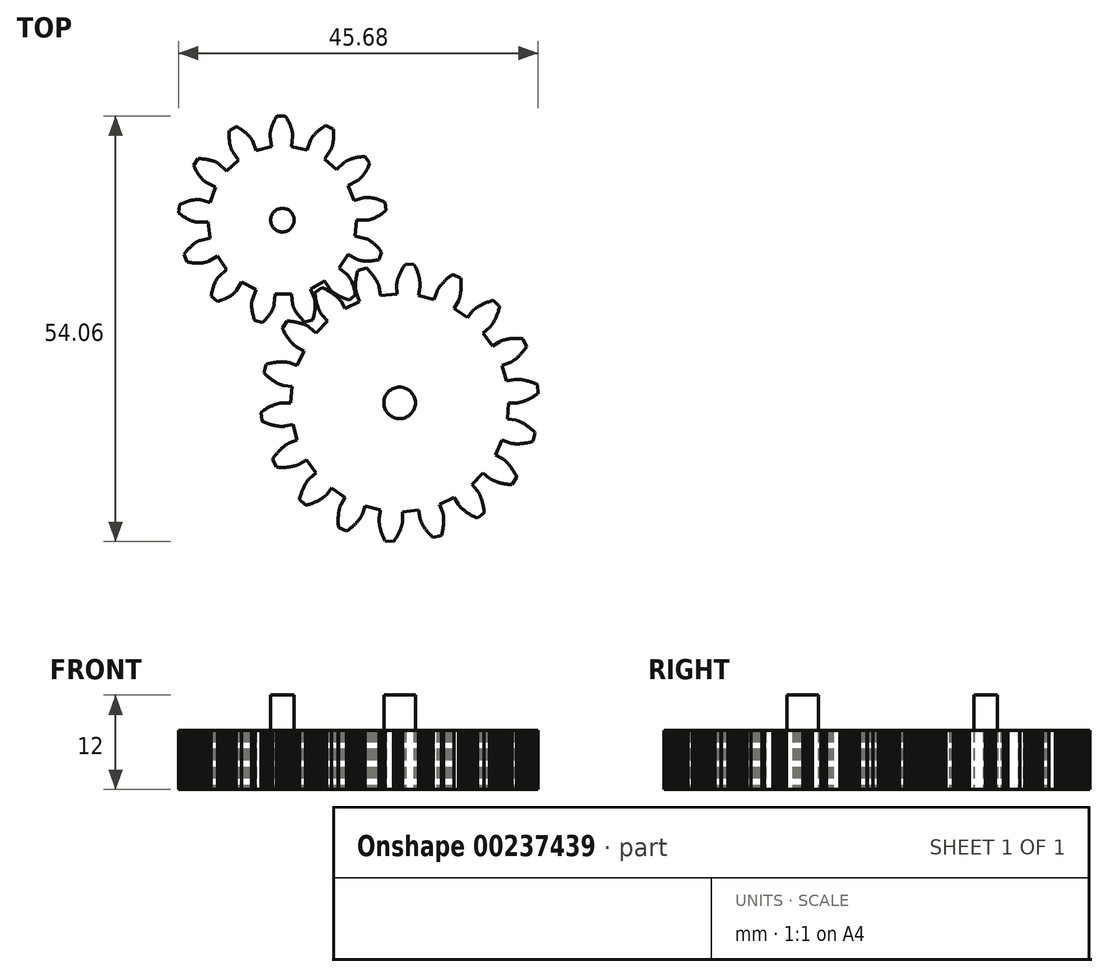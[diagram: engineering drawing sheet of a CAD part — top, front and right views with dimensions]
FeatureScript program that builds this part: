
annotation { "Feature Type Name" : "Feature", "Feature Type Description" : "" }
export const myFeature = defineFeature(function(context is Context, id is Id, definition is map)
    precondition{}
    {
        {
            var Q0;
            Q0=qCreatedBy(makeId("Top.planeOp"),FACE);
            var sketch = newSketch(context, id + "F0", { "sketchPlane" : qUnion([Q0])});
            skLineSegment(sketch, "E0", {"start": v(-0.69, 46.02) * mm, "end": v(3.77, 46.02) * mm});
            skLineSegment(sketch, "E1", {"start": v(3.77, 46.02) * mm, "end": v(3.8, 46.02) * mm});
            skLineSegment(sketch, "E2", {"start": v(3.8, 46.02) * mm, "end": v(3.86, 46.02) * mm});
            skLineSegment(sketch, "E3", {"start": v(3.86, 46.02) * mm, "end": v(3.94, 46.03) * mm});
            skLineSegment(sketch, "E4", {"start": v(3.94, 46.03) * mm, "end": v(4.05, 46.04) * mm});
            skLineSegment(sketch, "E5", {"start": v(4.05, 46.04) * mm, "end": v(4.18, 46.06) * mm});
            skLineSegment(sketch, "E6", {"start": v(4.18, 46.06) * mm, "end": v(4.34, 46.09) * mm});
            skLineSegment(sketch, "E7", {"start": v(4.34, 46.09) * mm, "end": v(4.52, 46.12) * mm});
            skLineSegment(sketch, "E8", {"start": v(4.52, 46.12) * mm, "end": v(4.72, 46.17) * mm});
            skLineSegment(sketch, "E9", {"start": v(4.72, 46.17) * mm, "end": v(4.95, 46.23) * mm});
            skLineSegment(sketch, "E10", {"start": v(4.95, 46.23) * mm, "end": v(5.2, 46.3) * mm});
            skLineSegment(sketch, "E11", {"start": v(5.2, 46.3) * mm, "end": v(5.48, 46.38) * mm});
            skLineSegment(sketch, "E12", {"start": v(5.48, 46.38) * mm, "end": v(5.78, 46.48) * mm});
            skLineSegment(sketch, "E13", {"start": v(5.78, 46.48) * mm, "end": v(6.1, 46.6) * mm});
            skLineSegment(sketch, "E14", {"start": v(6.1, 46.6) * mm, "end": v(6.44, 46.74) * mm});
            skLineSegment(sketch, "E15", {"start": v(6.44, 46.74) * mm, "end": v(6.8, 46.9) * mm});
            skLineSegment(sketch, "E16", {"start": v(6.8, 46.9) * mm, "end": v(7.18, 47.07) * mm});
            skLineSegment(sketch, "E17", {"start": v(7.18, 47.07) * mm, "end": v(7.58, 47.27) * mm});
            skLineSegment(sketch, "E18", {"start": v(7.58, 47.27) * mm, "end": v(8, 47.49) * mm});
            skLineSegment(sketch, "E19", {"start": v(8, 47.49) * mm, "end": v(8.42, 47.73) * mm});
            skLineSegment(sketch, "E20", {"start": v(8.42, 47.73) * mm, "end": v(8.87, 48) * mm});
            skLineSegment(sketch, "E21", {"start": v(8.87, 48) * mm, "end": v(9.33, 48.3) * mm});
            skLineSegment(sketch, "E22", {"start": v(9.33, 48.3) * mm, "end": v(9.8, 48.62) * mm});
            skLineSegment(sketch, "E23", {"start": v(9.8, 48.62) * mm, "end": v(10.3, 48.96) * mm});
            skLineSegment(sketch, "E24", {"start": v(10.3, 48.96) * mm, "end": v(10.8, 49.34) * mm});
            skLineSegment(sketch, "E25", {"start": v(10.8, 49.34) * mm, "end": v(11.3, 49.75) * mm});
            skLineSegment(sketch, "E26", {"start": v(11.3, 49.75) * mm, "end": v(11.76, 50.18) * mm});
            skLineSegment(sketch, "E27", {"start": v(11.76, 50.18) * mm, "end": v(11.3, 53.55) * mm});
            skLineSegment(sketch, "E28", {"start": v(11.3, 53.55) * mm, "end": v(10.75, 53.85) * mm});
            skLineSegment(sketch, "E29", {"start": v(10.75, 53.85) * mm, "end": v(10.16, 54.1) * mm});
            skLineSegment(sketch, "E30", {"start": v(10.16, 54.1) * mm, "end": v(9.58, 54.34) * mm});
            skLineSegment(sketch, "E31", {"start": v(9.58, 54.34) * mm, "end": v(9.01, 54.55) * mm});
            skLineSegment(sketch, "E32", {"start": v(9.01, 54.55) * mm, "end": v(8.47, 54.74) * mm});
            skLineSegment(sketch, "E33", {"start": v(8.47, 54.74) * mm, "end": v(7.95, 54.9) * mm});
            skLineSegment(sketch, "E34", {"start": v(7.95, 54.9) * mm, "end": v(7.45, 55.04) * mm});
            skLineSegment(sketch, "E35", {"start": v(7.45, 55.04) * mm, "end": v(6.97, 55.16) * mm});
            skLineSegment(sketch, "E36", {"start": v(6.97, 55.16) * mm, "end": v(6.5, 55.26) * mm});
            skLineSegment(sketch, "E37", {"start": v(6.5, 55.26) * mm, "end": v(6.07, 55.35) * mm});
            skLineSegment(sketch, "E38", {"start": v(6.07, 55.35) * mm, "end": v(5.66, 55.42) * mm});
            skLineSegment(sketch, "E39", {"start": v(5.66, 55.42) * mm, "end": v(5.27, 55.48) * mm});
            skLineSegment(sketch, "E40", {"start": v(5.27, 55.48) * mm, "end": v(4.9, 55.52) * mm});
            skLineSegment(sketch, "E41", {"start": v(4.9, 55.52) * mm, "end": v(4.57, 55.55) * mm});
            skLineSegment(sketch, "E42", {"start": v(4.57, 55.55) * mm, "end": v(4.25, 55.57) * mm});
            skLineSegment(sketch, "E43", {"start": v(4.25, 55.57) * mm, "end": v(3.97, 55.58) * mm});
            skLineSegment(sketch, "E44", {"start": v(3.97, 55.58) * mm, "end": v(3.7, 55.58) * mm});
            skLineSegment(sketch, "E45", {"start": v(3.7, 55.58) * mm, "end": v(3.47, 55.57) * mm});
            skLineSegment(sketch, "E46", {"start": v(3.47, 55.57) * mm, "end": v(3.25, 55.56) * mm});
            skLineSegment(sketch, "E47", {"start": v(3.25, 55.56) * mm, "end": v(3.07, 55.55) * mm});
            skLineSegment(sketch, "E48", {"start": v(3.07, 55.55) * mm, "end": v(2.91, 55.53) * mm});
            skLineSegment(sketch, "E49", {"start": v(2.91, 55.53) * mm, "end": v(2.78, 55.52) * mm});
            skLineSegment(sketch, "E50", {"start": v(2.78, 55.52) * mm, "end": v(2.67, 55.5) * mm});
            skLineSegment(sketch, "E51", {"start": v(2.67, 55.5) * mm, "end": v(2.6, 55.48) * mm});
            skLineSegment(sketch, "E52", {"start": v(2.6, 55.48) * mm, "end": v(2.54, 55.47) * mm});
            skLineSegment(sketch, "E53", {"start": v(2.54, 55.47) * mm, "end": v(2.5, 55.47) * mm});
            skLineSegment(sketch, "E54", {"start": v(2.5, 55.47) * mm, "end": v(-1.8, 54.3) * mm});
            skLineSegment(sketch, "E55", {"start": v(-1.8, 54.3) * mm, "end": v(-4.3, 60.64) * mm});
            skLineSegment(sketch, "E56", {"start": v(-4.3, 60.64) * mm, "end": v(-0.34, 62.71) * mm});
            skLineSegment(sketch, "E57", {"start": v(-0.34, 62.71) * mm, "end": v(-0.31, 62.73) * mm});
            skLineSegment(sketch, "E58", {"start": v(-0.31, 62.73) * mm, "end": v(-0.27, 62.76) * mm});
            skLineSegment(sketch, "E59", {"start": v(-0.27, 62.76) * mm, "end": v(-0.2, 62.8) * mm});
            skLineSegment(sketch, "E60", {"start": v(-0.2, 62.8) * mm, "end": v(-0.1, 62.86) * mm});
            skLineSegment(sketch, "E61", {"start": v(-0.1, 62.86) * mm, "end": v(0, 62.94) * mm});
            skLineSegment(sketch, "E62", {"start": v(0, 62.94) * mm, "end": v(0.13, 63.03) * mm});
            skLineSegment(sketch, "E63", {"start": v(0.13, 63.03) * mm, "end": v(0.27, 63.15) * mm});
            skLineSegment(sketch, "E64", {"start": v(0.27, 63.15) * mm, "end": v(0.43, 63.29) * mm});
            skLineSegment(sketch, "E65", {"start": v(0.43, 63.29) * mm, "end": v(0.6, 63.44) * mm});
            skLineSegment(sketch, "E66", {"start": v(0.6, 63.44) * mm, "end": v(0.8, 63.62) * mm});
            skLineSegment(sketch, "E67", {"start": v(0.8, 63.62) * mm, "end": v(1, 63.83) * mm});
            skLineSegment(sketch, "E68", {"start": v(1, 63.83) * mm, "end": v(1.22, 64.06) * mm});
            skLineSegment(sketch, "E69", {"start": v(1.22, 64.06) * mm, "end": v(1.45, 64.3) * mm});
            skLineSegment(sketch, "E70", {"start": v(1.45, 64.3) * mm, "end": v(1.69, 64.59) * mm});
            skLineSegment(sketch, "E71", {"start": v(1.69, 64.59) * mm, "end": v(1.93, 64.9) * mm});
            skLineSegment(sketch, "E72", {"start": v(1.93, 64.9) * mm, "end": v(2.19, 65.22) * mm});
            skLineSegment(sketch, "E73", {"start": v(2.19, 65.22) * mm, "end": v(2.45, 65.58) * mm});
            skLineSegment(sketch, "E74", {"start": v(2.45, 65.58) * mm, "end": v(2.71, 65.97) * mm});
            skLineSegment(sketch, "E75", {"start": v(2.71, 65.97) * mm, "end": v(2.98, 66.39) * mm});
            skLineSegment(sketch, "E76", {"start": v(2.98, 66.39) * mm, "end": v(3.25, 66.83) * mm});
            skLineSegment(sketch, "E77", {"start": v(3.25, 66.83) * mm, "end": v(3.53, 67.3) * mm});
            skLineSegment(sketch, "E78", {"start": v(3.53, 67.3) * mm, "end": v(3.8, 67.81) * mm});
            skLineSegment(sketch, "E79", {"start": v(3.8, 67.81) * mm, "end": v(4.07, 68.35) * mm});
            skLineSegment(sketch, "E80", {"start": v(4.07, 68.35) * mm, "end": v(4.33, 68.92) * mm});
            skLineSegment(sketch, "E81", {"start": v(4.33, 68.92) * mm, "end": v(4.6, 69.51) * mm});
            skLineSegment(sketch, "E82", {"start": v(4.6, 69.51) * mm, "end": v(4.8, 70.1) * mm});
            skLineSegment(sketch, "E83", {"start": v(4.8, 70.1) * mm, "end": v(2.83, 72.88) * mm});
            skLineSegment(sketch, "E84", {"start": v(2.83, 72.88) * mm, "end": v(2.2, 72.89) * mm});
            skLineSegment(sketch, "E85", {"start": v(2.2, 72.89) * mm, "end": v(1.55, 72.84) * mm});
            skLineSegment(sketch, "E86", {"start": v(1.55, 72.84) * mm, "end": v(0.93, 72.78) * mm});
            skLineSegment(sketch, "E87", {"start": v(0.93, 72.78) * mm, "end": v(0.34, 72.7) * mm});
            skLineSegment(sketch, "E88", {"start": v(0.34, 72.7) * mm, "end": v(-0.23, 72.61) * mm});
            skLineSegment(sketch, "E89", {"start": v(-0.23, 72.61) * mm, "end": v(-0.77, 72.51) * mm});
            skLineSegment(sketch, "E90", {"start": v(-0.77, 72.51) * mm, "end": v(-1.28, 72.4) * mm});
            skLineSegment(sketch, "E91", {"start": v(-1.28, 72.4) * mm, "end": v(-1.76, 72.29) * mm});
            skLineSegment(sketch, "E92", {"start": v(-1.76, 72.29) * mm, "end": v(-2.22, 72.17) * mm});
            skLineSegment(sketch, "E93", {"start": v(-2.22, 72.17) * mm, "end": v(-2.64, 72.04) * mm});
            skLineSegment(sketch, "E94", {"start": v(-2.64, 72.04) * mm, "end": v(-3.04, 71.91) * mm});
            skLineSegment(sketch, "E95", {"start": v(-3.04, 71.91) * mm, "end": v(-3.4, 71.78) * mm});
            skLineSegment(sketch, "E96", {"start": v(-3.4, 71.78) * mm, "end": v(-3.75, 71.65) * mm});
            skLineSegment(sketch, "E97", {"start": v(-3.75, 71.65) * mm, "end": v(-4.06, 71.52) * mm});
            skLineSegment(sketch, "E98", {"start": v(-4.06, 71.52) * mm, "end": v(-4.35, 71.39) * mm});
            skLineSegment(sketch, "E99", {"start": v(-4.35, 71.39) * mm, "end": v(-4.61, 71.26) * mm});
            skLineSegment(sketch, "E100", {"start": v(-4.61, 71.26) * mm, "end": v(-4.84, 71.14) * mm});
            skLineSegment(sketch, "E101", {"start": v(-4.84, 71.14) * mm, "end": v(-5.05, 71.03) * mm});
            skLineSegment(sketch, "E102", {"start": v(-5.05, 71.03) * mm, "end": v(-5.23, 70.92) * mm});
            skLineSegment(sketch, "E103", {"start": v(-5.23, 70.92) * mm, "end": v(-5.4, 70.82) * mm});
            skLineSegment(sketch, "E104", {"start": v(-5.4, 70.82) * mm, "end": v(-5.52, 70.73) * mm});
            skLineSegment(sketch, "E105", {"start": v(-5.52, 70.73) * mm, "end": v(-5.63, 70.66) * mm});
            skLineSegment(sketch, "E106", {"start": v(-5.63, 70.66) * mm, "end": v(-5.72, 70.6) * mm});
            skLineSegment(sketch, "E107", {"start": v(-5.72, 70.6) * mm, "end": v(-5.78, 70.54) * mm});
            skLineSegment(sketch, "E108", {"start": v(-5.78, 70.54) * mm, "end": v(-5.83, 70.5) * mm});
            skLineSegment(sketch, "E109", {"start": v(-5.83, 70.5) * mm, "end": v(-5.85, 70.49) * mm});
            skLineSegment(sketch, "E110", {"start": v(-5.85, 70.49) * mm, "end": v(-9.12, 67.45) * mm});
            skLineSegment(sketch, "E111", {"start": v(-9.12, 67.45) * mm, "end": v(-14.28, 71.9) * mm});
            skLineSegment(sketch, "E112", {"start": v(-14.28, 71.9) * mm, "end": v(-11.74, 75.58) * mm});
            skLineSegment(sketch, "E113", {"start": v(-11.74, 75.58) * mm, "end": v(-11.72, 75.6) * mm});
            skLineSegment(sketch, "E114", {"start": v(-11.72, 75.6) * mm, "end": v(-11.7, 75.65) * mm});
            skLineSegment(sketch, "E115", {"start": v(-11.7, 75.65) * mm, "end": v(-11.65, 75.72) * mm});
            skLineSegment(sketch, "E116", {"start": v(-11.65, 75.72) * mm, "end": v(-11.6, 75.82) * mm});
            skLineSegment(sketch, "E117", {"start": v(-11.6, 75.82) * mm, "end": v(-11.54, 75.94) * mm});
            skLineSegment(sketch, "E118", {"start": v(-11.54, 75.94) * mm, "end": v(-11.48, 76.08) * mm});
            skLineSegment(sketch, "E119", {"start": v(-11.48, 76.08) * mm, "end": v(-11.4, 76.25) * mm});
            skLineSegment(sketch, "E120", {"start": v(-11.4, 76.25) * mm, "end": v(-11.32, 76.45) * mm});
            skLineSegment(sketch, "E121", {"start": v(-11.32, 76.45) * mm, "end": v(-11.24, 76.67) * mm});
            skLineSegment(sketch, "E122", {"start": v(-11.24, 76.67) * mm, "end": v(-11.15, 76.92) * mm});
            skLineSegment(sketch, "E123", {"start": v(-11.15, 76.92) * mm, "end": v(-11.07, 77.2) * mm});
            skLineSegment(sketch, "E124", {"start": v(-11.07, 77.2) * mm, "end": v(-10.98, 77.5) * mm});
            skLineSegment(sketch, "E125", {"start": v(-10.98, 77.5) * mm, "end": v(-10.9, 77.83) * mm});
            skLineSegment(sketch, "E126", {"start": v(-10.9, 77.83) * mm, "end": v(-10.82, 78.18) * mm});
            skLineSegment(sketch, "E127", {"start": v(-10.82, 78.18) * mm, "end": v(-10.74, 78.57) * mm});
            skLineSegment(sketch, "E128", {"start": v(-10.74, 78.57) * mm, "end": v(-10.67, 78.98) * mm});
            skLineSegment(sketch, "E129", {"start": v(-10.67, 78.98) * mm, "end": v(-10.6, 79.42) * mm});
            skLineSegment(sketch, "E130", {"start": v(-10.6, 79.42) * mm, "end": v(-10.55, 79.89) * mm});
            skLineSegment(sketch, "E131", {"start": v(-10.55, 79.89) * mm, "end": v(-10.5, 80.38) * mm});
            skLineSegment(sketch, "E132", {"start": v(-10.5, 80.38) * mm, "end": v(-10.47, 80.9) * mm});
            skLineSegment(sketch, "E133", {"start": v(-10.47, 80.9) * mm, "end": v(-10.45, 81.45) * mm});
            skLineSegment(sketch, "E134", {"start": v(-10.45, 81.45) * mm, "end": v(-10.45, 82.02) * mm});
            skLineSegment(sketch, "E135", {"start": v(-10.45, 82.02) * mm, "end": v(-10.46, 82.62) * mm});
            skLineSegment(sketch, "E136", {"start": v(-10.46, 82.62) * mm, "end": v(-10.49, 83.24) * mm});
            skLineSegment(sketch, "E137", {"start": v(-10.49, 83.24) * mm, "end": v(-10.53, 83.9) * mm});
            skLineSegment(sketch, "E138", {"start": v(-10.53, 83.9) * mm, "end": v(-10.63, 84.51) * mm});
            skLineSegment(sketch, "E139", {"start": v(-10.63, 84.51) * mm, "end": v(-13.66, 86.06) * mm});
            skLineSegment(sketch, "E140", {"start": v(-13.66, 86.06) * mm, "end": v(-14.22, 85.77) * mm});
            skLineSegment(sketch, "E141", {"start": v(-14.22, 85.77) * mm, "end": v(-14.77, 85.43) * mm});
            skLineSegment(sketch, "E142", {"start": v(-14.77, 85.43) * mm, "end": v(-15.3, 85.08) * mm});
            skLineSegment(sketch, "E143", {"start": v(-15.3, 85.08) * mm, "end": v(-15.78, 84.74) * mm});
            skLineSegment(sketch, "E144", {"start": v(-15.78, 84.74) * mm, "end": v(-16.24, 84.4) * mm});
            skLineSegment(sketch, "E145", {"start": v(-16.24, 84.4) * mm, "end": v(-16.68, 84.06) * mm});
            skLineSegment(sketch, "E146", {"start": v(-16.68, 84.06) * mm, "end": v(-17.08, 83.73) * mm});
            skLineSegment(sketch, "E147", {"start": v(-17.08, 83.73) * mm, "end": v(-17.45, 83.4) * mm});
            skLineSegment(sketch, "E148", {"start": v(-17.45, 83.4) * mm, "end": v(-17.8, 83.08) * mm});
            skLineSegment(sketch, "E149", {"start": v(-17.8, 83.08) * mm, "end": v(-18.11, 82.77) * mm});
            skLineSegment(sketch, "E150", {"start": v(-18.11, 82.77) * mm, "end": v(-18.4, 82.47) * mm});
            skLineSegment(sketch, "E151", {"start": v(-18.4, 82.47) * mm, "end": v(-18.67, 82.18) * mm});
            skLineSegment(sketch, "E152", {"start": v(-18.67, 82.18) * mm, "end": v(-18.91, 81.9) * mm});
            skLineSegment(sketch, "E153", {"start": v(-18.91, 81.9) * mm, "end": v(-19.13, 81.65) * mm});
            skLineSegment(sketch, "E154", {"start": v(-19.13, 81.65) * mm, "end": v(-19.32, 81.4) * mm});
            skLineSegment(sketch, "E155", {"start": v(-19.32, 81.4) * mm, "end": v(-19.5, 81.17) * mm});
            skLineSegment(sketch, "E156", {"start": v(-19.5, 81.17) * mm, "end": v(-19.65, 80.95) * mm});
            skLineSegment(sketch, "E157", {"start": v(-19.65, 80.95) * mm, "end": v(-19.78, 80.75) * mm});
            skLineSegment(sketch, "E158", {"start": v(-19.78, 80.75) * mm, "end": v(-19.89, 80.57) * mm});
            skLineSegment(sketch, "E159", {"start": v(-19.89, 80.57) * mm, "end": v(-19.98, 80.41) * mm});
            skLineSegment(sketch, "E160", {"start": v(-19.98, 80.41) * mm, "end": v(-20.06, 80.27) * mm});
            skLineSegment(sketch, "E161", {"start": v(-20.06, 80.27) * mm, "end": v(-20.12, 80.16) * mm});
            skLineSegment(sketch, "E162", {"start": v(-20.12, 80.16) * mm, "end": v(-20.17, 80.06) * mm});
            skLineSegment(sketch, "E163", {"start": v(-20.17, 80.06) * mm, "end": v(-20.2, 79.99) * mm});
            skLineSegment(sketch, "E164", {"start": v(-20.2, 79.99) * mm, "end": v(-20.22, 79.93) * mm});
            skLineSegment(sketch, "E165", {"start": v(-20.22, 79.93) * mm, "end": v(-20.23, 79.9) * mm});
            skLineSegment(sketch, "E166", {"start": v(-20.23, 79.9) * mm, "end": v(-21.71, 75.7) * mm});
            skLineSegment(sketch, "E167", {"start": v(-21.71, 75.7) * mm, "end": v(-28.35, 77.25) * mm});
            skLineSegment(sketch, "E168", {"start": v(-28.35, 77.25) * mm, "end": v(-27.81, 81.68) * mm});
            skLineSegment(sketch, "E169", {"start": v(-27.81, 81.68) * mm, "end": v(-27.81, 81.7) * mm});
            skLineSegment(sketch, "E170", {"start": v(-27.81, 81.7) * mm, "end": v(-27.8, 81.76) * mm});
            skLineSegment(sketch, "E171", {"start": v(-27.8, 81.76) * mm, "end": v(-27.8, 81.84) * mm});
            skLineSegment(sketch, "E172", {"start": v(-27.8, 81.84) * mm, "end": v(-27.8, 81.95) * mm});
            skLineSegment(sketch, "E173", {"start": v(-27.8, 81.95) * mm, "end": v(-27.8, 82.08) * mm});
            skLineSegment(sketch, "E174", {"start": v(-27.8, 82.08) * mm, "end": v(-27.81, 82.24) * mm});
            skLineSegment(sketch, "E175", {"start": v(-27.81, 82.24) * mm, "end": v(-27.83, 82.43) * mm});
            skLineSegment(sketch, "E176", {"start": v(-27.83, 82.43) * mm, "end": v(-27.85, 82.64) * mm});
            skLineSegment(sketch, "E177", {"start": v(-27.85, 82.64) * mm, "end": v(-27.88, 82.87) * mm});
            skLineSegment(sketch, "E178", {"start": v(-27.88, 82.87) * mm, "end": v(-27.92, 83.13) * mm});
            skLineSegment(sketch, "E179", {"start": v(-27.92, 83.13) * mm, "end": v(-27.97, 83.42) * mm});
            skLineSegment(sketch, "E180", {"start": v(-27.97, 83.42) * mm, "end": v(-28.03, 83.72) * mm});
            skLineSegment(sketch, "E181", {"start": v(-28.03, 83.72) * mm, "end": v(-28.11, 84.06) * mm});
            skLineSegment(sketch, "E182", {"start": v(-28.11, 84.06) * mm, "end": v(-28.2, 84.41) * mm});
            skLineSegment(sketch, "E183", {"start": v(-28.2, 84.41) * mm, "end": v(-28.32, 84.79) * mm});
            skLineSegment(sketch, "E184", {"start": v(-28.32, 84.79) * mm, "end": v(-28.45, 85.18) * mm});
            skLineSegment(sketch, "E185", {"start": v(-28.45, 85.18) * mm, "end": v(-28.6, 85.6) * mm});
            skLineSegment(sketch, "E186", {"start": v(-28.6, 85.6) * mm, "end": v(-28.76, 86.04) * mm});
            skLineSegment(sketch, "E187", {"start": v(-28.76, 86.04) * mm, "end": v(-28.95, 86.5) * mm});
            skLineSegment(sketch, "E188", {"start": v(-28.95, 86.5) * mm, "end": v(-29.16, 86.98) * mm});
            skLineSegment(sketch, "E189", {"start": v(-29.16, 86.98) * mm, "end": v(-29.4, 87.47) * mm});
            skLineSegment(sketch, "E190", {"start": v(-29.4, 87.47) * mm, "end": v(-29.66, 87.98) * mm});
            skLineSegment(sketch, "E191", {"start": v(-29.66, 87.98) * mm, "end": v(-29.95, 88.5) * mm});
            skLineSegment(sketch, "E192", {"start": v(-29.95, 88.5) * mm, "end": v(-30.27, 89.05) * mm});
            skLineSegment(sketch, "E193", {"start": v(-30.27, 89.05) * mm, "end": v(-30.6, 89.6) * mm});
            skLineSegment(sketch, "E194", {"start": v(-30.6, 89.6) * mm, "end": v(-30.98, 90.1) * mm});
            skLineSegment(sketch, "E195", {"start": v(-30.98, 90.1) * mm, "end": v(-34.38, 90.06) * mm});
            skLineSegment(sketch, "E196", {"start": v(-34.38, 90.06) * mm, "end": v(-34.74, 89.55) * mm});
            skLineSegment(sketch, "E197", {"start": v(-34.74, 89.55) * mm, "end": v(-35.07, 88.99) * mm});
            skLineSegment(sketch, "E198", {"start": v(-35.07, 88.99) * mm, "end": v(-35.38, 88.44) * mm});
            skLineSegment(sketch, "E199", {"start": v(-35.38, 88.44) * mm, "end": v(-35.65, 87.9) * mm});
            skLineSegment(sketch, "E200", {"start": v(-35.65, 87.9) * mm, "end": v(-35.9, 87.4) * mm});
            skLineSegment(sketch, "E201", {"start": v(-35.9, 87.4) * mm, "end": v(-36.12, 86.9) * mm});
            skLineSegment(sketch, "E202", {"start": v(-36.12, 86.9) * mm, "end": v(-36.33, 86.4) * mm});
            skLineSegment(sketch, "E203", {"start": v(-36.33, 86.4) * mm, "end": v(-36.5, 85.95) * mm});
            skLineSegment(sketch, "E204", {"start": v(-36.5, 85.95) * mm, "end": v(-36.66, 85.5) * mm});
            skLineSegment(sketch, "E205", {"start": v(-36.66, 85.5) * mm, "end": v(-36.8, 85.08) * mm});
            skLineSegment(sketch, "E206", {"start": v(-36.8, 85.08) * mm, "end": v(-36.92, 84.68) * mm});
            skLineSegment(sketch, "E207", {"start": v(-36.92, 84.68) * mm, "end": v(-37.02, 84.3) * mm});
            skLineSegment(sketch, "E208", {"start": v(-37.02, 84.3) * mm, "end": v(-37.1, 83.95) * mm});
            skLineSegment(sketch, "E209", {"start": v(-37.1, 83.95) * mm, "end": v(-37.18, 83.61) * mm});
            skLineSegment(sketch, "E210", {"start": v(-37.18, 83.61) * mm, "end": v(-37.23, 83.3) * mm});
            skLineSegment(sketch, "E211", {"start": v(-37.23, 83.3) * mm, "end": v(-37.28, 83.02) * mm});
            skLineSegment(sketch, "E212", {"start": v(-37.28, 83.02) * mm, "end": v(-37.31, 82.76) * mm});
            skLineSegment(sketch, "E213", {"start": v(-37.31, 82.76) * mm, "end": v(-37.33, 82.52) * mm});
            skLineSegment(sketch, "E214", {"start": v(-37.33, 82.52) * mm, "end": v(-37.35, 82.31) * mm});
            skLineSegment(sketch, "E215", {"start": v(-37.35, 82.31) * mm, "end": v(-37.36, 82.13) * mm});
            skLineSegment(sketch, "E216", {"start": v(-37.36, 82.13) * mm, "end": v(-37.36, 81.97) * mm});
            skLineSegment(sketch, "E217", {"start": v(-37.36, 81.97) * mm, "end": v(-37.36, 81.83) * mm});
            skLineSegment(sketch, "E218", {"start": v(-37.36, 81.83) * mm, "end": v(-37.36, 81.73) * mm});
            skLineSegment(sketch, "E219", {"start": v(-37.36, 81.73) * mm, "end": v(-37.35, 81.65) * mm});
            skLineSegment(sketch, "E220", {"start": v(-37.35, 81.65) * mm, "end": v(-37.35, 81.59) * mm});
            skLineSegment(sketch, "E221", {"start": v(-37.35, 81.59) * mm, "end": v(-37.34, 81.56) * mm});
            skLineSegment(sketch, "E222", {"start": v(-37.34, 81.56) * mm, "end": v(-36.7, 77.15) * mm});
            skLineSegment(sketch, "E223", {"start": v(-36.7, 77.15) * mm, "end": v(-43.3, 75.43) * mm});
            skLineSegment(sketch, "E224", {"start": v(-43.3, 75.43) * mm, "end": v(-44.88, 79.6) * mm});
            skLineSegment(sketch, "E225", {"start": v(-44.88, 79.6) * mm, "end": v(-44.9, 79.63) * mm});
            skLineSegment(sketch, "E226", {"start": v(-44.9, 79.63) * mm, "end": v(-44.92, 79.68) * mm});
            skLineSegment(sketch, "E227", {"start": v(-44.92, 79.68) * mm, "end": v(-44.95, 79.76) * mm});
            skLineSegment(sketch, "E228", {"start": v(-44.95, 79.76) * mm, "end": v(-45, 79.85) * mm});
            skLineSegment(sketch, "E229", {"start": v(-45, 79.85) * mm, "end": v(-45.06, 79.97) * mm});
            skLineSegment(sketch, "E230", {"start": v(-45.06, 79.97) * mm, "end": v(-45.14, 80.1) * mm});
            skLineSegment(sketch, "E231", {"start": v(-45.14, 80.1) * mm, "end": v(-45.24, 80.26) * mm});
            skLineSegment(sketch, "E232", {"start": v(-45.24, 80.26) * mm, "end": v(-45.36, 80.44) * mm});
            skLineSegment(sketch, "E233", {"start": v(-45.36, 80.44) * mm, "end": v(-45.5, 80.63) * mm});
            skLineSegment(sketch, "E234", {"start": v(-45.5, 80.63) * mm, "end": v(-45.65, 80.85) * mm});
            skLineSegment(sketch, "E235", {"start": v(-45.65, 80.85) * mm, "end": v(-45.83, 81.07) * mm});
            skLineSegment(sketch, "E236", {"start": v(-45.83, 81.07) * mm, "end": v(-46.03, 81.32) * mm});
            skLineSegment(sketch, "E237", {"start": v(-46.03, 81.32) * mm, "end": v(-46.25, 81.57) * mm});
            skLineSegment(sketch, "E238", {"start": v(-46.25, 81.57) * mm, "end": v(-46.5, 81.84) * mm});
            skLineSegment(sketch, "E239", {"start": v(-46.5, 81.84) * mm, "end": v(-46.77, 82.13) * mm});
            skLineSegment(sketch, "E240", {"start": v(-46.77, 82.13) * mm, "end": v(-47.07, 82.42) * mm});
            skLineSegment(sketch, "E241", {"start": v(-47.07, 82.42) * mm, "end": v(-47.4, 82.72) * mm});
            skLineSegment(sketch, "E242", {"start": v(-47.4, 82.72) * mm, "end": v(-47.75, 83.03) * mm});
            skLineSegment(sketch, "E243", {"start": v(-47.75, 83.03) * mm, "end": v(-48.13, 83.35) * mm});
            skLineSegment(sketch, "E244", {"start": v(-48.13, 83.35) * mm, "end": v(-48.54, 83.67) * mm});
            skLineSegment(sketch, "E245", {"start": v(-48.54, 83.67) * mm, "end": v(-48.98, 84) * mm});
            skLineSegment(sketch, "E246", {"start": v(-48.98, 84) * mm, "end": v(-49.45, 84.33) * mm});
            skLineSegment(sketch, "E247", {"start": v(-49.45, 84.33) * mm, "end": v(-49.95, 84.66) * mm});
            skLineSegment(sketch, "E248", {"start": v(-49.95, 84.66) * mm, "end": v(-50.48, 85) * mm});
            skLineSegment(sketch, "E249", {"start": v(-50.48, 85) * mm, "end": v(-51.04, 85.32) * mm});
            skLineSegment(sketch, "E250", {"start": v(-51.04, 85.32) * mm, "end": v(-51.6, 85.6) * mm});
            skLineSegment(sketch, "E251", {"start": v(-51.6, 85.6) * mm, "end": v(-54.6, 83.98) * mm});
            skLineSegment(sketch, "E252", {"start": v(-54.6, 83.98) * mm, "end": v(-54.68, 83.35) * mm});
            skLineSegment(sketch, "E253", {"start": v(-54.68, 83.35) * mm, "end": v(-54.7, 82.7) * mm});
            skLineSegment(sketch, "E254", {"start": v(-54.7, 82.7) * mm, "end": v(-54.72, 82.08) * mm});
            skLineSegment(sketch, "E255", {"start": v(-54.72, 82.08) * mm, "end": v(-54.71, 81.48) * mm});
            skLineSegment(sketch, "E256", {"start": v(-54.71, 81.48) * mm, "end": v(-54.7, 80.9) * mm});
            skLineSegment(sketch, "E257", {"start": v(-54.7, 80.9) * mm, "end": v(-54.66, 80.36) * mm});
            skLineSegment(sketch, "E258", {"start": v(-54.66, 80.36) * mm, "end": v(-54.62, 79.84) * mm});
            skLineSegment(sketch, "E259", {"start": v(-54.62, 79.84) * mm, "end": v(-54.56, 79.35) * mm});
            skLineSegment(sketch, "E260", {"start": v(-54.56, 79.35) * mm, "end": v(-54.5, 78.88) * mm});
            skLineSegment(sketch, "E261", {"start": v(-54.5, 78.88) * mm, "end": v(-54.42, 78.44) * mm});
            skLineSegment(sketch, "E262", {"start": v(-54.42, 78.44) * mm, "end": v(-54.34, 78.03) * mm});
            skLineSegment(sketch, "E263", {"start": v(-54.34, 78.03) * mm, "end": v(-54.25, 77.65) * mm});
            skLineSegment(sketch, "E264", {"start": v(-54.25, 77.65) * mm, "end": v(-54.16, 77.3) * mm});
            skLineSegment(sketch, "E265", {"start": v(-54.16, 77.3) * mm, "end": v(-54.07, 76.97) * mm});
            skLineSegment(sketch, "E266", {"start": v(-54.07, 76.97) * mm, "end": v(-53.98, 76.67) * mm});
            skLineSegment(sketch, "E267", {"start": v(-53.98, 76.67) * mm, "end": v(-53.88, 76.4) * mm});
            skLineSegment(sketch, "E268", {"start": v(-53.88, 76.4) * mm, "end": v(-53.8, 76.15) * mm});
            skLineSegment(sketch, "E269", {"start": v(-53.8, 76.15) * mm, "end": v(-53.7, 75.93) * mm});
            skLineSegment(sketch, "E270", {"start": v(-53.7, 75.93) * mm, "end": v(-53.62, 75.74) * mm});
            skLineSegment(sketch, "E271", {"start": v(-53.62, 75.74) * mm, "end": v(-53.54, 75.57) * mm});
            skLineSegment(sketch, "E272", {"start": v(-53.54, 75.57) * mm, "end": v(-53.47, 75.43) * mm});
            skLineSegment(sketch, "E273", {"start": v(-53.47, 75.43) * mm, "end": v(-53.4, 75.3) * mm});
            skLineSegment(sketch, "E274", {"start": v(-53.4, 75.3) * mm, "end": v(-53.35, 75.21) * mm});
            skLineSegment(sketch, "E275", {"start": v(-53.35, 75.21) * mm, "end": v(-53.31, 75.14) * mm});
            skLineSegment(sketch, "E276", {"start": v(-53.31, 75.14) * mm, "end": v(-53.28, 75.1) * mm});
            skLineSegment(sketch, "E277", {"start": v(-53.28, 75.1) * mm, "end": v(-53.26, 75.07) * mm});
            skLineSegment(sketch, "E278", {"start": v(-53.26, 75.07) * mm, "end": v(-50.64, 71.46) * mm});
            skLineSegment(sketch, "E279", {"start": v(-50.64, 71.46) * mm, "end": v(-55.69, 66.88) * mm});
            skLineSegment(sketch, "E280", {"start": v(-55.69, 66.88) * mm, "end": v(-59.03, 69.84) * mm});
            skLineSegment(sketch, "E281", {"start": v(-59.03, 69.84) * mm, "end": v(-59.05, 69.86) * mm});
            skLineSegment(sketch, "E282", {"start": v(-59.05, 69.86) * mm, "end": v(-59.1, 69.9) * mm});
            skLineSegment(sketch, "E283", {"start": v(-59.1, 69.9) * mm, "end": v(-59.16, 69.94) * mm});
            skLineSegment(sketch, "E284", {"start": v(-59.16, 69.94) * mm, "end": v(-59.25, 70) * mm});
            skLineSegment(sketch, "E285", {"start": v(-59.25, 70) * mm, "end": v(-59.36, 70.08) * mm});
            skLineSegment(sketch, "E286", {"start": v(-59.36, 70.08) * mm, "end": v(-59.5, 70.16) * mm});
            skLineSegment(sketch, "E287", {"start": v(-59.5, 70.16) * mm, "end": v(-59.66, 70.25) * mm});
            skLineSegment(sketch, "E288", {"start": v(-59.66, 70.25) * mm, "end": v(-59.84, 70.36) * mm});
            skLineSegment(sketch, "E289", {"start": v(-59.84, 70.36) * mm, "end": v(-60.05, 70.47) * mm});
            skLineSegment(sketch, "E290", {"start": v(-60.05, 70.47) * mm, "end": v(-60.29, 70.58) * mm});
            skLineSegment(sketch, "E291", {"start": v(-60.29, 70.58) * mm, "end": v(-60.55, 70.7) * mm});
            skLineSegment(sketch, "E292", {"start": v(-60.55, 70.7) * mm, "end": v(-60.84, 70.82) * mm});
            skLineSegment(sketch, "E293", {"start": v(-60.84, 70.82) * mm, "end": v(-61.16, 70.95) * mm});
            skLineSegment(sketch, "E294", {"start": v(-61.16, 70.95) * mm, "end": v(-61.5, 71.07) * mm});
            skLineSegment(sketch, "E295", {"start": v(-61.5, 71.07) * mm, "end": v(-61.87, 71.2) * mm});
            skLineSegment(sketch, "E296", {"start": v(-61.87, 71.2) * mm, "end": v(-62.27, 71.31) * mm});
            skLineSegment(sketch, "E297", {"start": v(-62.27, 71.31) * mm, "end": v(-62.7, 71.43) * mm});
            skLineSegment(sketch, "E298", {"start": v(-62.7, 71.43) * mm, "end": v(-63.16, 71.54) * mm});
            skLineSegment(sketch, "E299", {"start": v(-63.16, 71.54) * mm, "end": v(-63.64, 71.64) * mm});
            skLineSegment(sketch, "E300", {"start": v(-63.64, 71.64) * mm, "end": v(-64.16, 71.74) * mm});
            skLineSegment(sketch, "E301", {"start": v(-64.16, 71.74) * mm, "end": v(-64.7, 71.82) * mm});
            skLineSegment(sketch, "E302", {"start": v(-64.7, 71.82) * mm, "end": v(-65.27, 71.9) * mm});
            skLineSegment(sketch, "E303", {"start": v(-65.27, 71.9) * mm, "end": v(-65.86, 71.96) * mm});
            skLineSegment(sketch, "E304", {"start": v(-65.86, 71.96) * mm, "end": v(-66.49, 72) * mm});
            skLineSegment(sketch, "E305", {"start": v(-66.49, 72) * mm, "end": v(-67.14, 72.04) * mm});
            skLineSegment(sketch, "E306", {"start": v(-67.14, 72.04) * mm, "end": v(-67.76, 72.02) * mm});
            skLineSegment(sketch, "E307", {"start": v(-67.76, 72.02) * mm, "end": v(-69.66, 69.2) * mm});
            skLineSegment(sketch, "E308", {"start": v(-69.66, 69.2) * mm, "end": v(-69.45, 68.6) * mm});
            skLineSegment(sketch, "E309", {"start": v(-69.45, 68.6) * mm, "end": v(-69.17, 68.02) * mm});
            skLineSegment(sketch, "E310", {"start": v(-69.17, 68.02) * mm, "end": v(-68.9, 67.46) * mm});
            skLineSegment(sketch, "E311", {"start": v(-68.9, 67.46) * mm, "end": v(-68.6, 66.93) * mm});
            skLineSegment(sketch, "E312", {"start": v(-68.6, 66.93) * mm, "end": v(-68.32, 66.43) * mm});
            skLineSegment(sketch, "E313", {"start": v(-68.32, 66.43) * mm, "end": v(-68.04, 65.96) * mm});
            skLineSegment(sketch, "E314", {"start": v(-68.04, 65.96) * mm, "end": v(-67.76, 65.52) * mm});
            skLineSegment(sketch, "E315", {"start": v(-67.76, 65.52) * mm, "end": v(-67.48, 65.11) * mm});
            skLineSegment(sketch, "E316", {"start": v(-67.48, 65.11) * mm, "end": v(-67.2, 64.73) * mm});
            skLineSegment(sketch, "E317", {"start": v(-67.2, 64.73) * mm, "end": v(-66.94, 64.38) * mm});
            skLineSegment(sketch, "E318", {"start": v(-66.94, 64.38) * mm, "end": v(-66.67, 64.05) * mm});
            skLineSegment(sketch, "E319", {"start": v(-66.67, 64.05) * mm, "end": v(-66.42, 63.75) * mm});
            skLineSegment(sketch, "E320", {"start": v(-66.42, 63.75) * mm, "end": v(-66.18, 63.48) * mm});
            skLineSegment(sketch, "E321", {"start": v(-66.18, 63.48) * mm, "end": v(-65.94, 63.23) * mm});
            skLineSegment(sketch, "E322", {"start": v(-65.94, 63.23) * mm, "end": v(-65.72, 63.01) * mm});
            skLineSegment(sketch, "E323", {"start": v(-65.72, 63.01) * mm, "end": v(-65.5, 62.81) * mm});
            skLineSegment(sketch, "E324", {"start": v(-65.5, 62.81) * mm, "end": v(-65.31, 62.64) * mm});
            skLineSegment(sketch, "E325", {"start": v(-65.31, 62.64) * mm, "end": v(-65.13, 62.48) * mm});
            skLineSegment(sketch, "E326", {"start": v(-65.13, 62.48) * mm, "end": v(-64.97, 62.35) * mm});
            skLineSegment(sketch, "E327", {"start": v(-64.97, 62.35) * mm, "end": v(-64.82, 62.24) * mm});
            skLineSegment(sketch, "E328", {"start": v(-64.82, 62.24) * mm, "end": v(-64.7, 62.15) * mm});
            skLineSegment(sketch, "E329", {"start": v(-64.7, 62.15) * mm, "end": v(-64.58, 62.07) * mm});
            skLineSegment(sketch, "E330", {"start": v(-64.58, 62.07) * mm, "end": v(-64.5, 62.01) * mm});
            skLineSegment(sketch, "E331", {"start": v(-64.5, 62.01) * mm, "end": v(-64.42, 61.97) * mm});
            skLineSegment(sketch, "E332", {"start": v(-64.42, 61.97) * mm, "end": v(-64.37, 61.94) * mm});
            skLineSegment(sketch, "E333", {"start": v(-64.37, 61.94) * mm, "end": v(-64.35, 61.93) * mm});
            skLineSegment(sketch, "E334", {"start": v(-64.35, 61.93) * mm, "end": v(-60.35, 59.95) * mm});
            skLineSegment(sketch, "E335", {"start": v(-60.35, 59.95) * mm, "end": v(-62.69, 53.55) * mm});
            skLineSegment(sketch, "E336", {"start": v(-62.69, 53.55) * mm, "end": v(-67.02, 54.62) * mm});
            skLineSegment(sketch, "E337", {"start": v(-67.02, 54.62) * mm, "end": v(-67.05, 54.62) * mm});
            skLineSegment(sketch, "E338", {"start": v(-67.05, 54.62) * mm, "end": v(-67.1, 54.63) * mm});
            skLineSegment(sketch, "E339", {"start": v(-67.1, 54.63) * mm, "end": v(-67.18, 54.65) * mm});
            skLineSegment(sketch, "E340", {"start": v(-67.18, 54.65) * mm, "end": v(-67.29, 54.66) * mm});
            skLineSegment(sketch, "E341", {"start": v(-67.29, 54.66) * mm, "end": v(-67.42, 54.67) * mm});
            skLineSegment(sketch, "E342", {"start": v(-67.42, 54.67) * mm, "end": v(-67.58, 54.68) * mm});
            skLineSegment(sketch, "E343", {"start": v(-67.58, 54.68) * mm, "end": v(-67.77, 54.7) * mm});
            skLineSegment(sketch, "E344", {"start": v(-67.77, 54.7) * mm, "end": v(-67.98, 54.7) * mm});
            skLineSegment(sketch, "E345", {"start": v(-67.98, 54.7) * mm, "end": v(-68.21, 54.7) * mm});
            skLineSegment(sketch, "E346", {"start": v(-68.21, 54.7) * mm, "end": v(-68.48, 54.69) * mm});
            skLineSegment(sketch, "E347", {"start": v(-68.48, 54.69) * mm, "end": v(-68.76, 54.67) * mm});
            skLineSegment(sketch, "E348", {"start": v(-68.76, 54.67) * mm, "end": v(-69.08, 54.65) * mm});
            skLineSegment(sketch, "E349", {"start": v(-69.08, 54.65) * mm, "end": v(-69.42, 54.6) * mm});
            skLineSegment(sketch, "E350", {"start": v(-69.42, 54.6) * mm, "end": v(-69.78, 54.56) * mm});
            skLineSegment(sketch, "E351", {"start": v(-69.78, 54.56) * mm, "end": v(-70.17, 54.5) * mm});
            skLineSegment(sketch, "E352", {"start": v(-70.17, 54.5) * mm, "end": v(-70.58, 54.41) * mm});
            skLineSegment(sketch, "E353", {"start": v(-70.58, 54.41) * mm, "end": v(-71.01, 54.32) * mm});
            skLineSegment(sketch, "E354", {"start": v(-71.01, 54.32) * mm, "end": v(-71.47, 54.2) * mm});
            skLineSegment(sketch, "E355", {"start": v(-71.47, 54.2) * mm, "end": v(-71.94, 54.07) * mm});
            skLineSegment(sketch, "E356", {"start": v(-71.94, 54.07) * mm, "end": v(-72.44, 53.92) * mm});
            skLineSegment(sketch, "E357", {"start": v(-72.44, 53.92) * mm, "end": v(-72.96, 53.74) * mm});
            skLineSegment(sketch, "E358", {"start": v(-72.96, 53.74) * mm, "end": v(-73.5, 53.54) * mm});
            skLineSegment(sketch, "E359", {"start": v(-73.5, 53.54) * mm, "end": v(-74.06, 53.32) * mm});
            skLineSegment(sketch, "E360", {"start": v(-74.06, 53.32) * mm, "end": v(-74.63, 53.07) * mm});
            skLineSegment(sketch, "E361", {"start": v(-74.63, 53.07) * mm, "end": v(-75.22, 52.8) * mm});
            skLineSegment(sketch, "E362", {"start": v(-75.22, 52.8) * mm, "end": v(-75.76, 52.49) * mm});
            skLineSegment(sketch, "E363", {"start": v(-75.76, 52.49) * mm, "end": v(-76.13, 49.1) * mm});
            skLineSegment(sketch, "E364", {"start": v(-76.13, 49.1) * mm, "end": v(-75.67, 48.69) * mm});
            skLineSegment(sketch, "E365", {"start": v(-75.67, 48.69) * mm, "end": v(-75.15, 48.3) * mm});
            skLineSegment(sketch, "E366", {"start": v(-75.15, 48.3) * mm, "end": v(-74.64, 47.93) * mm});
            skLineSegment(sketch, "E367", {"start": v(-74.64, 47.93) * mm, "end": v(-74.15, 47.59) * mm});
            skLineSegment(sketch, "E368", {"start": v(-74.15, 47.59) * mm, "end": v(-73.67, 47.28) * mm});
            skLineSegment(sketch, "E369", {"start": v(-73.67, 47.28) * mm, "end": v(-73.2, 47) * mm});
            skLineSegment(sketch, "E370", {"start": v(-73.2, 47) * mm, "end": v(-72.74, 46.74) * mm});
            skLineSegment(sketch, "E371", {"start": v(-72.74, 46.74) * mm, "end": v(-72.3, 46.5) * mm});
            skLineSegment(sketch, "E372", {"start": v(-72.3, 46.5) * mm, "end": v(-71.89, 46.3) * mm});
            skLineSegment(sketch, "E373", {"start": v(-71.89, 46.3) * mm, "end": v(-71.48, 46.1) * mm});
            skLineSegment(sketch, "E374", {"start": v(-71.48, 46.1) * mm, "end": v(-71.1, 45.94) * mm});
            skLineSegment(sketch, "E375", {"start": v(-71.1, 45.94) * mm, "end": v(-70.74, 45.8) * mm});
            skLineSegment(sketch, "E376", {"start": v(-70.74, 45.8) * mm, "end": v(-70.4, 45.67) * mm});
            skLineSegment(sketch, "E377", {"start": v(-70.4, 45.67) * mm, "end": v(-70.07, 45.56) * mm});
            skLineSegment(sketch, "E378", {"start": v(-70.07, 45.56) * mm, "end": v(-69.77, 45.46) * mm});
            skLineSegment(sketch, "E379", {"start": v(-69.77, 45.46) * mm, "end": v(-69.5, 45.38) * mm});
            skLineSegment(sketch, "E380", {"start": v(-69.5, 45.38) * mm, "end": v(-69.24, 45.32) * mm});
            skLineSegment(sketch, "E381", {"start": v(-69.24, 45.32) * mm, "end": v(-69, 45.27) * mm});
            skLineSegment(sketch, "E382", {"start": v(-69, 45.27) * mm, "end": v(-68.8, 45.23) * mm});
            skLineSegment(sketch, "E383", {"start": v(-68.8, 45.23) * mm, "end": v(-68.62, 45.2) * mm});
            skLineSegment(sketch, "E384", {"start": v(-68.62, 45.2) * mm, "end": v(-68.46, 45.17) * mm});
            skLineSegment(sketch, "E385", {"start": v(-68.46, 45.17) * mm, "end": v(-68.33, 45.16) * mm});
            skLineSegment(sketch, "E386", {"start": v(-68.33, 45.16) * mm, "end": v(-68.22, 45.15) * mm});
            skLineSegment(sketch, "E387", {"start": v(-68.22, 45.15) * mm, "end": v(-68.14, 45.14) * mm});
            skLineSegment(sketch, "E388", {"start": v(-68.14, 45.14) * mm, "end": v(-68.08, 45.14) * mm});
            skLineSegment(sketch, "E389", {"start": v(-68.08, 45.14) * mm, "end": v(-68.05, 45.14) * mm});
            skLineSegment(sketch, "E390", {"start": v(-68.05, 45.14) * mm, "end": v(-63.6, 45.25) * mm});
            skLineSegment(sketch, "E391", {"start": v(-63.6, 45.25) * mm, "end": v(-62.69, 38.5) * mm});
            skLineSegment(sketch, "E392", {"start": v(-62.69, 38.5) * mm, "end": v(-67.02, 37.42) * mm});
            skLineSegment(sketch, "E393", {"start": v(-67.02, 37.42) * mm, "end": v(-67.05, 37.42) * mm});
            skLineSegment(sketch, "E394", {"start": v(-67.05, 37.42) * mm, "end": v(-67.1, 37.4) * mm});
            skLineSegment(sketch, "E395", {"start": v(-67.1, 37.4) * mm, "end": v(-67.18, 37.37) * mm});
            skLineSegment(sketch, "E396", {"start": v(-67.18, 37.37) * mm, "end": v(-67.28, 37.34) * mm});
            skLineSegment(sketch, "E397", {"start": v(-67.28, 37.34) * mm, "end": v(-67.4, 37.29) * mm});
            skLineSegment(sketch, "E398", {"start": v(-67.4, 37.29) * mm, "end": v(-67.55, 37.22) * mm});
            skLineSegment(sketch, "E399", {"start": v(-67.55, 37.22) * mm, "end": v(-67.72, 37.15) * mm});
            skLineSegment(sketch, "E400", {"start": v(-67.72, 37.15) * mm, "end": v(-67.9, 37.05) * mm});
            skLineSegment(sketch, "E401", {"start": v(-67.9, 37.05) * mm, "end": v(-68.11, 36.94) * mm});
            skLineSegment(sketch, "E402", {"start": v(-68.11, 36.94) * mm, "end": v(-68.34, 36.81) * mm});
            skLineSegment(sketch, "E403", {"start": v(-68.34, 36.81) * mm, "end": v(-68.6, 36.66) * mm});
            skLineSegment(sketch, "E404", {"start": v(-68.6, 36.66) * mm, "end": v(-68.86, 36.5) * mm});
            skLineSegment(sketch, "E405", {"start": v(-68.86, 36.5) * mm, "end": v(-69.14, 36.3) * mm});
            skLineSegment(sketch, "E406", {"start": v(-69.14, 36.3) * mm, "end": v(-69.44, 36.09) * mm});
            skLineSegment(sketch, "E407", {"start": v(-69.44, 36.09) * mm, "end": v(-69.75, 35.85) * mm});
            skLineSegment(sketch, "E408", {"start": v(-69.75, 35.85) * mm, "end": v(-70.08, 35.6) * mm});
            skLineSegment(sketch, "E409", {"start": v(-70.08, 35.6) * mm, "end": v(-70.41, 35.3) * mm});
            skLineSegment(sketch, "E410", {"start": v(-70.41, 35.3) * mm, "end": v(-70.76, 35) * mm});
            skLineSegment(sketch, "E411", {"start": v(-70.76, 35) * mm, "end": v(-71.13, 34.65) * mm});
            skLineSegment(sketch, "E412", {"start": v(-71.13, 34.65) * mm, "end": v(-71.5, 34.28) * mm});
            skLineSegment(sketch, "E413", {"start": v(-71.5, 34.28) * mm, "end": v(-71.87, 33.89) * mm});
            skLineSegment(sketch, "E414", {"start": v(-71.87, 33.89) * mm, "end": v(-72.26, 33.46) * mm});
            skLineSegment(sketch, "E415", {"start": v(-72.26, 33.46) * mm, "end": v(-72.65, 33) * mm});
            skLineSegment(sketch, "E416", {"start": v(-72.65, 33) * mm, "end": v(-73.04, 32.52) * mm});
            skLineSegment(sketch, "E417", {"start": v(-73.04, 32.52) * mm, "end": v(-73.44, 32) * mm});
            skLineSegment(sketch, "E418", {"start": v(-73.44, 32) * mm, "end": v(-73.77, 31.48) * mm});
            skLineSegment(sketch, "E419", {"start": v(-73.77, 31.48) * mm, "end": v(-72.53, 28.3) * mm});
            skLineSegment(sketch, "E420", {"start": v(-72.53, 28.3) * mm, "end": v(-71.92, 28.15) * mm});
            skLineSegment(sketch, "E421", {"start": v(-71.92, 28.15) * mm, "end": v(-71.28, 28.04) * mm});
            skLineSegment(sketch, "E422", {"start": v(-71.28, 28.04) * mm, "end": v(-70.66, 27.96) * mm});
            skLineSegment(sketch, "E423", {"start": v(-70.66, 27.96) * mm, "end": v(-70.07, 27.89) * mm});
            skLineSegment(sketch, "E424", {"start": v(-70.07, 27.89) * mm, "end": v(-69.5, 27.84) * mm});
            skLineSegment(sketch, "E425", {"start": v(-69.5, 27.84) * mm, "end": v(-68.95, 27.8) * mm});
            skLineSegment(sketch, "E426", {"start": v(-68.95, 27.8) * mm, "end": v(-68.43, 27.79) * mm});
            skLineSegment(sketch, "E427", {"start": v(-68.43, 27.79) * mm, "end": v(-67.93, 27.79) * mm});
            skLineSegment(sketch, "E428", {"start": v(-67.93, 27.79) * mm, "end": v(-67.46, 27.8) * mm});
            skLineSegment(sketch, "E429", {"start": v(-67.46, 27.8) * mm, "end": v(-67.02, 27.82) * mm});
            skLineSegment(sketch, "E430", {"start": v(-67.02, 27.82) * mm, "end": v(-66.6, 27.85) * mm});
            skLineSegment(sketch, "E431", {"start": v(-66.6, 27.85) * mm, "end": v(-66.2, 27.89) * mm});
            skLineSegment(sketch, "E432", {"start": v(-66.2, 27.89) * mm, "end": v(-65.85, 27.93) * mm});
            skLineSegment(sketch, "E433", {"start": v(-65.85, 27.93) * mm, "end": v(-65.5, 27.99) * mm});
            skLineSegment(sketch, "E434", {"start": v(-65.5, 27.99) * mm, "end": v(-65.2, 28.04) * mm});
            skLineSegment(sketch, "E435", {"start": v(-65.2, 28.04) * mm, "end": v(-64.92, 28.1) * mm});
            skLineSegment(sketch, "E436", {"start": v(-64.92, 28.1) * mm, "end": v(-64.66, 28.16) * mm});
            skLineSegment(sketch, "E437", {"start": v(-64.66, 28.16) * mm, "end": v(-64.43, 28.22) * mm});
            skLineSegment(sketch, "E438", {"start": v(-64.43, 28.22) * mm, "end": v(-64.23, 28.28) * mm});
            skLineSegment(sketch, "E439", {"start": v(-64.23, 28.28) * mm, "end": v(-64.06, 28.34) * mm});
            skLineSegment(sketch, "E440", {"start": v(-64.06, 28.34) * mm, "end": v(-63.9, 28.4) * mm});
            skLineSegment(sketch, "E441", {"start": v(-63.9, 28.4) * mm, "end": v(-63.78, 28.44) * mm});
            skLineSegment(sketch, "E442", {"start": v(-63.78, 28.44) * mm, "end": v(-63.68, 28.48) * mm});
            skLineSegment(sketch, "E443", {"start": v(-63.68, 28.48) * mm, "end": v(-63.6, 28.52) * mm});
            skLineSegment(sketch, "E444", {"start": v(-63.6, 28.52) * mm, "end": v(-63.56, 28.54) * mm});
            skLineSegment(sketch, "E445", {"start": v(-63.56, 28.54) * mm, "end": v(-63.53, 28.56) * mm});
            skLineSegment(sketch, "E446", {"start": v(-63.53, 28.56) * mm, "end": v(-59.63, 30.73) * mm});
            skLineSegment(sketch, "E447", {"start": v(-59.63, 30.73) * mm, "end": v(-55.69, 25.16) * mm});
            skLineSegment(sketch, "E448", {"start": v(-55.69, 25.16) * mm, "end": v(-59.03, 22.2) * mm});
            skLineSegment(sketch, "E449", {"start": v(-59.03, 22.2) * mm, "end": v(-59.05, 22.18) * mm});
            skLineSegment(sketch, "E450", {"start": v(-59.05, 22.18) * mm, "end": v(-59.1, 22.14) * mm});
            skLineSegment(sketch, "E451", {"start": v(-59.1, 22.14) * mm, "end": v(-59.15, 22.08) * mm});
            skLineSegment(sketch, "E452", {"start": v(-59.15, 22.08) * mm, "end": v(-59.22, 22) * mm});
            skLineSegment(sketch, "E453", {"start": v(-59.22, 22) * mm, "end": v(-59.3, 21.9) * mm});
            skLineSegment(sketch, "E454", {"start": v(-59.3, 21.9) * mm, "end": v(-59.4, 21.78) * mm});
            skLineSegment(sketch, "E455", {"start": v(-59.4, 21.78) * mm, "end": v(-59.52, 21.63) * mm});
            skLineSegment(sketch, "E456", {"start": v(-59.52, 21.63) * mm, "end": v(-59.64, 21.46) * mm});
            skLineSegment(sketch, "E457", {"start": v(-59.64, 21.46) * mm, "end": v(-59.78, 21.26) * mm});
            skLineSegment(sketch, "E458", {"start": v(-59.78, 21.26) * mm, "end": v(-59.92, 21.04) * mm});
            skLineSegment(sketch, "E459", {"start": v(-59.92, 21.04) * mm, "end": v(-60.07, 20.8) * mm});
            skLineSegment(sketch, "E460", {"start": v(-60.07, 20.8) * mm, "end": v(-60.22, 20.52) * mm});
            skLineSegment(sketch, "E461", {"start": v(-60.22, 20.52) * mm, "end": v(-60.39, 20.22) * mm});
            skLineSegment(sketch, "E462", {"start": v(-60.39, 20.22) * mm, "end": v(-60.55, 19.9) * mm});
            skLineSegment(sketch, "E463", {"start": v(-60.55, 19.9) * mm, "end": v(-60.72, 19.54) * mm});
            skLineSegment(sketch, "E464", {"start": v(-60.72, 19.54) * mm, "end": v(-60.88, 19.16) * mm});
            skLineSegment(sketch, "E465", {"start": v(-60.88, 19.16) * mm, "end": v(-61.05, 18.75) * mm});
            skLineSegment(sketch, "E466", {"start": v(-61.05, 18.75) * mm, "end": v(-61.22, 18.3) * mm});
            skLineSegment(sketch, "E467", {"start": v(-61.22, 18.3) * mm, "end": v(-61.38, 17.84) * mm});
            skLineSegment(sketch, "E468", {"start": v(-61.38, 17.84) * mm, "end": v(-61.53, 17.34) * mm});
            skLineSegment(sketch, "E469", {"start": v(-61.53, 17.34) * mm, "end": v(-61.68, 16.81) * mm});
            skLineSegment(sketch, "E470", {"start": v(-61.68, 16.81) * mm, "end": v(-61.83, 16.26) * mm});
            skLineSegment(sketch, "E471", {"start": v(-61.83, 16.26) * mm, "end": v(-61.96, 15.67) * mm});
            skLineSegment(sketch, "E472", {"start": v(-61.96, 15.67) * mm, "end": v(-62.08, 15.06) * mm});
            skLineSegment(sketch, "E473", {"start": v(-62.08, 15.06) * mm, "end": v(-62.2, 14.42) * mm});
            skLineSegment(sketch, "E474", {"start": v(-62.2, 14.42) * mm, "end": v(-62.25, 13.8) * mm});
            skLineSegment(sketch, "E475", {"start": v(-62.25, 13.8) * mm, "end": v(-59.67, 11.57) * mm});
            skLineSegment(sketch, "E476", {"start": v(-59.67, 11.57) * mm, "end": v(-59.06, 11.71) * mm});
            skLineSegment(sketch, "E477", {"start": v(-59.06, 11.71) * mm, "end": v(-58.44, 11.92) * mm});
            skLineSegment(sketch, "E478", {"start": v(-58.44, 11.92) * mm, "end": v(-57.85, 12.13) * mm});
            skLineSegment(sketch, "E479", {"start": v(-57.85, 12.13) * mm, "end": v(-57.3, 12.34) * mm});
            skLineSegment(sketch, "E480", {"start": v(-57.3, 12.34) * mm, "end": v(-56.77, 12.56) * mm});
            skLineSegment(sketch, "E481", {"start": v(-56.77, 12.56) * mm, "end": v(-56.27, 12.79) * mm});
            skLineSegment(sketch, "E482", {"start": v(-56.27, 12.79) * mm, "end": v(-55.8, 13.02) * mm});
            skLineSegment(sketch, "E483", {"start": v(-55.8, 13.02) * mm, "end": v(-55.36, 13.24) * mm});
            skLineSegment(sketch, "E484", {"start": v(-55.36, 13.24) * mm, "end": v(-54.95, 13.47) * mm});
            skLineSegment(sketch, "E485", {"start": v(-54.95, 13.47) * mm, "end": v(-54.56, 13.7) * mm});
            skLineSegment(sketch, "E486", {"start": v(-54.56, 13.7) * mm, "end": v(-54.2, 13.92) * mm});
            skLineSegment(sketch, "E487", {"start": v(-54.2, 13.92) * mm, "end": v(-53.88, 14.13) * mm});
            skLineSegment(sketch, "E488", {"start": v(-53.88, 14.13) * mm, "end": v(-53.58, 14.34) * mm});
            skLineSegment(sketch, "E489", {"start": v(-53.58, 14.34) * mm, "end": v(-53.3, 14.55) * mm});
            skLineSegment(sketch, "E490", {"start": v(-53.3, 14.55) * mm, "end": v(-53.06, 14.74) * mm});
            skLineSegment(sketch, "E491", {"start": v(-53.06, 14.74) * mm, "end": v(-52.84, 14.92) * mm});
            skLineSegment(sketch, "E492", {"start": v(-52.84, 14.92) * mm, "end": v(-52.64, 15.1) * mm});
            skLineSegment(sketch, "E493", {"start": v(-52.64, 15.1) * mm, "end": v(-52.46, 15.26) * mm});
            skLineSegment(sketch, "E494", {"start": v(-52.46, 15.26) * mm, "end": v(-52.31, 15.4) * mm});
            skLineSegment(sketch, "E495", {"start": v(-52.31, 15.4) * mm, "end": v(-52.18, 15.54) * mm});
            skLineSegment(sketch, "E496", {"start": v(-52.18, 15.54) * mm, "end": v(-52.08, 15.65) * mm});
            skLineSegment(sketch, "E497", {"start": v(-52.08, 15.65) * mm, "end": v(-51.99, 15.75) * mm});
            skLineSegment(sketch, "E498", {"start": v(-51.99, 15.75) * mm, "end": v(-51.92, 15.84) * mm});
            skLineSegment(sketch, "E499", {"start": v(-51.92, 15.84) * mm, "end": v(-51.87, 15.9) * mm});
            skLineSegment(sketch, "E500", {"start": v(-51.87, 15.9) * mm, "end": v(-51.84, 15.95) * mm});
            skLineSegment(sketch, "E501", {"start": v(-51.84, 15.95) * mm, "end": v(-51.82, 15.97) * mm});
            skLineSegment(sketch, "E502", {"start": v(-51.82, 15.97) * mm, "end": v(-49.37, 19.7) * mm});
            skLineSegment(sketch, "E503", {"start": v(-49.37, 19.7) * mm, "end": v(-43.3, 16.6) * mm});
            skLineSegment(sketch, "E504", {"start": v(-43.3, 16.6) * mm, "end": v(-44.88, 12.44) * mm});
            skLineSegment(sketch, "E505", {"start": v(-44.88, 12.44) * mm, "end": v(-44.9, 12.4) * mm});
            skLineSegment(sketch, "E506", {"start": v(-44.9, 12.4) * mm, "end": v(-44.9, 12.35) * mm});
            skLineSegment(sketch, "E507", {"start": v(-44.9, 12.35) * mm, "end": v(-44.93, 12.28) * mm});
            skLineSegment(sketch, "E508", {"start": v(-44.93, 12.28) * mm, "end": v(-44.96, 12.17) * mm});
            skLineSegment(sketch, "E509", {"start": v(-44.96, 12.17) * mm, "end": v(-44.99, 12.04) * mm});
            skLineSegment(sketch, "E510", {"start": v(-44.99, 12.04) * mm, "end": v(-45.02, 11.89) * mm});
            skLineSegment(sketch, "E511", {"start": v(-45.02, 11.89) * mm, "end": v(-45.05, 11.7) * mm});
            skLineSegment(sketch, "E512", {"start": v(-45.05, 11.7) * mm, "end": v(-45.08, 11.5) * mm});
            skLineSegment(sketch, "E513", {"start": v(-45.08, 11.5) * mm, "end": v(-45.1, 11.26) * mm});
            skLineSegment(sketch, "E514", {"start": v(-45.1, 11.26) * mm, "end": v(-45.13, 11) * mm});
            skLineSegment(sketch, "E515", {"start": v(-45.13, 11) * mm, "end": v(-45.15, 10.7) * mm});
            skLineSegment(sketch, "E516", {"start": v(-45.15, 10.7) * mm, "end": v(-45.16, 10.4) * mm});
            skLineSegment(sketch, "E517", {"start": v(-45.16, 10.4) * mm, "end": v(-45.16, 10.05) * mm});
            skLineSegment(sketch, "E518", {"start": v(-45.16, 10.05) * mm, "end": v(-45.16, 9.69) * mm});
            skLineSegment(sketch, "E519", {"start": v(-45.16, 9.69) * mm, "end": v(-45.14, 9.3) * mm});
            skLineSegment(sketch, "E520", {"start": v(-45.14, 9.3) * mm, "end": v(-45.1, 8.88) * mm});
            skLineSegment(sketch, "E521", {"start": v(-45.1, 8.88) * mm, "end": v(-45.07, 8.44) * mm});
            skLineSegment(sketch, "E522", {"start": v(-45.07, 8.44) * mm, "end": v(-45, 7.97) * mm});
            skLineSegment(sketch, "E523", {"start": v(-45, 7.97) * mm, "end": v(-44.93, 7.48) * mm});
            skLineSegment(sketch, "E524", {"start": v(-44.93, 7.48) * mm, "end": v(-44.84, 6.97) * mm});
            skLineSegment(sketch, "E525", {"start": v(-44.84, 6.97) * mm, "end": v(-44.73, 6.43) * mm});
            skLineSegment(sketch, "E526", {"start": v(-44.73, 6.43) * mm, "end": v(-44.6, 5.87) * mm});
            skLineSegment(sketch, "E527", {"start": v(-44.6, 5.87) * mm, "end": v(-44.44, 5.3) * mm});
            skLineSegment(sketch, "E528", {"start": v(-44.44, 5.3) * mm, "end": v(-44.26, 4.7) * mm});
            skLineSegment(sketch, "E529", {"start": v(-44.26, 4.7) * mm, "end": v(-44.06, 4.07) * mm});
            skLineSegment(sketch, "E530", {"start": v(-44.06, 4.07) * mm, "end": v(-43.82, 3.5) * mm});
            skLineSegment(sketch, "E531", {"start": v(-43.82, 3.5) * mm, "end": v(-40.5, 2.72) * mm});
            skLineSegment(sketch, "E532", {"start": v(-40.5, 2.72) * mm, "end": v(-40.04, 3.13) * mm});
            skLineSegment(sketch, "E533", {"start": v(-40.04, 3.13) * mm, "end": v(-39.58, 3.6) * mm});
            skLineSegment(sketch, "E534", {"start": v(-39.58, 3.6) * mm, "end": v(-39.16, 4.06) * mm});
            skLineSegment(sketch, "E535", {"start": v(-39.16, 4.06) * mm, "end": v(-38.76, 4.51) * mm});
            skLineSegment(sketch, "E536", {"start": v(-38.76, 4.51) * mm, "end": v(-38.4, 4.95) * mm});
            skLineSegment(sketch, "E537", {"start": v(-38.4, 4.95) * mm, "end": v(-38.06, 5.38) * mm});
            skLineSegment(sketch, "E538", {"start": v(-38.06, 5.38) * mm, "end": v(-37.75, 5.8) * mm});
            skLineSegment(sketch, "E539", {"start": v(-37.75, 5.8) * mm, "end": v(-37.47, 6.21) * mm});
            skLineSegment(sketch, "E540", {"start": v(-37.47, 6.21) * mm, "end": v(-37.2, 6.6) * mm});
            skLineSegment(sketch, "E541", {"start": v(-37.2, 6.6) * mm, "end": v(-36.97, 6.98) * mm});
            skLineSegment(sketch, "E542", {"start": v(-36.97, 6.98) * mm, "end": v(-36.76, 7.34) * mm});
            skLineSegment(sketch, "E543", {"start": v(-36.76, 7.34) * mm, "end": v(-36.57, 7.68) * mm});
            skLineSegment(sketch, "E544", {"start": v(-36.57, 7.68) * mm, "end": v(-36.4, 8) * mm});
            skLineSegment(sketch, "E545", {"start": v(-36.4, 8) * mm, "end": v(-36.26, 8.32) * mm});
            skLineSegment(sketch, "E546", {"start": v(-36.26, 8.32) * mm, "end": v(-36.13, 8.6) * mm});
            skLineSegment(sketch, "E547", {"start": v(-36.13, 8.6) * mm, "end": v(-36.01, 8.87) * mm});
            skLineSegment(sketch, "E548", {"start": v(-36.01, 8.87) * mm, "end": v(-35.92, 9.11) * mm});
            skLineSegment(sketch, "E549", {"start": v(-35.92, 9.11) * mm, "end": v(-35.84, 9.34) * mm});
            skLineSegment(sketch, "E550", {"start": v(-35.84, 9.34) * mm, "end": v(-35.78, 9.54) * mm});
            skLineSegment(sketch, "E551", {"start": v(-35.78, 9.54) * mm, "end": v(-35.72, 9.72) * mm});
            skLineSegment(sketch, "E552", {"start": v(-35.72, 9.72) * mm, "end": v(-35.68, 9.87) * mm});
            skLineSegment(sketch, "E553", {"start": v(-35.68, 9.87) * mm, "end": v(-35.65, 10) * mm});
            skLineSegment(sketch, "E554", {"start": v(-35.65, 10) * mm, "end": v(-35.63, 10.1) * mm});
            skLineSegment(sketch, "E555", {"start": v(-35.63, 10.1) * mm, "end": v(-35.61, 10.18) * mm});
            skLineSegment(sketch, "E556", {"start": v(-35.61, 10.18) * mm, "end": v(-35.6, 10.24) * mm});
            skLineSegment(sketch, "E557", {"start": v(-35.6, 10.24) * mm, "end": v(-35.6, 10.27) * mm});
            skLineSegment(sketch, "E558", {"start": v(-35.6, 10.27) * mm, "end": v(-35.17, 14.71) * mm});
            skLineSegment(sketch, "E559", {"start": v(-35.17, 14.71) * mm, "end": v(-28.35, 14.8) * mm});
            skLineSegment(sketch, "E560", {"start": v(-28.35, 14.8) * mm, "end": v(-27.81, 10.36) * mm});
            skLineSegment(sketch, "E561", {"start": v(-27.81, 10.36) * mm, "end": v(-27.81, 10.33) * mm});
            skLineSegment(sketch, "E562", {"start": v(-27.81, 10.33) * mm, "end": v(-27.8, 10.28) * mm});
            skLineSegment(sketch, "E563", {"start": v(-27.8, 10.28) * mm, "end": v(-27.78, 10.2) * mm});
            skLineSegment(sketch, "E564", {"start": v(-27.78, 10.2) * mm, "end": v(-27.76, 10.1) * mm});
            skLineSegment(sketch, "E565", {"start": v(-27.76, 10.1) * mm, "end": v(-27.72, 9.97) * mm});
            skLineSegment(sketch, "E566", {"start": v(-27.72, 9.97) * mm, "end": v(-27.68, 9.81) * mm});
            skLineSegment(sketch, "E567", {"start": v(-27.68, 9.81) * mm, "end": v(-27.62, 9.64) * mm});
            skLineSegment(sketch, "E568", {"start": v(-27.62, 9.64) * mm, "end": v(-27.55, 9.44) * mm});
            skLineSegment(sketch, "E569", {"start": v(-27.55, 9.44) * mm, "end": v(-27.47, 9.22) * mm});
            skLineSegment(sketch, "E570", {"start": v(-27.47, 9.22) * mm, "end": v(-27.37, 8.97) * mm});
            skLineSegment(sketch, "E571", {"start": v(-27.37, 8.97) * mm, "end": v(-27.25, 8.71) * mm});
            skLineSegment(sketch, "E572", {"start": v(-27.25, 8.71) * mm, "end": v(-27.11, 8.43) * mm});
            skLineSegment(sketch, "E573", {"start": v(-27.11, 8.43) * mm, "end": v(-26.96, 8.12) * mm});
            skLineSegment(sketch, "E574", {"start": v(-26.96, 8.12) * mm, "end": v(-26.78, 7.8) * mm});
            skLineSegment(sketch, "E575", {"start": v(-26.78, 7.8) * mm, "end": v(-26.58, 7.46) * mm});
            skLineSegment(sketch, "E576", {"start": v(-26.58, 7.46) * mm, "end": v(-26.36, 7.1) * mm});
            skLineSegment(sketch, "E577", {"start": v(-26.36, 7.1) * mm, "end": v(-26.12, 6.74) * mm});
            skLineSegment(sketch, "E578", {"start": v(-26.12, 6.74) * mm, "end": v(-25.85, 6.35) * mm});
            skLineSegment(sketch, "E579", {"start": v(-25.85, 6.35) * mm, "end": v(-25.56, 5.95) * mm});
            skLineSegment(sketch, "E580", {"start": v(-25.56, 5.95) * mm, "end": v(-25.24, 5.54) * mm});
            skLineSegment(sketch, "E581", {"start": v(-25.24, 5.54) * mm, "end": v(-24.89, 5.12) * mm});
            skLineSegment(sketch, "E582", {"start": v(-24.89, 5.12) * mm, "end": v(-24.51, 4.69) * mm});
            skLineSegment(sketch, "E583", {"start": v(-24.51, 4.69) * mm, "end": v(-24.1, 4.24) * mm});
            skLineSegment(sketch, "E584", {"start": v(-24.1, 4.24) * mm, "end": v(-23.67, 3.8) * mm});
            skLineSegment(sketch, "E585", {"start": v(-23.67, 3.8) * mm, "end": v(-23.2, 3.34) * mm});
            skLineSegment(sketch, "E586", {"start": v(-23.2, 3.34) * mm, "end": v(-22.72, 2.94) * mm});
            skLineSegment(sketch, "E587", {"start": v(-22.72, 2.94) * mm, "end": v(-19.43, 3.8) * mm});
            skLineSegment(sketch, "E588", {"start": v(-19.43, 3.8) * mm, "end": v(-19.2, 4.38) * mm});
            skLineSegment(sketch, "E589", {"start": v(-19.2, 4.38) * mm, "end": v(-19.02, 5) * mm});
            skLineSegment(sketch, "E590", {"start": v(-19.02, 5) * mm, "end": v(-18.86, 5.6) * mm});
            skLineSegment(sketch, "E591", {"start": v(-18.86, 5.6) * mm, "end": v(-18.72, 6.2) * mm});
            skLineSegment(sketch, "E592", {"start": v(-18.72, 6.2) * mm, "end": v(-18.6, 6.75) * mm});
            skLineSegment(sketch, "E593", {"start": v(-18.6, 6.75) * mm, "end": v(-18.5, 7.29) * mm});
            skLineSegment(sketch, "E594", {"start": v(-18.5, 7.29) * mm, "end": v(-18.42, 7.8) * mm});
            skLineSegment(sketch, "E595", {"start": v(-18.42, 7.8) * mm, "end": v(-18.36, 8.3) * mm});
            skLineSegment(sketch, "E596", {"start": v(-18.36, 8.3) * mm, "end": v(-18.3, 8.76) * mm});
            skLineSegment(sketch, "E597", {"start": v(-18.3, 8.76) * mm, "end": v(-18.28, 9.2) * mm});
            skLineSegment(sketch, "E598", {"start": v(-18.28, 9.2) * mm, "end": v(-18.26, 9.63) * mm});
            skLineSegment(sketch, "E599", {"start": v(-18.26, 9.63) * mm, "end": v(-18.25, 10.02) * mm});
            skLineSegment(sketch, "E600", {"start": v(-18.25, 10.02) * mm, "end": v(-18.25, 10.38) * mm});
            skLineSegment(sketch, "E601", {"start": v(-18.25, 10.38) * mm, "end": v(-18.26, 10.72) * mm});
            skLineSegment(sketch, "E602", {"start": v(-18.26, 10.72) * mm, "end": v(-18.28, 11.04) * mm});
            skLineSegment(sketch, "E603", {"start": v(-18.28, 11.04) * mm, "end": v(-18.3, 11.33) * mm});
            skLineSegment(sketch, "E604", {"start": v(-18.3, 11.33) * mm, "end": v(-18.34, 11.59) * mm});
            skLineSegment(sketch, "E605", {"start": v(-18.34, 11.59) * mm, "end": v(-18.37, 11.82) * mm});
            skLineSegment(sketch, "E606", {"start": v(-18.37, 11.82) * mm, "end": v(-18.4, 12.03) * mm});
            skLineSegment(sketch, "E607", {"start": v(-18.4, 12.03) * mm, "end": v(-18.44, 12.21) * mm});
            skLineSegment(sketch, "E608", {"start": v(-18.44, 12.21) * mm, "end": v(-18.48, 12.37) * mm});
            skLineSegment(sketch, "E609", {"start": v(-18.48, 12.37) * mm, "end": v(-18.5, 12.5) * mm});
            skLineSegment(sketch, "E610", {"start": v(-18.5, 12.5) * mm, "end": v(-18.54, 12.6) * mm});
            skLineSegment(sketch, "E611", {"start": v(-18.54, 12.6) * mm, "end": v(-18.56, 12.68) * mm});
            skLineSegment(sketch, "E612", {"start": v(-18.56, 12.68) * mm, "end": v(-18.58, 12.73) * mm});
            skLineSegment(sketch, "E613", {"start": v(-18.58, 12.73) * mm, "end": v(-18.6, 12.76) * mm});
            skLineSegment(sketch, "E614", {"start": v(-18.6, 12.76) * mm, "end": v(-20.27, 16.9) * mm});
            skLineSegment(sketch, "E615", {"start": v(-20.27, 16.9) * mm, "end": v(-14.28, 20.13) * mm});
            skLineSegment(sketch, "E616", {"start": v(-14.28, 20.13) * mm, "end": v(-11.74, 16.46) * mm});
            skLineSegment(sketch, "E617", {"start": v(-11.74, 16.46) * mm, "end": v(-11.72, 16.44) * mm});
            skLineSegment(sketch, "E618", {"start": v(-11.72, 16.44) * mm, "end": v(-11.69, 16.4) * mm});
            skLineSegment(sketch, "E619", {"start": v(-11.69, 16.4) * mm, "end": v(-11.64, 16.33) * mm});
            skLineSegment(sketch, "E620", {"start": v(-11.64, 16.33) * mm, "end": v(-11.57, 16.25) * mm});
            skLineSegment(sketch, "E621", {"start": v(-11.57, 16.25) * mm, "end": v(-11.48, 16.15) * mm});
            skLineSegment(sketch, "E622", {"start": v(-11.48, 16.15) * mm, "end": v(-11.36, 16.04) * mm});
            skLineSegment(sketch, "E623", {"start": v(-11.36, 16.04) * mm, "end": v(-11.23, 15.9) * mm});
            skLineSegment(sketch, "E624", {"start": v(-11.23, 15.9) * mm, "end": v(-11.08, 15.76) * mm});
            skLineSegment(sketch, "E625", {"start": v(-11.08, 15.76) * mm, "end": v(-10.9, 15.6) * mm});
            skLineSegment(sketch, "E626", {"start": v(-10.9, 15.6) * mm, "end": v(-10.7, 15.44) * mm});
            skLineSegment(sketch, "E627", {"start": v(-10.7, 15.44) * mm, "end": v(-10.47, 15.26) * mm});
            skLineSegment(sketch, "E628", {"start": v(-10.47, 15.26) * mm, "end": v(-10.22, 15.07) * mm});
            skLineSegment(sketch, "E629", {"start": v(-10.22, 15.07) * mm, "end": v(-9.94, 14.88) * mm});
            skLineSegment(sketch, "E630", {"start": v(-9.94, 14.88) * mm, "end": v(-9.64, 14.67) * mm});
            skLineSegment(sketch, "E631", {"start": v(-9.64, 14.67) * mm, "end": v(-9.3, 14.47) * mm});
            skLineSegment(sketch, "E632", {"start": v(-9.3, 14.47) * mm, "end": v(-8.94, 14.25) * mm});
            skLineSegment(sketch, "E633", {"start": v(-8.94, 14.25) * mm, "end": v(-8.55, 14.04) * mm});
            skLineSegment(sketch, "E634", {"start": v(-8.55, 14.04) * mm, "end": v(-8.14, 13.82) * mm});
            skLineSegment(sketch, "E635", {"start": v(-8.14, 13.82) * mm, "end": v(-7.7, 13.6) * mm});
            skLineSegment(sketch, "E636", {"start": v(-7.7, 13.6) * mm, "end": v(-7.22, 13.39) * mm});
            skLineSegment(sketch, "E637", {"start": v(-7.22, 13.39) * mm, "end": v(-6.71, 13.18) * mm});
            skLineSegment(sketch, "E638", {"start": v(-6.71, 13.18) * mm, "end": v(-6.18, 12.97) * mm});
            skLineSegment(sketch, "E639", {"start": v(-6.18, 12.97) * mm, "end": v(-5.61, 12.77) * mm});
            skLineSegment(sketch, "E640", {"start": v(-5.61, 12.77) * mm, "end": v(-5.02, 12.57) * mm});
            skLineSegment(sketch, "E641", {"start": v(-5.02, 12.57) * mm, "end": v(-4.4, 12.38) * mm});
            skLineSegment(sketch, "E642", {"start": v(-4.4, 12.38) * mm, "end": v(-3.78, 12.25) * mm});
            skLineSegment(sketch, "E643", {"start": v(-3.78, 12.25) * mm, "end": v(-1.26, 14.54) * mm});
            skLineSegment(sketch, "E644", {"start": v(-1.26, 14.54) * mm, "end": v(-1.33, 15.16) * mm});
            skLineSegment(sketch, "E645", {"start": v(-1.33, 15.16) * mm, "end": v(-1.46, 15.8) * mm});
            skLineSegment(sketch, "E646", {"start": v(-1.46, 15.8) * mm, "end": v(-1.6, 16.41) * mm});
            skLineSegment(sketch, "E647", {"start": v(-1.6, 16.41) * mm, "end": v(-1.74, 17) * mm});
            skLineSegment(sketch, "E648", {"start": v(-1.74, 17) * mm, "end": v(-1.9, 17.54) * mm});
            skLineSegment(sketch, "E649", {"start": v(-1.9, 17.54) * mm, "end": v(-2.06, 18.07) * mm});
            skLineSegment(sketch, "E650", {"start": v(-2.06, 18.07) * mm, "end": v(-2.23, 18.56) * mm});
            skLineSegment(sketch, "E651", {"start": v(-2.23, 18.56) * mm, "end": v(-2.4, 19.03) * mm});
            skLineSegment(sketch, "E652", {"start": v(-2.4, 19.03) * mm, "end": v(-2.58, 19.46) * mm});
            skLineSegment(sketch, "E653", {"start": v(-2.58, 19.46) * mm, "end": v(-2.76, 19.87) * mm});
            skLineSegment(sketch, "E654", {"start": v(-2.76, 19.87) * mm, "end": v(-2.93, 20.25) * mm});
            skLineSegment(sketch, "E655", {"start": v(-2.93, 20.25) * mm, "end": v(-3.1, 20.6) * mm});
            skLineSegment(sketch, "E656", {"start": v(-3.1, 20.6) * mm, "end": v(-3.28, 20.92) * mm});
            skLineSegment(sketch, "E657", {"start": v(-3.28, 20.92) * mm, "end": v(-3.45, 21.22) * mm});
            skLineSegment(sketch, "E658", {"start": v(-3.45, 21.22) * mm, "end": v(-3.61, 21.49) * mm});
            skLineSegment(sketch, "E659", {"start": v(-3.61, 21.49) * mm, "end": v(-3.77, 21.73) * mm});
            skLineSegment(sketch, "E660", {"start": v(-3.77, 21.73) * mm, "end": v(-3.92, 21.95) * mm});
            skLineSegment(sketch, "E661", {"start": v(-3.92, 21.95) * mm, "end": v(-4.05, 22.14) * mm});
            skLineSegment(sketch, "E662", {"start": v(-4.05, 22.14) * mm, "end": v(-4.18, 22.3) * mm});
            skLineSegment(sketch, "E663", {"start": v(-4.18, 22.3) * mm, "end": v(-4.3, 22.45) * mm});
            skLineSegment(sketch, "E664", {"start": v(-4.3, 22.45) * mm, "end": v(-4.4, 22.57) * mm});
            skLineSegment(sketch, "E665", {"start": v(-4.4, 22.57) * mm, "end": v(-4.5, 22.67) * mm});
            skLineSegment(sketch, "E666", {"start": v(-4.5, 22.67) * mm, "end": v(-4.56, 22.75) * mm});
            skLineSegment(sketch, "E667", {"start": v(-4.56, 22.75) * mm, "end": v(-4.62, 22.8) * mm});
            skLineSegment(sketch, "E668", {"start": v(-4.62, 22.8) * mm, "end": v(-4.66, 22.85) * mm});
            skLineSegment(sketch, "E669", {"start": v(-4.66, 22.85) * mm, "end": v(-4.68, 22.87) * mm});
            skLineSegment(sketch, "E670", {"start": v(-4.68, 22.87) * mm, "end": v(-8.1, 25.74) * mm});
            skLineSegment(sketch, "E671", {"start": v(-8.1, 25.74) * mm, "end": v(-4.3, 31.4) * mm});
            skLineSegment(sketch, "E672", {"start": v(-4.3, 31.4) * mm, "end": v(-0.34, 29.33) * mm});
            skLineSegment(sketch, "E673", {"start": v(-0.34, 29.33) * mm, "end": v(-0.31, 29.32) * mm});
            skLineSegment(sketch, "E674", {"start": v(-0.31, 29.32) * mm, "end": v(-0.26, 29.3) * mm});
            skLineSegment(sketch, "E675", {"start": v(-0.26, 29.3) * mm, "end": v(-0.19, 29.26) * mm});
            skLineSegment(sketch, "E676", {"start": v(-0.19, 29.26) * mm, "end": v(-0.09, 29.22) * mm});
            skLineSegment(sketch, "E677", {"start": v(-0.09, 29.22) * mm, "end": v(0.04, 29.18) * mm});
            skLineSegment(sketch, "E678", {"start": v(0.04, 29.18) * mm, "end": v(0.19, 29.13) * mm});
            skLineSegment(sketch, "E679", {"start": v(0.19, 29.13) * mm, "end": v(0.37, 29.07) * mm});
            skLineSegment(sketch, "E680", {"start": v(0.37, 29.07) * mm, "end": v(0.57, 29.02) * mm});
            skLineSegment(sketch, "E681", {"start": v(0.57, 29.02) * mm, "end": v(0.8, 28.96) * mm});
            skLineSegment(sketch, "E682", {"start": v(0.8, 28.96) * mm, "end": v(1.06, 28.9) * mm});
            skLineSegment(sketch, "E683", {"start": v(1.06, 28.9) * mm, "end": v(1.34, 28.86) * mm});
            skLineSegment(sketch, "E684", {"start": v(1.34, 28.86) * mm, "end": v(1.65, 28.8) * mm});
            skLineSegment(sketch, "E685", {"start": v(1.65, 28.8) * mm, "end": v(1.99, 28.76) * mm});
            skLineSegment(sketch, "E686", {"start": v(1.99, 28.76) * mm, "end": v(2.35, 28.72) * mm});
            skLineSegment(sketch, "E687", {"start": v(2.35, 28.72) * mm, "end": v(2.75, 28.7) * mm});
            skLineSegment(sketch, "E688", {"start": v(2.75, 28.7) * mm, "end": v(3.16, 28.67) * mm});
            skLineSegment(sketch, "E689", {"start": v(3.16, 28.67) * mm, "end": v(3.6, 28.66) * mm});
            skLineSegment(sketch, "E690", {"start": v(3.6, 28.66) * mm, "end": v(4.08, 28.67) * mm});
            skLineSegment(sketch, "E691", {"start": v(4.08, 28.67) * mm, "end": v(4.57, 28.68) * mm});
            skLineSegment(sketch, "E692", {"start": v(4.57, 28.68) * mm, "end": v(5.1, 28.71) * mm});
            skLineSegment(sketch, "E693", {"start": v(5.1, 28.71) * mm, "end": v(5.64, 28.76) * mm});
            skLineSegment(sketch, "E694", {"start": v(5.64, 28.76) * mm, "end": v(6.2, 28.82) * mm});
            skLineSegment(sketch, "E695", {"start": v(6.2, 28.82) * mm, "end": v(6.8, 28.9) * mm});
            skLineSegment(sketch, "E696", {"start": v(6.8, 28.9) * mm, "end": v(7.42, 29) * mm});
            skLineSegment(sketch, "E697", {"start": v(7.42, 29) * mm, "end": v(8.06, 29.13) * mm});
            skLineSegment(sketch, "E698", {"start": v(8.06, 29.13) * mm, "end": v(8.66, 29.3) * mm});
            skLineSegment(sketch, "E699", {"start": v(8.66, 29.3) * mm, "end": v(9.83, 32.5) * mm});
            skLineSegment(sketch, "E700", {"start": v(9.83, 32.5) * mm, "end": v(9.48, 33.02) * mm});
            skLineSegment(sketch, "E701", {"start": v(9.48, 33.02) * mm, "end": v(9.07, 33.52) * mm});
            skLineSegment(sketch, "E702", {"start": v(9.07, 33.52) * mm, "end": v(8.66, 34) * mm});
            skLineSegment(sketch, "E703", {"start": v(8.66, 34) * mm, "end": v(8.26, 34.45) * mm});
            skLineSegment(sketch, "E704", {"start": v(8.26, 34.45) * mm, "end": v(7.87, 34.86) * mm});
            skLineSegment(sketch, "E705", {"start": v(7.87, 34.86) * mm, "end": v(7.48, 35.25) * mm});
            skLineSegment(sketch, "E706", {"start": v(7.48, 35.25) * mm, "end": v(7.1, 35.6) * mm});
            skLineSegment(sketch, "E707", {"start": v(7.1, 35.6) * mm, "end": v(6.73, 35.94) * mm});
            skLineSegment(sketch, "E708", {"start": v(6.73, 35.94) * mm, "end": v(6.38, 36.24) * mm});
            skLineSegment(sketch, "E709", {"start": v(6.38, 36.24) * mm, "end": v(6.03, 36.52) * mm});
            skLineSegment(sketch, "E710", {"start": v(6.03, 36.52) * mm, "end": v(5.7, 36.78) * mm});
            skLineSegment(sketch, "E711", {"start": v(5.7, 36.78) * mm, "end": v(5.38, 37) * mm});
            skLineSegment(sketch, "E712", {"start": v(5.38, 37) * mm, "end": v(5.08, 37.21) * mm});
            skLineSegment(sketch, "E713", {"start": v(5.08, 37.21) * mm, "end": v(4.79, 37.4) * mm});
            skLineSegment(sketch, "E714", {"start": v(4.79, 37.4) * mm, "end": v(4.52, 37.56) * mm});
            skLineSegment(sketch, "E715", {"start": v(4.52, 37.56) * mm, "end": v(4.27, 37.7) * mm});
            skLineSegment(sketch, "E716", {"start": v(4.27, 37.7) * mm, "end": v(4.04, 37.82) * mm});
            skLineSegment(sketch, "E717", {"start": v(4.04, 37.82) * mm, "end": v(3.83, 37.93) * mm});
            skLineSegment(sketch, "E718", {"start": v(3.83, 37.93) * mm, "end": v(3.63, 38.02) * mm});
            skLineSegment(sketch, "E719", {"start": v(3.63, 38.02) * mm, "end": v(3.46, 38.1) * mm});
            skLineSegment(sketch, "E720", {"start": v(3.46, 38.1) * mm, "end": v(3.32, 38.15) * mm});
            skLineSegment(sketch, "E721", {"start": v(3.32, 38.15) * mm, "end": v(3.2, 38.2) * mm});
            skLineSegment(sketch, "E722", {"start": v(3.2, 38.2) * mm, "end": v(3.1, 38.23) * mm});
            skLineSegment(sketch, "E723", {"start": v(3.1, 38.23) * mm, "end": v(3.01, 38.26) * mm});
            skLineSegment(sketch, "E724", {"start": v(3.01, 38.26) * mm, "end": v(2.96, 38.27) * mm});
            skLineSegment(sketch, "E725", {"start": v(2.96, 38.27) * mm, "end": v(2.93, 38.28) * mm});
            skLineSegment(sketch, "E726", {"start": v(2.93, 38.28) * mm, "end": v(-1.43, 39.24) * mm});
            skLineSegment(sketch, "E727", {"start": v(-1.43, 39.24) * mm, "end": v(-0.69, 46.02) * mm});
            skLineSegment(sketch, "E728", {"start": v(-28.62, 46.02) * mm, "end": v(-35.67, 46.02) * mm});
            skLineSegment(sketch, "E729", {"start": v(-32.14, 42.5) * mm, "end": v(-32.14, 49.55) * mm});
            skLineSegment(sketch, "E730", {"start": v(63.64, -31.36) * mm, "end": v(67.21, -31.36) * mm});
            skLineSegment(sketch, "E731", {"start": v(67.21, -31.36) * mm, "end": v(67.24, -31.36) * mm});
            skLineSegment(sketch, "E732", {"start": v(67.24, -31.36) * mm, "end": v(67.29, -31.36) * mm});
            skLineSegment(sketch, "E733", {"start": v(67.29, -31.36) * mm, "end": v(67.35, -31.36) * mm});
            skLineSegment(sketch, "E734", {"start": v(67.35, -31.36) * mm, "end": v(67.43, -31.35) * mm});
            skLineSegment(sketch, "E735", {"start": v(67.43, -31.35) * mm, "end": v(67.53, -31.34) * mm});
            skLineSegment(sketch, "E736", {"start": v(67.53, -31.34) * mm, "end": v(67.65, -31.32) * mm});
            skLineSegment(sketch, "E737", {"start": v(67.65, -31.32) * mm, "end": v(67.79, -31.3) * mm});
            skLineSegment(sketch, "E738", {"start": v(67.79, -31.3) * mm, "end": v(67.94, -31.28) * mm});
            skLineSegment(sketch, "E739", {"start": v(67.94, -31.28) * mm, "end": v(68.11, -31.25) * mm});
            skLineSegment(sketch, "E740", {"start": v(68.11, -31.25) * mm, "end": v(68.3, -31.2) * mm});
            skLineSegment(sketch, "E741", {"start": v(68.3, -31.2) * mm, "end": v(68.51, -31.16) * mm});
            skLineSegment(sketch, "E742", {"start": v(68.51, -31.16) * mm, "end": v(68.74, -31.1) * mm});
            skLineSegment(sketch, "E743", {"start": v(68.74, -31.1) * mm, "end": v(68.98, -31.04) * mm});
            skLineSegment(sketch, "E744", {"start": v(68.98, -31.04) * mm, "end": v(69.24, -30.97) * mm});
            skLineSegment(sketch, "E745", {"start": v(69.24, -30.97) * mm, "end": v(69.51, -30.88) * mm});
            skLineSegment(sketch, "E746", {"start": v(69.51, -30.88) * mm, "end": v(69.8, -30.79) * mm});
            skLineSegment(sketch, "E747", {"start": v(69.8, -30.79) * mm, "end": v(70.11, -30.68) * mm});
            skLineSegment(sketch, "E748", {"start": v(70.11, -30.68) * mm, "end": v(70.44, -30.56) * mm});
            skLineSegment(sketch, "E749", {"start": v(70.44, -30.56) * mm, "end": v(70.77, -30.42) * mm});
            skLineSegment(sketch, "E750", {"start": v(70.77, -30.42) * mm, "end": v(71.13, -30.28) * mm});
            skLineSegment(sketch, "E751", {"start": v(71.13, -30.28) * mm, "end": v(71.5, -30.12) * mm});
            skLineSegment(sketch, "E752", {"start": v(71.5, -30.12) * mm, "end": v(71.87, -29.94) * mm});
            skLineSegment(sketch, "E753", {"start": v(71.87, -29.94) * mm, "end": v(72.26, -29.75) * mm});
            skLineSegment(sketch, "E754", {"start": v(72.26, -29.75) * mm, "end": v(72.67, -29.54) * mm});
            skLineSegment(sketch, "E755", {"start": v(72.67, -29.54) * mm, "end": v(73.09, -29.32) * mm});
            skLineSegment(sketch, "E756", {"start": v(73.09, -29.32) * mm, "end": v(73.52, -29.07) * mm});
            skLineSegment(sketch, "E757", {"start": v(73.52, -29.07) * mm, "end": v(73.96, -28.81) * mm});
            skLineSegment(sketch, "E758", {"start": v(73.96, -28.81) * mm, "end": v(74.41, -28.54) * mm});
            skLineSegment(sketch, "E759", {"start": v(74.41, -28.54) * mm, "end": v(74.88, -28.24) * mm});
            skLineSegment(sketch, "E760", {"start": v(74.88, -28.24) * mm, "end": v(75.35, -27.92) * mm});
            skLineSegment(sketch, "E761", {"start": v(75.35, -27.92) * mm, "end": v(75.83, -27.59) * mm});
            skLineSegment(sketch, "E762", {"start": v(75.83, -27.59) * mm, "end": v(76.13, -27.24) * mm});
            skLineSegment(sketch, "E763", {"start": v(76.13, -27.24) * mm, "end": v(75.78, -23.71) * mm});
            skLineSegment(sketch, "E764", {"start": v(75.78, -23.71) * mm, "end": v(75.41, -23.44) * mm});
            skLineSegment(sketch, "E765", {"start": v(75.41, -23.44) * mm, "end": v(74.87, -23.2) * mm});
            skLineSegment(sketch, "E766", {"start": v(74.87, -23.2) * mm, "end": v(74.35, -23) * mm});
            skLineSegment(sketch, "E767", {"start": v(74.35, -23) * mm, "end": v(73.84, -22.8) * mm});
            skLineSegment(sketch, "E768", {"start": v(73.84, -22.8) * mm, "end": v(73.34, -22.6) * mm});
            skLineSegment(sketch, "E769", {"start": v(73.34, -22.6) * mm, "end": v(72.85, -22.44) * mm});
            skLineSegment(sketch, "E770", {"start": v(72.85, -22.44) * mm, "end": v(72.38, -22.3) * mm});
            skLineSegment(sketch, "E771", {"start": v(72.38, -22.3) * mm, "end": v(71.93, -22.15) * mm});
            skLineSegment(sketch, "E772", {"start": v(71.93, -22.15) * mm, "end": v(71.49, -22.03) * mm});
            skLineSegment(sketch, "E773", {"start": v(71.49, -22.03) * mm, "end": v(71.06, -21.92) * mm});
            skLineSegment(sketch, "E774", {"start": v(71.06, -21.92) * mm, "end": v(70.66, -21.83) * mm});
            skLineSegment(sketch, "E775", {"start": v(70.66, -21.83) * mm, "end": v(70.27, -21.74) * mm});
            skLineSegment(sketch, "E776", {"start": v(70.27, -21.74) * mm, "end": v(69.9, -21.67) * mm});
            skLineSegment(sketch, "E777", {"start": v(69.9, -21.67) * mm, "end": v(69.53, -21.6) * mm});
            skLineSegment(sketch, "E778", {"start": v(69.53, -21.6) * mm, "end": v(69.2, -21.55) * mm});
            skLineSegment(sketch, "E779", {"start": v(69.2, -21.55) * mm, "end": v(68.87, -21.5) * mm});
            skLineSegment(sketch, "E780", {"start": v(68.87, -21.5) * mm, "end": v(68.57, -21.47) * mm});
            skLineSegment(sketch, "E781", {"start": v(68.57, -21.47) * mm, "end": v(68.28, -21.44) * mm});
            skLineSegment(sketch, "E782", {"start": v(68.28, -21.44) * mm, "end": v(68.01, -21.42) * mm});
            skLineSegment(sketch, "E783", {"start": v(68.01, -21.42) * mm, "end": v(67.76, -21.4) * mm});
            skLineSegment(sketch, "E784", {"start": v(67.76, -21.4) * mm, "end": v(67.53, -21.4) * mm});
            skLineSegment(sketch, "E785", {"start": v(67.53, -21.4) * mm, "end": v(67.32, -21.4) * mm});
            skLineSegment(sketch, "E786", {"start": v(67.32, -21.4) * mm, "end": v(67.12, -21.4) * mm});
            skLineSegment(sketch, "E787", {"start": v(67.12, -21.4) * mm, "end": v(66.95, -21.4) * mm});
            skLineSegment(sketch, "E788", {"start": v(66.95, -21.4) * mm, "end": v(66.8, -21.4) * mm});
            skLineSegment(sketch, "E789", {"start": v(66.8, -21.4) * mm, "end": v(66.65, -21.4) * mm});
            skLineSegment(sketch, "E790", {"start": v(66.65, -21.4) * mm, "end": v(66.53, -21.42) * mm});
            skLineSegment(sketch, "E791", {"start": v(66.53, -21.42) * mm, "end": v(66.43, -21.43) * mm});
            skLineSegment(sketch, "E792", {"start": v(66.43, -21.43) * mm, "end": v(66.35, -21.44) * mm});
            skLineSegment(sketch, "E793", {"start": v(66.35, -21.44) * mm, "end": v(66.29, -21.44) * mm});
            skLineSegment(sketch, "E794", {"start": v(66.29, -21.44) * mm, "end": v(66.24, -21.45) * mm});
            skLineSegment(sketch, "E795", {"start": v(66.24, -21.45) * mm, "end": v(66.22, -21.46) * mm});
            skLineSegment(sketch, "E796", {"start": v(66.22, -21.46) * mm, "end": v(62.71, -22.17) * mm});
            skLineSegment(sketch, "E797", {"start": v(62.71, -22.17) * mm, "end": v(60.85, -15.58) * mm});
            skLineSegment(sketch, "E798", {"start": v(60.85, -15.58) * mm, "end": v(64.22, -14.35) * mm});
            skLineSegment(sketch, "E799", {"start": v(64.22, -14.35) * mm, "end": v(64.24, -14.34) * mm});
            skLineSegment(sketch, "E800", {"start": v(64.24, -14.34) * mm, "end": v(64.28, -14.33) * mm});
            skLineSegment(sketch, "E801", {"start": v(64.28, -14.33) * mm, "end": v(64.34, -14.3) * mm});
            skLineSegment(sketch, "E802", {"start": v(64.34, -14.3) * mm, "end": v(64.41, -14.27) * mm});
            skLineSegment(sketch, "E803", {"start": v(64.41, -14.27) * mm, "end": v(64.5, -14.22) * mm});
            skLineSegment(sketch, "E804", {"start": v(64.5, -14.22) * mm, "end": v(64.61, -14.17) * mm});
            skLineSegment(sketch, "E805", {"start": v(64.61, -14.17) * mm, "end": v(64.73, -14.1) * mm});
            skLineSegment(sketch, "E806", {"start": v(64.73, -14.1) * mm, "end": v(64.87, -14.02) * mm});
            skLineSegment(sketch, "E807", {"start": v(64.87, -14.02) * mm, "end": v(65.02, -13.94) * mm});
            skLineSegment(sketch, "E808", {"start": v(65.02, -13.94) * mm, "end": v(65.19, -13.83) * mm});
            skLineSegment(sketch, "E809", {"start": v(65.19, -13.83) * mm, "end": v(65.37, -13.72) * mm});
            skLineSegment(sketch, "E810", {"start": v(65.37, -13.72) * mm, "end": v(65.56, -13.59) * mm});
            skLineSegment(sketch, "E811", {"start": v(65.56, -13.59) * mm, "end": v(65.76, -13.45) * mm});
            skLineSegment(sketch, "E812", {"start": v(65.76, -13.45) * mm, "end": v(65.98, -13.29) * mm});
            skLineSegment(sketch, "E813", {"start": v(65.98, -13.29) * mm, "end": v(66.21, -13.11) * mm});
            skLineSegment(sketch, "E814", {"start": v(66.21, -13.11) * mm, "end": v(66.45, -12.92) * mm});
            skLineSegment(sketch, "E815", {"start": v(66.45, -12.92) * mm, "end": v(66.7, -12.72) * mm});
            skLineSegment(sketch, "E816", {"start": v(66.7, -12.72) * mm, "end": v(66.97, -12.5) * mm});
            skLineSegment(sketch, "E817", {"start": v(66.97, -12.5) * mm, "end": v(67.24, -12.25) * mm});
            skLineSegment(sketch, "E818", {"start": v(67.24, -12.25) * mm, "end": v(67.52, -12) * mm});
            skLineSegment(sketch, "E819", {"start": v(67.52, -12) * mm, "end": v(67.8, -11.72) * mm});
            skLineSegment(sketch, "E820", {"start": v(67.8, -11.72) * mm, "end": v(68.1, -11.42) * mm});
            skLineSegment(sketch, "E821", {"start": v(68.1, -11.42) * mm, "end": v(68.4, -11.1) * mm});
            skLineSegment(sketch, "E822", {"start": v(68.4, -11.1) * mm, "end": v(68.72, -10.77) * mm});
            skLineSegment(sketch, "E823", {"start": v(68.72, -10.77) * mm, "end": v(69.04, -10.42) * mm});
            skLineSegment(sketch, "E824", {"start": v(69.04, -10.42) * mm, "end": v(69.36, -10.05) * mm});
            skLineSegment(sketch, "E825", {"start": v(69.36, -10.05) * mm, "end": v(69.68, -9.65) * mm});
            skLineSegment(sketch, "E826", {"start": v(69.68, -9.65) * mm, "end": v(70.01, -9.23) * mm});
            skLineSegment(sketch, "E827", {"start": v(70.01, -9.23) * mm, "end": v(70.35, -8.8) * mm});
            skLineSegment(sketch, "E828", {"start": v(70.35, -8.8) * mm, "end": v(70.68, -8.34) * mm});
            skLineSegment(sketch, "E829", {"start": v(70.68, -8.34) * mm, "end": v(71.02, -7.86) * mm});
            skLineSegment(sketch, "E830", {"start": v(71.02, -7.86) * mm, "end": v(71.19, -7.43) * mm});
            skLineSegment(sketch, "E831", {"start": v(71.19, -7.43) * mm, "end": v(69.65, -4.24) * mm});
            skLineSegment(sketch, "E832", {"start": v(69.65, -4.24) * mm, "end": v(69.2, -4.1) * mm});
            skLineSegment(sketch, "E833", {"start": v(69.2, -4.1) * mm, "end": v(68.62, -4.07) * mm});
            skLineSegment(sketch, "E834", {"start": v(68.62, -4.07) * mm, "end": v(68.06, -4.05) * mm});
            skLineSegment(sketch, "E835", {"start": v(68.06, -4.05) * mm, "end": v(67.5, -4.03) * mm});
            skLineSegment(sketch, "E836", {"start": v(67.5, -4.03) * mm, "end": v(66.97, -4.03) * mm});
            skLineSegment(sketch, "E837", {"start": v(66.97, -4.03) * mm, "end": v(66.46, -4.04) * mm});
            skLineSegment(sketch, "E838", {"start": v(66.46, -4.04) * mm, "end": v(65.97, -4.06) * mm});
            skLineSegment(sketch, "E839", {"start": v(65.97, -4.06) * mm, "end": v(65.5, -4.09) * mm});
            skLineSegment(sketch, "E840", {"start": v(65.5, -4.09) * mm, "end": v(65.04, -4.12) * mm});
            skLineSegment(sketch, "E841", {"start": v(65.04, -4.12) * mm, "end": v(64.6, -4.17) * mm});
            skLineSegment(sketch, "E842", {"start": v(64.6, -4.17) * mm, "end": v(64.19, -4.21) * mm});
            skLineSegment(sketch, "E843", {"start": v(64.19, -4.21) * mm, "end": v(63.8, -4.27) * mm});
            skLineSegment(sketch, "E844", {"start": v(63.8, -4.27) * mm, "end": v(63.41, -4.33) * mm});
            skLineSegment(sketch, "E845", {"start": v(63.41, -4.33) * mm, "end": v(63.06, -4.39) * mm});
            skLineSegment(sketch, "E846", {"start": v(63.06, -4.39) * mm, "end": v(62.72, -4.45) * mm});
            skLineSegment(sketch, "E847", {"start": v(62.72, -4.45) * mm, "end": v(62.4, -4.52) * mm});
            skLineSegment(sketch, "E848", {"start": v(62.4, -4.52) * mm, "end": v(62.1, -4.6) * mm});
            skLineSegment(sketch, "E849", {"start": v(62.1, -4.6) * mm, "end": v(61.82, -4.66) * mm});
            skLineSegment(sketch, "E850", {"start": v(61.82, -4.66) * mm, "end": v(61.56, -4.74) * mm});
            skLineSegment(sketch, "E851", {"start": v(61.56, -4.74) * mm, "end": v(61.32, -4.8) * mm});
            skLineSegment(sketch, "E852", {"start": v(61.32, -4.8) * mm, "end": v(61.1, -4.88) * mm});
            skLineSegment(sketch, "E853", {"start": v(61.1, -4.88) * mm, "end": v(60.9, -4.95) * mm});
            skLineSegment(sketch, "E854", {"start": v(60.9, -4.95) * mm, "end": v(60.72, -5.01) * mm});
            skLineSegment(sketch, "E855", {"start": v(60.72, -5.01) * mm, "end": v(60.55, -5.08) * mm});
            skLineSegment(sketch, "E856", {"start": v(60.55, -5.08) * mm, "end": v(60.4, -5.14) * mm});
            skLineSegment(sketch, "E857", {"start": v(60.4, -5.14) * mm, "end": v(60.28, -5.2) * mm});
            skLineSegment(sketch, "E858", {"start": v(60.28, -5.2) * mm, "end": v(60.17, -5.24) * mm});
            skLineSegment(sketch, "E859", {"start": v(60.17, -5.24) * mm, "end": v(60.08, -5.28) * mm});
            skLineSegment(sketch, "E860", {"start": v(60.08, -5.28) * mm, "end": v(60, -5.32) * mm});
            skLineSegment(sketch, "E861", {"start": v(60, -5.32) * mm, "end": v(59.95, -5.35) * mm});
            skLineSegment(sketch, "E862", {"start": v(59.95, -5.35) * mm, "end": v(59.91, -5.37) * mm});
            skLineSegment(sketch, "E863", {"start": v(59.91, -5.37) * mm, "end": v(59.89, -5.38) * mm});
            skLineSegment(sketch, "E864", {"start": v(59.89, -5.38) * mm, "end": v(56.84, -7.25) * mm});
            skLineSegment(sketch, "E865", {"start": v(56.84, -7.25) * mm, "end": v(52.84, -1.7) * mm});
            skLineSegment(sketch, "E866", {"start": v(52.84, -1.7) * mm, "end": v(55.58, 0.6) * mm});
            skLineSegment(sketch, "E867", {"start": v(55.58, 0.6) * mm, "end": v(55.6, 0.62) * mm});
            skLineSegment(sketch, "E868", {"start": v(55.6, 0.62) * mm, "end": v(55.63, 0.65) * mm});
            skLineSegment(sketch, "E869", {"start": v(55.63, 0.65) * mm, "end": v(55.68, 0.7) * mm});
            skLineSegment(sketch, "E870", {"start": v(55.68, 0.7) * mm, "end": v(55.74, 0.75) * mm});
            skLineSegment(sketch, "E871", {"start": v(55.74, 0.75) * mm, "end": v(55.8, 0.83) * mm});
            skLineSegment(sketch, "E872", {"start": v(55.8, 0.83) * mm, "end": v(55.89, 0.91) * mm});
            skLineSegment(sketch, "E873", {"start": v(55.89, 0.91) * mm, "end": v(55.98, 1.02) * mm});
            skLineSegment(sketch, "E874", {"start": v(55.98, 1.02) * mm, "end": v(56.08, 1.14) * mm});
            skLineSegment(sketch, "E875", {"start": v(56.08, 1.14) * mm, "end": v(56.2, 1.27) * mm});
            skLineSegment(sketch, "E876", {"start": v(56.2, 1.27) * mm, "end": v(56.31, 1.43) * mm});
            skLineSegment(sketch, "E877", {"start": v(56.31, 1.43) * mm, "end": v(56.44, 1.6) * mm});
            skLineSegment(sketch, "E878", {"start": v(56.44, 1.6) * mm, "end": v(56.58, 1.78) * mm});
            skLineSegment(sketch, "E879", {"start": v(56.58, 1.78) * mm, "end": v(56.73, 1.99) * mm});
            skLineSegment(sketch, "E880", {"start": v(56.73, 1.99) * mm, "end": v(56.88, 2.21) * mm});
            skLineSegment(sketch, "E881", {"start": v(56.88, 2.21) * mm, "end": v(57.03, 2.45) * mm});
            skLineSegment(sketch, "E882", {"start": v(57.03, 2.45) * mm, "end": v(57.2, 2.71) * mm});
            skLineSegment(sketch, "E883", {"start": v(57.2, 2.71) * mm, "end": v(57.36, 3) * mm});
            skLineSegment(sketch, "E884", {"start": v(57.36, 3) * mm, "end": v(57.53, 3.3) * mm});
            skLineSegment(sketch, "E885", {"start": v(57.53, 3.3) * mm, "end": v(57.7, 3.61) * mm});
            skLineSegment(sketch, "E886", {"start": v(57.7, 3.61) * mm, "end": v(57.88, 3.95) * mm});
            skLineSegment(sketch, "E887", {"start": v(57.88, 3.95) * mm, "end": v(58.05, 4.3) * mm});
            skLineSegment(sketch, "E888", {"start": v(58.05, 4.3) * mm, "end": v(58.23, 4.69) * mm});
            skLineSegment(sketch, "E889", {"start": v(58.23, 4.69) * mm, "end": v(58.4, 5.09) * mm});
            skLineSegment(sketch, "E890", {"start": v(58.4, 5.09) * mm, "end": v(58.59, 5.5) * mm});
            skLineSegment(sketch, "E891", {"start": v(58.59, 5.5) * mm, "end": v(58.76, 5.95) * mm});
            skLineSegment(sketch, "E892", {"start": v(58.76, 5.95) * mm, "end": v(58.94, 6.41) * mm});
            skLineSegment(sketch, "E893", {"start": v(58.94, 6.41) * mm, "end": v(59.1, 6.9) * mm});
            skLineSegment(sketch, "E894", {"start": v(59.1, 6.9) * mm, "end": v(59.28, 7.4) * mm});
            skLineSegment(sketch, "E895", {"start": v(59.28, 7.4) * mm, "end": v(59.44, 7.92) * mm});
            skLineSegment(sketch, "E896", {"start": v(59.44, 7.92) * mm, "end": v(59.6, 8.47) * mm});
            skLineSegment(sketch, "E897", {"start": v(59.6, 8.47) * mm, "end": v(59.75, 9.04) * mm});
            skLineSegment(sketch, "E898", {"start": v(59.75, 9.04) * mm, "end": v(59.76, 9.5) * mm});
            skLineSegment(sketch, "E899", {"start": v(59.76, 9.5) * mm, "end": v(57.22, 11.97) * mm});
            skLineSegment(sketch, "E900", {"start": v(57.22, 11.97) * mm, "end": v(56.77, 11.94) * mm});
            skLineSegment(sketch, "E901", {"start": v(56.77, 11.94) * mm, "end": v(56.2, 11.78) * mm});
            skLineSegment(sketch, "E902", {"start": v(56.2, 11.78) * mm, "end": v(55.66, 11.6) * mm});
            skLineSegment(sketch, "E903", {"start": v(55.66, 11.6) * mm, "end": v(55.14, 11.43) * mm});
            skLineSegment(sketch, "E904", {"start": v(55.14, 11.43) * mm, "end": v(54.64, 11.25) * mm});
            skLineSegment(sketch, "E905", {"start": v(54.64, 11.25) * mm, "end": v(54.16, 11.06) * mm});
            skLineSegment(sketch, "E906", {"start": v(54.16, 11.06) * mm, "end": v(53.7, 10.88) * mm});
            skLineSegment(sketch, "E907", {"start": v(53.7, 10.88) * mm, "end": v(53.27, 10.69) * mm});
            skLineSegment(sketch, "E908", {"start": v(53.27, 10.69) * mm, "end": v(52.86, 10.5) * mm});
            skLineSegment(sketch, "E909", {"start": v(52.86, 10.5) * mm, "end": v(52.46, 10.31) * mm});
            skLineSegment(sketch, "E910", {"start": v(52.46, 10.31) * mm, "end": v(52.09, 10.12) * mm});
            skLineSegment(sketch, "E911", {"start": v(52.09, 10.12) * mm, "end": v(51.73, 9.94) * mm});
            skLineSegment(sketch, "E912", {"start": v(51.73, 9.94) * mm, "end": v(51.4, 9.75) * mm});
            skLineSegment(sketch, "E913", {"start": v(51.4, 9.75) * mm, "end": v(51.08, 9.57) * mm});
            skLineSegment(sketch, "E914", {"start": v(51.08, 9.57) * mm, "end": v(50.79, 9.4) * mm});
            skLineSegment(sketch, "E915", {"start": v(50.79, 9.4) * mm, "end": v(50.51, 9.22) * mm});
            skLineSegment(sketch, "E916", {"start": v(50.51, 9.22) * mm, "end": v(50.26, 9.05) * mm});
            skLineSegment(sketch, "E917", {"start": v(50.26, 9.05) * mm, "end": v(50.02, 8.9) * mm});
            skLineSegment(sketch, "E918", {"start": v(50.02, 8.9) * mm, "end": v(49.8, 8.74) * mm});
            skLineSegment(sketch, "E919", {"start": v(49.8, 8.74) * mm, "end": v(49.6, 8.59) * mm});
            skLineSegment(sketch, "E920", {"start": v(49.6, 8.59) * mm, "end": v(49.41, 8.44) * mm});
            skLineSegment(sketch, "E921", {"start": v(49.41, 8.44) * mm, "end": v(49.25, 8.31) * mm});
            skLineSegment(sketch, "E922", {"start": v(49.25, 8.31) * mm, "end": v(49.1, 8.19) * mm});
            skLineSegment(sketch, "E923", {"start": v(49.1, 8.19) * mm, "end": v(48.97, 8.07) * mm});
            skLineSegment(sketch, "E924", {"start": v(48.97, 8.07) * mm, "end": v(48.85, 7.96) * mm});
            skLineSegment(sketch, "E925", {"start": v(48.85, 7.96) * mm, "end": v(48.75, 7.87) * mm});
            skLineSegment(sketch, "E926", {"start": v(48.75, 7.87) * mm, "end": v(48.66, 7.79) * mm});
            skLineSegment(sketch, "E927", {"start": v(48.66, 7.79) * mm, "end": v(48.6, 7.71) * mm});
            skLineSegment(sketch, "E928", {"start": v(48.6, 7.71) * mm, "end": v(48.54, 7.65) * mm});
            skLineSegment(sketch, "E929", {"start": v(48.54, 7.65) * mm, "end": v(48.5, 7.6) * mm});
            skLineSegment(sketch, "E930", {"start": v(48.5, 7.6) * mm, "end": v(48.46, 7.57) * mm});
            skLineSegment(sketch, "E931", {"start": v(48.46, 7.57) * mm, "end": v(48.45, 7.55) * mm});
            skLineSegment(sketch, "E932", {"start": v(48.45, 7.55) * mm, "end": v(46.22, 4.75) * mm});
            skLineSegment(sketch, "E933", {"start": v(46.22, 4.75) * mm, "end": v(40.56, 8.6) * mm});
            skLineSegment(sketch, "E934", {"start": v(40.56, 8.6) * mm, "end": v(42.35, 11.7) * mm});
            skLineSegment(sketch, "E935", {"start": v(42.35, 11.7) * mm, "end": v(42.36, 11.73) * mm});
            skLineSegment(sketch, "E936", {"start": v(42.36, 11.73) * mm, "end": v(42.38, 11.77) * mm});
            skLineSegment(sketch, "E937", {"start": v(42.38, 11.77) * mm, "end": v(42.4, 11.83) * mm});
            skLineSegment(sketch, "E938", {"start": v(42.4, 11.83) * mm, "end": v(42.44, 11.9) * mm});
            skLineSegment(sketch, "E939", {"start": v(42.44, 11.9) * mm, "end": v(42.49, 12) * mm});
            skLineSegment(sketch, "E940", {"start": v(42.49, 12) * mm, "end": v(42.53, 12.1) * mm});
            skLineSegment(sketch, "E941", {"start": v(42.53, 12.1) * mm, "end": v(42.58, 12.23) * mm});
            skLineSegment(sketch, "E942", {"start": v(42.58, 12.23) * mm, "end": v(42.64, 12.38) * mm});
            skLineSegment(sketch, "E943", {"start": v(42.64, 12.38) * mm, "end": v(42.7, 12.55) * mm});
            skLineSegment(sketch, "E944", {"start": v(42.7, 12.55) * mm, "end": v(42.76, 12.73) * mm});
            skLineSegment(sketch, "E945", {"start": v(42.76, 12.73) * mm, "end": v(42.82, 12.93) * mm});
            skLineSegment(sketch, "E946", {"start": v(42.82, 12.93) * mm, "end": v(42.89, 13.16) * mm});
            skLineSegment(sketch, "E947", {"start": v(42.89, 13.16) * mm, "end": v(42.95, 13.4) * mm});
            skLineSegment(sketch, "E948", {"start": v(42.95, 13.4) * mm, "end": v(43.02, 13.66) * mm});
            skLineSegment(sketch, "E949", {"start": v(43.02, 13.66) * mm, "end": v(43.08, 13.94) * mm});
            skLineSegment(sketch, "E950", {"start": v(43.08, 13.94) * mm, "end": v(43.14, 14.24) * mm});
            skLineSegment(sketch, "E951", {"start": v(43.14, 14.24) * mm, "end": v(43.2, 14.56) * mm});
            skLineSegment(sketch, "E952", {"start": v(43.2, 14.56) * mm, "end": v(43.26, 14.9) * mm});
            skLineSegment(sketch, "E953", {"start": v(43.26, 14.9) * mm, "end": v(43.31, 15.26) * mm});
            skLineSegment(sketch, "E954", {"start": v(43.31, 15.26) * mm, "end": v(43.36, 15.64) * mm});
            skLineSegment(sketch, "E955", {"start": v(43.36, 15.64) * mm, "end": v(43.4, 16.03) * mm});
            skLineSegment(sketch, "E956", {"start": v(43.4, 16.03) * mm, "end": v(43.44, 16.45) * mm});
            skLineSegment(sketch, "E957", {"start": v(43.44, 16.45) * mm, "end": v(43.47, 16.89) * mm});
            skLineSegment(sketch, "E958", {"start": v(43.47, 16.89) * mm, "end": v(43.5, 17.34) * mm});
            skLineSegment(sketch, "E959", {"start": v(43.5, 17.34) * mm, "end": v(43.51, 17.82) * mm});
            skLineSegment(sketch, "E960", {"start": v(43.51, 17.82) * mm, "end": v(43.52, 18.31) * mm});
            skLineSegment(sketch, "E961", {"start": v(43.52, 18.31) * mm, "end": v(43.51, 18.82) * mm});
            skLineSegment(sketch, "E962", {"start": v(43.51, 18.82) * mm, "end": v(43.5, 19.36) * mm});
            skLineSegment(sketch, "E963", {"start": v(43.5, 19.36) * mm, "end": v(43.47, 19.9) * mm});
            skLineSegment(sketch, "E964", {"start": v(43.47, 19.9) * mm, "end": v(43.44, 20.47) * mm});
            skLineSegment(sketch, "E965", {"start": v(43.44, 20.47) * mm, "end": v(43.39, 21.06) * mm});
            skLineSegment(sketch, "E966", {"start": v(43.39, 21.06) * mm, "end": v(43.24, 21.5) * mm});
            skLineSegment(sketch, "E967", {"start": v(43.24, 21.5) * mm, "end": v(40, 22.95) * mm});
            skLineSegment(sketch, "E968", {"start": v(40, 22.95) * mm, "end": v(39.59, 22.77) * mm});
            skLineSegment(sketch, "E969", {"start": v(39.59, 22.77) * mm, "end": v(39.11, 22.42) * mm});
            skLineSegment(sketch, "E970", {"start": v(39.11, 22.42) * mm, "end": v(38.66, 22.07) * mm});
            skLineSegment(sketch, "E971", {"start": v(38.66, 22.07) * mm, "end": v(38.24, 21.73) * mm});
            skLineSegment(sketch, "E972", {"start": v(38.24, 21.73) * mm, "end": v(37.83, 21.39) * mm});
            skLineSegment(sketch, "E973", {"start": v(37.83, 21.39) * mm, "end": v(37.44, 21.05) * mm});
            skLineSegment(sketch, "E974", {"start": v(37.44, 21.05) * mm, "end": v(37.08, 20.72) * mm});
            skLineSegment(sketch, "E975", {"start": v(37.08, 20.72) * mm, "end": v(36.73, 20.4) * mm});
            skLineSegment(sketch, "E976", {"start": v(36.73, 20.4) * mm, "end": v(36.4, 20.07) * mm});
            skLineSegment(sketch, "E977", {"start": v(36.4, 20.07) * mm, "end": v(36.1, 19.76) * mm});
            skLineSegment(sketch, "E978", {"start": v(36.1, 19.76) * mm, "end": v(35.8, 19.46) * mm});
            skLineSegment(sketch, "E979", {"start": v(35.8, 19.46) * mm, "end": v(35.54, 19.16) * mm});
            skLineSegment(sketch, "E980", {"start": v(35.54, 19.16) * mm, "end": v(35.29, 18.87) * mm});
            skLineSegment(sketch, "E981", {"start": v(35.29, 18.87) * mm, "end": v(35.06, 18.6) * mm});
            skLineSegment(sketch, "E982", {"start": v(35.06, 18.6) * mm, "end": v(34.84, 18.33) * mm});
            skLineSegment(sketch, "E983", {"start": v(34.84, 18.33) * mm, "end": v(34.64, 18.07) * mm});
            skLineSegment(sketch, "E984", {"start": v(34.64, 18.07) * mm, "end": v(34.46, 17.83) * mm});
            skLineSegment(sketch, "E985", {"start": v(34.46, 17.83) * mm, "end": v(34.29, 17.6) * mm});
            skLineSegment(sketch, "E986", {"start": v(34.29, 17.6) * mm, "end": v(34.14, 17.37) * mm});
            skLineSegment(sketch, "E987", {"start": v(34.14, 17.37) * mm, "end": v(34, 17.16) * mm});
            skLineSegment(sketch, "E988", {"start": v(34, 17.16) * mm, "end": v(33.87, 16.96) * mm});
            skLineSegment(sketch, "E989", {"start": v(33.87, 16.96) * mm, "end": v(33.76, 16.78) * mm});
            skLineSegment(sketch, "E990", {"start": v(33.76, 16.78) * mm, "end": v(33.67, 16.61) * mm});
            skLineSegment(sketch, "E991", {"start": v(33.67, 16.61) * mm, "end": v(33.58, 16.46) * mm});
            skLineSegment(sketch, "E992", {"start": v(33.58, 16.46) * mm, "end": v(33.5, 16.32) * mm});
            skLineSegment(sketch, "E993", {"start": v(33.5, 16.32) * mm, "end": v(33.45, 16.2) * mm});
            skLineSegment(sketch, "E994", {"start": v(33.45, 16.2) * mm, "end": v(33.4, 16.09) * mm});
            skLineSegment(sketch, "E995", {"start": v(33.4, 16.09) * mm, "end": v(33.35, 16) * mm});
            skLineSegment(sketch, "E996", {"start": v(33.35, 16) * mm, "end": v(33.32, 15.92) * mm});
            skLineSegment(sketch, "E997", {"start": v(33.32, 15.92) * mm, "end": v(33.3, 15.86) * mm});
            skLineSegment(sketch, "E998", {"start": v(33.3, 15.86) * mm, "end": v(33.28, 15.82) * mm});
            skLineSegment(sketch, "E999", {"start": v(33.28, 15.82) * mm, "end": v(33.27, 15.8) * mm});
            skLineSegment(sketch, "E1000", {"start": v(33.27, 15.8) * mm, "end": v(32.13, 12.4) * mm});
            skLineSegment(sketch, "E1001", {"start": v(32.13, 12.4) * mm, "end": v(25.5, 14.1) * mm});
            skLineSegment(sketch, "E1002", {"start": v(25.5, 14.1) * mm, "end": v(26.12, 17.61) * mm});
            skLineSegment(sketch, "E1003", {"start": v(26.12, 17.61) * mm, "end": v(26.12, 17.64) * mm});
            skLineSegment(sketch, "E1004", {"start": v(26.12, 17.64) * mm, "end": v(26.13, 17.68) * mm});
            skLineSegment(sketch, "E1005", {"start": v(26.13, 17.68) * mm, "end": v(26.13, 17.75) * mm});
            skLineSegment(sketch, "E1006", {"start": v(26.13, 17.75) * mm, "end": v(26.14, 17.83) * mm});
            skLineSegment(sketch, "E1007", {"start": v(26.14, 17.83) * mm, "end": v(26.15, 17.93) * mm});
            skLineSegment(sketch, "E1008", {"start": v(26.15, 17.93) * mm, "end": v(26.15, 18.05) * mm});
            skLineSegment(sketch, "E1009", {"start": v(26.15, 18.05) * mm, "end": v(26.16, 18.19) * mm});
            skLineSegment(sketch, "E1010", {"start": v(26.16, 18.19) * mm, "end": v(26.16, 18.35) * mm});
            skLineSegment(sketch, "E1011", {"start": v(26.16, 18.35) * mm, "end": v(26.16, 18.52) * mm});
            skLineSegment(sketch, "E1012", {"start": v(26.16, 18.52) * mm, "end": v(26.15, 18.72) * mm});
            skLineSegment(sketch, "E1013", {"start": v(26.15, 18.72) * mm, "end": v(26.14, 18.93) * mm});
            skLineSegment(sketch, "E1014", {"start": v(26.14, 18.93) * mm, "end": v(26.13, 19.16) * mm});
            skLineSegment(sketch, "E1015", {"start": v(26.13, 19.16) * mm, "end": v(26.1, 19.4) * mm});
            skLineSegment(sketch, "E1016", {"start": v(26.1, 19.4) * mm, "end": v(26.08, 19.68) * mm});
            skLineSegment(sketch, "E1017", {"start": v(26.08, 19.68) * mm, "end": v(26.04, 19.96) * mm});
            skLineSegment(sketch, "E1018", {"start": v(26.04, 19.96) * mm, "end": v(26, 20.27) * mm});
            skLineSegment(sketch, "E1019", {"start": v(26, 20.27) * mm, "end": v(25.95, 20.59) * mm});
            skLineSegment(sketch, "E1020", {"start": v(25.95, 20.59) * mm, "end": v(25.88, 20.93) * mm});
            skLineSegment(sketch, "E1021", {"start": v(25.88, 20.93) * mm, "end": v(25.81, 21.28) * mm});
            skLineSegment(sketch, "E1022", {"start": v(25.81, 21.28) * mm, "end": v(25.73, 21.65) * mm});
            skLineSegment(sketch, "E1023", {"start": v(25.73, 21.65) * mm, "end": v(25.63, 22.04) * mm});
            skLineSegment(sketch, "E1024", {"start": v(25.63, 22.04) * mm, "end": v(25.52, 22.45) * mm});
            skLineSegment(sketch, "E1025", {"start": v(25.52, 22.45) * mm, "end": v(25.4, 22.87) * mm});
            skLineSegment(sketch, "E1026", {"start": v(25.4, 22.87) * mm, "end": v(25.27, 23.3) * mm});
            skLineSegment(sketch, "E1027", {"start": v(25.27, 23.3) * mm, "end": v(25.12, 23.76) * mm});
            skLineSegment(sketch, "E1028", {"start": v(25.12, 23.76) * mm, "end": v(24.96, 24.22) * mm});
            skLineSegment(sketch, "E1029", {"start": v(24.96, 24.22) * mm, "end": v(24.78, 24.7) * mm});
            skLineSegment(sketch, "E1030", {"start": v(24.78, 24.7) * mm, "end": v(24.58, 25.2) * mm});
            skLineSegment(sketch, "E1031", {"start": v(24.58, 25.2) * mm, "end": v(24.37, 25.7) * mm});
            skLineSegment(sketch, "E1032", {"start": v(24.37, 25.7) * mm, "end": v(24.14, 26.22) * mm});
            skLineSegment(sketch, "E1033", {"start": v(24.14, 26.22) * mm, "end": v(23.9, 26.76) * mm});
            skLineSegment(sketch, "E1034", {"start": v(23.9, 26.76) * mm, "end": v(23.61, 27.11) * mm});
            skLineSegment(sketch, "E1035", {"start": v(23.61, 27.11) * mm, "end": v(20.07, 27.38) * mm});
            skLineSegment(sketch, "E1036", {"start": v(20.07, 27.38) * mm, "end": v(19.74, 27.06) * mm});
            skLineSegment(sketch, "E1037", {"start": v(19.74, 27.06) * mm, "end": v(19.41, 26.57) * mm});
            skLineSegment(sketch, "E1038", {"start": v(19.41, 26.57) * mm, "end": v(19.11, 26.1) * mm});
            skLineSegment(sketch, "E1039", {"start": v(19.11, 26.1) * mm, "end": v(18.83, 25.62) * mm});
            skLineSegment(sketch, "E1040", {"start": v(18.83, 25.62) * mm, "end": v(18.56, 25.16) * mm});
            skLineSegment(sketch, "E1041", {"start": v(18.56, 25.16) * mm, "end": v(18.31, 24.72) * mm});
            skLineSegment(sketch, "E1042", {"start": v(18.31, 24.72) * mm, "end": v(18.08, 24.28) * mm});
            skLineSegment(sketch, "E1043", {"start": v(18.08, 24.28) * mm, "end": v(17.87, 23.85) * mm});
            skLineSegment(sketch, "E1044", {"start": v(17.87, 23.85) * mm, "end": v(17.67, 23.44) * mm});
            skLineSegment(sketch, "E1045", {"start": v(17.67, 23.44) * mm, "end": v(17.49, 23.05) * mm});
            skLineSegment(sketch, "E1046", {"start": v(17.49, 23.05) * mm, "end": v(17.32, 22.66) * mm});
            skLineSegment(sketch, "E1047", {"start": v(17.32, 22.66) * mm, "end": v(17.17, 22.3) * mm});
            skLineSegment(sketch, "E1048", {"start": v(17.17, 22.3) * mm, "end": v(17.03, 21.93) * mm});
            skLineSegment(sketch, "E1049", {"start": v(17.03, 21.93) * mm, "end": v(16.9, 21.6) * mm});
            skLineSegment(sketch, "E1050", {"start": v(16.9, 21.6) * mm, "end": v(16.8, 21.27) * mm});
            skLineSegment(sketch, "E1051", {"start": v(16.8, 21.27) * mm, "end": v(16.7, 20.96) * mm});
            skLineSegment(sketch, "E1052", {"start": v(16.7, 20.96) * mm, "end": v(16.6, 20.67) * mm});
            skLineSegment(sketch, "E1053", {"start": v(16.6, 20.67) * mm, "end": v(16.53, 20.39) * mm});
            skLineSegment(sketch, "E1054", {"start": v(16.53, 20.39) * mm, "end": v(16.46, 20.13) * mm});
            skLineSegment(sketch, "E1055", {"start": v(16.46, 20.13) * mm, "end": v(16.4, 19.88) * mm});
            skLineSegment(sketch, "E1056", {"start": v(16.4, 19.88) * mm, "end": v(16.36, 19.66) * mm});
            skLineSegment(sketch, "E1057", {"start": v(16.36, 19.66) * mm, "end": v(16.31, 19.45) * mm});
            skLineSegment(sketch, "E1058", {"start": v(16.31, 19.45) * mm, "end": v(16.28, 19.26) * mm});
            skLineSegment(sketch, "E1059", {"start": v(16.28, 19.26) * mm, "end": v(16.25, 19.08) * mm});
            skLineSegment(sketch, "E1060", {"start": v(16.25, 19.08) * mm, "end": v(16.23, 18.93) * mm});
            skLineSegment(sketch, "E1061", {"start": v(16.23, 18.93) * mm, "end": v(16.22, 18.79) * mm});
            skLineSegment(sketch, "E1062", {"start": v(16.22, 18.79) * mm, "end": v(16.2, 18.67) * mm});
            skLineSegment(sketch, "E1063", {"start": v(16.2, 18.67) * mm, "end": v(16.2, 18.57) * mm});
            skLineSegment(sketch, "E1064", {"start": v(16.2, 18.57) * mm, "end": v(16.2, 18.49) * mm});
            skLineSegment(sketch, "E1065", {"start": v(16.2, 18.49) * mm, "end": v(16.19, 18.42) * mm});
            skLineSegment(sketch, "E1066", {"start": v(16.19, 18.42) * mm, "end": v(16.19, 18.38) * mm});
            skLineSegment(sketch, "E1067", {"start": v(16.19, 18.38) * mm, "end": v(16.19, 18.35) * mm});
            skLineSegment(sketch, "E1068", {"start": v(16.19, 18.35) * mm, "end": v(16.28, 14.78) * mm});
            skLineSegment(sketch, "E1069", {"start": v(16.28, 14.78) * mm, "end": v(9.47, 14.1) * mm});
            skLineSegment(sketch, "E1070", {"start": v(9.47, 14.1) * mm, "end": v(8.85, 17.61) * mm});
            skLineSegment(sketch, "E1071", {"start": v(8.85, 17.61) * mm, "end": v(8.84, 17.64) * mm});
            skLineSegment(sketch, "E1072", {"start": v(8.84, 17.64) * mm, "end": v(8.83, 17.68) * mm});
            skLineSegment(sketch, "E1073", {"start": v(8.83, 17.68) * mm, "end": v(8.82, 17.75) * mm});
            skLineSegment(sketch, "E1074", {"start": v(8.82, 17.75) * mm, "end": v(8.8, 17.82) * mm});
            skLineSegment(sketch, "E1075", {"start": v(8.8, 17.82) * mm, "end": v(8.77, 17.92) * mm});
            skLineSegment(sketch, "E1076", {"start": v(8.77, 17.92) * mm, "end": v(8.73, 18.04) * mm});
            skLineSegment(sketch, "E1077", {"start": v(8.73, 18.04) * mm, "end": v(8.69, 18.17) * mm});
            skLineSegment(sketch, "E1078", {"start": v(8.69, 18.17) * mm, "end": v(8.64, 18.32) * mm});
            skLineSegment(sketch, "E1079", {"start": v(8.64, 18.32) * mm, "end": v(8.57, 18.48) * mm});
            skLineSegment(sketch, "E1080", {"start": v(8.57, 18.48) * mm, "end": v(8.5, 18.66) * mm});
            skLineSegment(sketch, "E1081", {"start": v(8.5, 18.66) * mm, "end": v(8.42, 18.86) * mm});
            skLineSegment(sketch, "E1082", {"start": v(8.42, 18.86) * mm, "end": v(8.33, 19.07) * mm});
            skLineSegment(sketch, "E1083", {"start": v(8.33, 19.07) * mm, "end": v(8.22, 19.3) * mm});
            skLineSegment(sketch, "E1084", {"start": v(8.22, 19.3) * mm, "end": v(8.1, 19.54) * mm});
            skLineSegment(sketch, "E1085", {"start": v(8.1, 19.54) * mm, "end": v(7.97, 19.8) * mm});
            skLineSegment(sketch, "E1086", {"start": v(7.97, 19.8) * mm, "end": v(7.83, 20.07) * mm});
            skLineSegment(sketch, "E1087", {"start": v(7.83, 20.07) * mm, "end": v(7.67, 20.35) * mm});
            skLineSegment(sketch, "E1088", {"start": v(7.67, 20.35) * mm, "end": v(7.5, 20.65) * mm});
            skLineSegment(sketch, "E1089", {"start": v(7.5, 20.65) * mm, "end": v(7.3, 20.96) * mm});
            skLineSegment(sketch, "E1090", {"start": v(7.3, 20.96) * mm, "end": v(7.1, 21.28) * mm});
            skLineSegment(sketch, "E1091", {"start": v(7.1, 21.28) * mm, "end": v(6.87, 21.6) * mm});
            skLineSegment(sketch, "E1092", {"start": v(6.87, 21.6) * mm, "end": v(6.64, 21.95) * mm});
            skLineSegment(sketch, "E1093", {"start": v(6.64, 21.95) * mm, "end": v(6.38, 22.3) * mm});
            skLineSegment(sketch, "E1094", {"start": v(6.38, 22.3) * mm, "end": v(6.1, 22.67) * mm});
            skLineSegment(sketch, "E1095", {"start": v(6.1, 22.67) * mm, "end": v(5.8, 23.04) * mm});
            skLineSegment(sketch, "E1096", {"start": v(5.8, 23.04) * mm, "end": v(5.5, 23.43) * mm});
            skLineSegment(sketch, "E1097", {"start": v(5.5, 23.43) * mm, "end": v(5.16, 23.82) * mm});
            skLineSegment(sketch, "E1098", {"start": v(5.16, 23.82) * mm, "end": v(4.81, 24.21) * mm});
            skLineSegment(sketch, "E1099", {"start": v(4.81, 24.21) * mm, "end": v(4.44, 24.62) * mm});
            skLineSegment(sketch, "E1100", {"start": v(4.44, 24.62) * mm, "end": v(4.05, 25.03) * mm});
            skLineSegment(sketch, "E1101", {"start": v(4.05, 25.03) * mm, "end": v(3.63, 25.44) * mm});
            skLineSegment(sketch, "E1102", {"start": v(3.63, 25.44) * mm, "end": v(3.24, 25.68) * mm});
            skLineSegment(sketch, "E1103", {"start": v(3.24, 25.68) * mm, "end": v(-0.17, 24.72) * mm});
            skLineSegment(sketch, "E1104", {"start": v(-0.17, 24.72) * mm, "end": v(-0.38, 24.31) * mm});
            skLineSegment(sketch, "E1105", {"start": v(-0.38, 24.31) * mm, "end": v(-0.52, 23.74) * mm});
            skLineSegment(sketch, "E1106", {"start": v(-0.52, 23.74) * mm, "end": v(-0.64, 23.19) * mm});
            skLineSegment(sketch, "E1107", {"start": v(-0.64, 23.19) * mm, "end": v(-0.75, 22.65) * mm});
            skLineSegment(sketch, "E1108", {"start": v(-0.75, 22.65) * mm, "end": v(-0.84, 22.12) * mm});
            skLineSegment(sketch, "E1109", {"start": v(-0.84, 22.12) * mm, "end": v(-0.92, 21.62) * mm});
            skLineSegment(sketch, "E1110", {"start": v(-0.92, 21.62) * mm, "end": v(-0.99, 21.13) * mm});
            skLineSegment(sketch, "E1111", {"start": v(-0.99, 21.13) * mm, "end": v(-1.04, 20.66) * mm});
            skLineSegment(sketch, "E1112", {"start": v(-1.04, 20.66) * mm, "end": v(-1.09, 20.2) * mm});
            skLineSegment(sketch, "E1113", {"start": v(-1.09, 20.2) * mm, "end": v(-1.12, 19.77) * mm});
            skLineSegment(sketch, "E1114", {"start": v(-1.12, 19.77) * mm, "end": v(-1.15, 19.35) * mm});
            skLineSegment(sketch, "E1115", {"start": v(-1.15, 19.35) * mm, "end": v(-1.16, 18.95) * mm});
            skLineSegment(sketch, "E1116", {"start": v(-1.16, 18.95) * mm, "end": v(-1.17, 18.57) * mm});
            skLineSegment(sketch, "E1117", {"start": v(-1.17, 18.57) * mm, "end": v(-1.17, 18.2) * mm});
            skLineSegment(sketch, "E1118", {"start": v(-1.17, 18.2) * mm, "end": v(-1.16, 17.86) * mm});
            skLineSegment(sketch, "E1119", {"start": v(-1.16, 17.86) * mm, "end": v(-1.15, 17.53) * mm});
            skLineSegment(sketch, "E1120", {"start": v(-1.15, 17.53) * mm, "end": v(-1.13, 17.23) * mm});
            skLineSegment(sketch, "E1121", {"start": v(-1.13, 17.23) * mm, "end": v(-1.11, 16.94) * mm});
            skLineSegment(sketch, "E1122", {"start": v(-1.11, 16.94) * mm, "end": v(-1.09, 16.67) * mm});
            skLineSegment(sketch, "E1123", {"start": v(-1.09, 16.67) * mm, "end": v(-1.06, 16.42) * mm});
            skLineSegment(sketch, "E1124", {"start": v(-1.06, 16.42) * mm, "end": v(-1.03, 16.2) * mm});
            skLineSegment(sketch, "E1125", {"start": v(-1.03, 16.2) * mm, "end": v(-1, 15.98) * mm});
            skLineSegment(sketch, "E1126", {"start": v(-1, 15.98) * mm, "end": v(-0.96, 15.8) * mm});
            skLineSegment(sketch, "E1127", {"start": v(-0.96, 15.8) * mm, "end": v(-0.93, 15.62) * mm});
            skLineSegment(sketch, "E1128", {"start": v(-0.93, 15.62) * mm, "end": v(-0.9, 15.47) * mm});
            skLineSegment(sketch, "E1129", {"start": v(-0.9, 15.47) * mm, "end": v(-0.86, 15.33) * mm});
            skLineSegment(sketch, "E1130", {"start": v(-0.86, 15.33) * mm, "end": v(-0.83, 15.22) * mm});
            skLineSegment(sketch, "E1131", {"start": v(-0.83, 15.22) * mm, "end": v(-0.8, 15.12) * mm});
            skLineSegment(sketch, "E1132", {"start": v(-0.8, 15.12) * mm, "end": v(-0.78, 15.04) * mm});
            skLineSegment(sketch, "E1133", {"start": v(-0.78, 15.04) * mm, "end": v(-0.76, 14.98) * mm});
            skLineSegment(sketch, "E1134", {"start": v(-0.76, 14.98) * mm, "end": v(-0.75, 14.94) * mm});
            skLineSegment(sketch, "E1135", {"start": v(-0.75, 14.94) * mm, "end": v(-0.74, 14.91) * mm});
            skLineSegment(sketch, "E1136", {"start": v(-0.74, 14.91) * mm, "end": v(0.57, 11.58) * mm});
            skLineSegment(sketch, "E1137", {"start": v(0.57, 11.58) * mm, "end": v(-5.6, 8.6) * mm});
            skLineSegment(sketch, "E1138", {"start": v(-5.6, 8.6) * mm, "end": v(-7.38, 11.7) * mm});
            skLineSegment(sketch, "E1139", {"start": v(-7.38, 11.7) * mm, "end": v(-7.4, 11.73) * mm});
            skLineSegment(sketch, "E1140", {"start": v(-7.4, 11.73) * mm, "end": v(-7.42, 11.77) * mm});
            skLineSegment(sketch, "E1141", {"start": v(-7.42, 11.77) * mm, "end": v(-7.46, 11.82) * mm});
            skLineSegment(sketch, "E1142", {"start": v(-7.46, 11.82) * mm, "end": v(-7.5, 11.89) * mm});
            skLineSegment(sketch, "E1143", {"start": v(-7.5, 11.89) * mm, "end": v(-7.56, 11.97) * mm});
            skLineSegment(sketch, "E1144", {"start": v(-7.56, 11.97) * mm, "end": v(-7.64, 12.06) * mm});
            skLineSegment(sketch, "E1145", {"start": v(-7.64, 12.06) * mm, "end": v(-7.72, 12.17) * mm});
            skLineSegment(sketch, "E1146", {"start": v(-7.72, 12.17) * mm, "end": v(-7.82, 12.3) * mm});
            skLineSegment(sketch, "E1147", {"start": v(-7.82, 12.3) * mm, "end": v(-7.94, 12.43) * mm});
            skLineSegment(sketch, "E1148", {"start": v(-7.94, 12.43) * mm, "end": v(-8.07, 12.57) * mm});
            skLineSegment(sketch, "E1149", {"start": v(-8.07, 12.57) * mm, "end": v(-8.2, 12.73) * mm});
            skLineSegment(sketch, "E1150", {"start": v(-8.2, 12.73) * mm, "end": v(-8.37, 12.9) * mm});
            skLineSegment(sketch, "E1151", {"start": v(-8.37, 12.9) * mm, "end": v(-8.55, 13.08) * mm});
            skLineSegment(sketch, "E1152", {"start": v(-8.55, 13.08) * mm, "end": v(-8.74, 13.26) * mm});
            skLineSegment(sketch, "E1153", {"start": v(-8.74, 13.26) * mm, "end": v(-8.95, 13.46) * mm});
            skLineSegment(sketch, "E1154", {"start": v(-8.95, 13.46) * mm, "end": v(-9.18, 13.66) * mm});
            skLineSegment(sketch, "E1155", {"start": v(-9.18, 13.66) * mm, "end": v(-9.43, 13.87) * mm});
            skLineSegment(sketch, "E1156", {"start": v(-9.43, 13.87) * mm, "end": v(-9.7, 14.1) * mm});
            skLineSegment(sketch, "E1157", {"start": v(-9.7, 14.1) * mm, "end": v(-9.98, 14.32) * mm});
            skLineSegment(sketch, "E1158", {"start": v(-9.98, 14.32) * mm, "end": v(-10.28, 14.55) * mm});
            skLineSegment(sketch, "E1159", {"start": v(-10.28, 14.55) * mm, "end": v(-10.6, 14.79) * mm});
            skLineSegment(sketch, "E1160", {"start": v(-10.6, 14.79) * mm, "end": v(-10.95, 15.03) * mm});
            skLineSegment(sketch, "E1161", {"start": v(-10.95, 15.03) * mm, "end": v(-11.3, 15.27) * mm});
            skLineSegment(sketch, "E1162", {"start": v(-11.3, 15.27) * mm, "end": v(-11.7, 15.52) * mm});
            skLineSegment(sketch, "E1163", {"start": v(-11.7, 15.52) * mm, "end": v(-12.1, 15.77) * mm});
            skLineSegment(sketch, "E1164", {"start": v(-12.1, 15.77) * mm, "end": v(-12.52, 16.02) * mm});
            skLineSegment(sketch, "E1165", {"start": v(-12.52, 16.02) * mm, "end": v(-12.97, 16.27) * mm});
            skLineSegment(sketch, "E1166", {"start": v(-12.97, 16.27) * mm, "end": v(-13.43, 16.53) * mm});
            skLineSegment(sketch, "E1167", {"start": v(-13.43, 16.53) * mm, "end": v(-13.92, 16.78) * mm});
            skLineSegment(sketch, "E1168", {"start": v(-13.92, 16.78) * mm, "end": v(-14.43, 17.03) * mm});
            skLineSegment(sketch, "E1169", {"start": v(-14.43, 17.03) * mm, "end": v(-14.96, 17.28) * mm});
            skLineSegment(sketch, "E1170", {"start": v(-14.96, 17.28) * mm, "end": v(-15.41, 17.37) * mm});
            skLineSegment(sketch, "E1171", {"start": v(-15.41, 17.37) * mm, "end": v(-18.3, 15.3) * mm});
            skLineSegment(sketch, "E1172", {"start": v(-18.3, 15.3) * mm, "end": v(-18.35, 14.85) * mm});
            skLineSegment(sketch, "E1173", {"start": v(-18.35, 14.85) * mm, "end": v(-18.28, 14.26) * mm});
            skLineSegment(sketch, "E1174", {"start": v(-18.28, 14.26) * mm, "end": v(-18.2, 13.7) * mm});
            skLineSegment(sketch, "E1175", {"start": v(-18.2, 13.7) * mm, "end": v(-18.12, 13.16) * mm});
            skLineSegment(sketch, "E1176", {"start": v(-18.12, 13.16) * mm, "end": v(-18.03, 12.63) * mm});
            skLineSegment(sketch, "E1177", {"start": v(-18.03, 12.63) * mm, "end": v(-17.93, 12.13) * mm});
            skLineSegment(sketch, "E1178", {"start": v(-17.93, 12.13) * mm, "end": v(-17.82, 11.65) * mm});
            skLineSegment(sketch, "E1179", {"start": v(-17.82, 11.65) * mm, "end": v(-17.72, 11.18) * mm});
            skLineSegment(sketch, "E1180", {"start": v(-17.72, 11.18) * mm, "end": v(-17.6, 10.74) * mm});
            skLineSegment(sketch, "E1181", {"start": v(-17.6, 10.74) * mm, "end": v(-17.49, 10.32) * mm});
            skLineSegment(sketch, "E1182", {"start": v(-17.49, 10.32) * mm, "end": v(-17.37, 9.92) * mm});
            skLineSegment(sketch, "E1183", {"start": v(-17.37, 9.92) * mm, "end": v(-17.24, 9.54) * mm});
            skLineSegment(sketch, "E1184", {"start": v(-17.24, 9.54) * mm, "end": v(-17.12, 9.18) * mm});
            skLineSegment(sketch, "E1185", {"start": v(-17.12, 9.18) * mm, "end": v(-17, 8.84) * mm});
            skLineSegment(sketch, "E1186", {"start": v(-17, 8.84) * mm, "end": v(-16.87, 8.51) * mm});
            skLineSegment(sketch, "E1187", {"start": v(-16.87, 8.51) * mm, "end": v(-16.75, 8.21) * mm});
            skLineSegment(sketch, "E1188", {"start": v(-16.75, 8.21) * mm, "end": v(-16.63, 7.93) * mm});
            skLineSegment(sketch, "E1189", {"start": v(-16.63, 7.93) * mm, "end": v(-16.51, 7.67) * mm});
            skLineSegment(sketch, "E1190", {"start": v(-16.51, 7.67) * mm, "end": v(-16.4, 7.43) * mm});
            skLineSegment(sketch, "E1191", {"start": v(-16.4, 7.43) * mm, "end": v(-16.28, 7.2) * mm});
            skLineSegment(sketch, "E1192", {"start": v(-16.28, 7.2) * mm, "end": v(-16.18, 7) * mm});
            skLineSegment(sketch, "E1193", {"start": v(-16.18, 7) * mm, "end": v(-16.07, 6.81) * mm});
            skLineSegment(sketch, "E1194", {"start": v(-16.07, 6.81) * mm, "end": v(-15.98, 6.64) * mm});
            skLineSegment(sketch, "E1195", {"start": v(-15.98, 6.64) * mm, "end": v(-15.89, 6.5) * mm});
            skLineSegment(sketch, "E1196", {"start": v(-15.89, 6.5) * mm, "end": v(-15.8, 6.36) * mm});
            skLineSegment(sketch, "E1197", {"start": v(-15.8, 6.36) * mm, "end": v(-15.73, 6.24) * mm});
            skLineSegment(sketch, "E1198", {"start": v(-15.73, 6.24) * mm, "end": v(-15.66, 6.14) * mm});
            skLineSegment(sketch, "E1199", {"start": v(-15.66, 6.14) * mm, "end": v(-15.6, 6.06) * mm});
            skLineSegment(sketch, "E1200", {"start": v(-15.6, 6.06) * mm, "end": v(-15.55, 6) * mm});
            skLineSegment(sketch, "E1201", {"start": v(-15.55, 6) * mm, "end": v(-15.51, 5.94) * mm});
            skLineSegment(sketch, "E1202", {"start": v(-15.51, 5.94) * mm, "end": v(-15.48, 5.9) * mm});
            skLineSegment(sketch, "E1203", {"start": v(-15.48, 5.9) * mm, "end": v(-15.47, 5.89) * mm});
            skLineSegment(sketch, "E1204", {"start": v(-15.47, 5.89) * mm, "end": v(-13.1, 3.2) * mm});
            skLineSegment(sketch, "E1205", {"start": v(-13.1, 3.2) * mm, "end": v(-17.88, -1.7) * mm});
            skLineSegment(sketch, "E1206", {"start": v(-17.88, -1.7) * mm, "end": v(-20.62, 0.6) * mm});
            skLineSegment(sketch, "E1207", {"start": v(-20.62, 0.6) * mm, "end": v(-20.64, 0.62) * mm});
            skLineSegment(sketch, "E1208", {"start": v(-20.64, 0.62) * mm, "end": v(-20.67, 0.65) * mm});
            skLineSegment(sketch, "E1209", {"start": v(-20.67, 0.65) * mm, "end": v(-20.72, 0.69) * mm});
            skLineSegment(sketch, "E1210", {"start": v(-20.72, 0.69) * mm, "end": v(-20.8, 0.73) * mm});
            skLineSegment(sketch, "E1211", {"start": v(-20.8, 0.73) * mm, "end": v(-20.87, 0.79) * mm});
            skLineSegment(sketch, "E1212", {"start": v(-20.87, 0.79) * mm, "end": v(-20.98, 0.85) * mm});
            skLineSegment(sketch, "E1213", {"start": v(-20.98, 0.85) * mm, "end": v(-21.1, 0.93) * mm});
            skLineSegment(sketch, "E1214", {"start": v(-21.1, 0.93) * mm, "end": v(-21.23, 1) * mm});
            skLineSegment(sketch, "E1215", {"start": v(-21.23, 1) * mm, "end": v(-21.38, 1.1) * mm});
            skLineSegment(sketch, "E1216", {"start": v(-21.38, 1.1) * mm, "end": v(-21.55, 1.19) * mm});
            skLineSegment(sketch, "E1217", {"start": v(-21.55, 1.19) * mm, "end": v(-21.74, 1.28) * mm});
            skLineSegment(sketch, "E1218", {"start": v(-21.74, 1.28) * mm, "end": v(-21.95, 1.39) * mm});
            skLineSegment(sketch, "E1219", {"start": v(-21.95, 1.39) * mm, "end": v(-22.18, 1.5) * mm});
            skLineSegment(sketch, "E1220", {"start": v(-22.18, 1.5) * mm, "end": v(-22.42, 1.6) * mm});
            skLineSegment(sketch, "E1221", {"start": v(-22.42, 1.6) * mm, "end": v(-22.69, 1.71) * mm});
            skLineSegment(sketch, "E1222", {"start": v(-22.69, 1.71) * mm, "end": v(-22.97, 1.83) * mm});
            skLineSegment(sketch, "E1223", {"start": v(-22.97, 1.83) * mm, "end": v(-23.28, 1.94) * mm});
            skLineSegment(sketch, "E1224", {"start": v(-23.28, 1.94) * mm, "end": v(-23.6, 2.06) * mm});
            skLineSegment(sketch, "E1225", {"start": v(-23.6, 2.06) * mm, "end": v(-23.95, 2.17) * mm});
            skLineSegment(sketch, "E1226", {"start": v(-23.95, 2.17) * mm, "end": v(-24.3, 2.29) * mm});
            skLineSegment(sketch, "E1227", {"start": v(-24.3, 2.29) * mm, "end": v(-24.7, 2.4) * mm});
            skLineSegment(sketch, "E1228", {"start": v(-24.7, 2.4) * mm, "end": v(-25.1, 2.5) * mm});
            skLineSegment(sketch, "E1229", {"start": v(-25.1, 2.5) * mm, "end": v(-25.52, 2.61) * mm});
            skLineSegment(sketch, "E1230", {"start": v(-25.52, 2.61) * mm, "end": v(-25.97, 2.72) * mm});
            skLineSegment(sketch, "E1231", {"start": v(-25.97, 2.72) * mm, "end": v(-26.43, 2.81) * mm});
            skLineSegment(sketch, "E1232", {"start": v(-26.43, 2.81) * mm, "end": v(-26.92, 2.9) * mm});
            skLineSegment(sketch, "E1233", {"start": v(-26.92, 2.9) * mm, "end": v(-27.42, 2.99) * mm});
            skLineSegment(sketch, "E1234", {"start": v(-27.42, 2.99) * mm, "end": v(-27.95, 3.07) * mm});
            skLineSegment(sketch, "E1235", {"start": v(-27.95, 3.07) * mm, "end": v(-28.5, 3.14) * mm});
            skLineSegment(sketch, "E1236", {"start": v(-28.5, 3.14) * mm, "end": v(-29.06, 3.2) * mm});
            skLineSegment(sketch, "E1237", {"start": v(-29.06, 3.2) * mm, "end": v(-29.64, 3.25) * mm});
            skLineSegment(sketch, "E1238", {"start": v(-29.64, 3.25) * mm, "end": v(-30.1, 3.18) * mm});
            skLineSegment(sketch, "E1239", {"start": v(-30.1, 3.18) * mm, "end": v(-32.1, 0.25) * mm});
            skLineSegment(sketch, "E1240", {"start": v(-32.1, 0.25) * mm, "end": v(-32, -0.2) * mm});
            skLineSegment(sketch, "E1241", {"start": v(-32, -0.2) * mm, "end": v(-31.73, -0.72) * mm});
            skLineSegment(sketch, "E1242", {"start": v(-31.73, -0.72) * mm, "end": v(-31.46, -1.22) * mm});
            skLineSegment(sketch, "E1243", {"start": v(-31.46, -1.22) * mm, "end": v(-31.2, -1.7) * mm});
            skLineSegment(sketch, "E1244", {"start": v(-31.2, -1.7) * mm, "end": v(-30.93, -2.17) * mm});
            skLineSegment(sketch, "E1245", {"start": v(-30.93, -2.17) * mm, "end": v(-30.67, -2.6) * mm});
            skLineSegment(sketch, "E1246", {"start": v(-30.67, -2.6) * mm, "end": v(-30.4, -3.02) * mm});
            skLineSegment(sketch, "E1247", {"start": v(-30.4, -3.02) * mm, "end": v(-30.15, -3.42) * mm});
            skLineSegment(sketch, "E1248", {"start": v(-30.15, -3.42) * mm, "end": v(-29.89, -3.8) * mm});
            skLineSegment(sketch, "E1249", {"start": v(-29.89, -3.8) * mm, "end": v(-29.63, -4.15) * mm});
            skLineSegment(sketch, "E1250", {"start": v(-29.63, -4.15) * mm, "end": v(-29.38, -4.49) * mm});
            skLineSegment(sketch, "E1251", {"start": v(-29.38, -4.49) * mm, "end": v(-29.14, -4.8) * mm});
            skLineSegment(sketch, "E1252", {"start": v(-29.14, -4.8) * mm, "end": v(-28.9, -5.1) * mm});
            skLineSegment(sketch, "E1253", {"start": v(-28.9, -5.1) * mm, "end": v(-28.67, -5.38) * mm});
            skLineSegment(sketch, "E1254", {"start": v(-28.67, -5.38) * mm, "end": v(-28.44, -5.64) * mm});
            skLineSegment(sketch, "E1255", {"start": v(-28.44, -5.64) * mm, "end": v(-28.22, -5.88) * mm});
            skLineSegment(sketch, "E1256", {"start": v(-28.22, -5.88) * mm, "end": v(-28.01, -6.1) * mm});
            skLineSegment(sketch, "E1257", {"start": v(-28.01, -6.1) * mm, "end": v(-27.81, -6.31) * mm});
            skLineSegment(sketch, "E1258", {"start": v(-27.81, -6.31) * mm, "end": v(-27.62, -6.5) * mm});
            skLineSegment(sketch, "E1259", {"start": v(-27.62, -6.5) * mm, "end": v(-27.44, -6.67) * mm});
            skLineSegment(sketch, "E1260", {"start": v(-27.44, -6.67) * mm, "end": v(-27.27, -6.83) * mm});
            skLineSegment(sketch, "E1261", {"start": v(-27.27, -6.83) * mm, "end": v(-27.1, -6.97) * mm});
            skLineSegment(sketch, "E1262", {"start": v(-27.1, -6.97) * mm, "end": v(-26.96, -7.1) * mm});
            skLineSegment(sketch, "E1263", {"start": v(-26.96, -7.1) * mm, "end": v(-26.82, -7.2) * mm});
            skLineSegment(sketch, "E1264", {"start": v(-26.82, -7.2) * mm, "end": v(-26.7, -7.3) * mm});
            skLineSegment(sketch, "E1265", {"start": v(-26.7, -7.3) * mm, "end": v(-26.58, -7.38) * mm});
            skLineSegment(sketch, "E1266", {"start": v(-26.58, -7.38) * mm, "end": v(-26.49, -7.45) * mm});
            skLineSegment(sketch, "E1267", {"start": v(-26.49, -7.45) * mm, "end": v(-26.4, -7.51) * mm});
            skLineSegment(sketch, "E1268", {"start": v(-26.4, -7.51) * mm, "end": v(-26.34, -7.56) * mm});
            skLineSegment(sketch, "E1269", {"start": v(-26.34, -7.56) * mm, "end": v(-26.28, -7.59) * mm});
            skLineSegment(sketch, "E1270", {"start": v(-26.28, -7.59) * mm, "end": v(-26.24, -7.61) * mm});
            skLineSegment(sketch, "E1271", {"start": v(-26.24, -7.61) * mm, "end": v(-26.22, -7.63) * mm});
            skLineSegment(sketch, "E1272", {"start": v(-26.22, -7.63) * mm, "end": v(-23.08, -9.33) * mm});
            skLineSegment(sketch, "E1273", {"start": v(-23.08, -9.33) * mm, "end": v(-25.9, -15.58) * mm});
            skLineSegment(sketch, "E1274", {"start": v(-25.9, -15.58) * mm, "end": v(-29.25, -14.35) * mm});
            skLineSegment(sketch, "E1275", {"start": v(-29.25, -14.35) * mm, "end": v(-29.28, -14.35) * mm});
            skLineSegment(sketch, "E1276", {"start": v(-29.28, -14.35) * mm, "end": v(-29.32, -14.33) * mm});
            skLineSegment(sketch, "E1277", {"start": v(-29.32, -14.33) * mm, "end": v(-29.38, -14.31) * mm});
            skLineSegment(sketch, "E1278", {"start": v(-29.38, -14.31) * mm, "end": v(-29.46, -14.3) * mm});
            skLineSegment(sketch, "E1279", {"start": v(-29.46, -14.3) * mm, "end": v(-29.56, -14.27) * mm});
            skLineSegment(sketch, "E1280", {"start": v(-29.56, -14.27) * mm, "end": v(-29.68, -14.24) * mm});
            skLineSegment(sketch, "E1281", {"start": v(-29.68, -14.24) * mm, "end": v(-29.81, -14.21) * mm});
            skLineSegment(sketch, "E1282", {"start": v(-29.81, -14.21) * mm, "end": v(-29.96, -14.18) * mm});
            skLineSegment(sketch, "E1283", {"start": v(-29.96, -14.18) * mm, "end": v(-30.14, -14.16) * mm});
            skLineSegment(sketch, "E1284", {"start": v(-30.14, -14.16) * mm, "end": v(-30.33, -14.13) * mm});
            skLineSegment(sketch, "E1285", {"start": v(-30.33, -14.13) * mm, "end": v(-30.54, -14.1) * mm});
            skLineSegment(sketch, "E1286", {"start": v(-30.54, -14.1) * mm, "end": v(-30.77, -14.07) * mm});
            skLineSegment(sketch, "E1287", {"start": v(-30.77, -14.07) * mm, "end": v(-31.02, -14.05) * mm});
            skLineSegment(sketch, "E1288", {"start": v(-31.02, -14.05) * mm, "end": v(-31.3, -14.03) * mm});
            skLineSegment(sketch, "E1289", {"start": v(-31.3, -14.03) * mm, "end": v(-31.58, -14.02) * mm});
            skLineSegment(sketch, "E1290", {"start": v(-31.58, -14.02) * mm, "end": v(-31.88, -14) * mm});
            skLineSegment(sketch, "E1291", {"start": v(-31.88, -14) * mm, "end": v(-32.21, -14) * mm});
            skLineSegment(sketch, "E1292", {"start": v(-32.21, -14) * mm, "end": v(-32.55, -14) * mm});
            skLineSegment(sketch, "E1293", {"start": v(-32.55, -14) * mm, "end": v(-32.92, -14.02) * mm});
            skLineSegment(sketch, "E1294", {"start": v(-32.92, -14.02) * mm, "end": v(-33.3, -14.04) * mm});
            skLineSegment(sketch, "E1295", {"start": v(-33.3, -14.04) * mm, "end": v(-33.7, -14.06) * mm});
            skLineSegment(sketch, "E1296", {"start": v(-33.7, -14.06) * mm, "end": v(-34.11, -14.1) * mm});
            skLineSegment(sketch, "E1297", {"start": v(-34.11, -14.1) * mm, "end": v(-34.55, -14.14) * mm});
            skLineSegment(sketch, "E1298", {"start": v(-34.55, -14.14) * mm, "end": v(-35, -14.2) * mm});
            skLineSegment(sketch, "E1299", {"start": v(-35, -14.2) * mm, "end": v(-35.47, -14.27) * mm});
            skLineSegment(sketch, "E1300", {"start": v(-35.47, -14.27) * mm, "end": v(-35.96, -14.35) * mm});
            skLineSegment(sketch, "E1301", {"start": v(-35.96, -14.35) * mm, "end": v(-36.46, -14.44) * mm});
            skLineSegment(sketch, "E1302", {"start": v(-36.46, -14.44) * mm, "end": v(-36.98, -14.55) * mm});
            skLineSegment(sketch, "E1303", {"start": v(-36.98, -14.55) * mm, "end": v(-37.52, -14.67) * mm});
            skLineSegment(sketch, "E1304", {"start": v(-37.52, -14.67) * mm, "end": v(-38.07, -14.8) * mm});
            skLineSegment(sketch, "E1305", {"start": v(-38.07, -14.8) * mm, "end": v(-38.64, -14.95) * mm});
            skLineSegment(sketch, "E1306", {"start": v(-38.64, -14.95) * mm, "end": v(-39.04, -15.17) * mm});
            skLineSegment(sketch, "E1307", {"start": v(-39.04, -15.17) * mm, "end": v(-39.92, -18.61) * mm});
            skLineSegment(sketch, "E1308", {"start": v(-39.92, -18.61) * mm, "end": v(-39.67, -19) * mm});
            skLineSegment(sketch, "E1309", {"start": v(-39.67, -19) * mm, "end": v(-39.24, -19.4) * mm});
            skLineSegment(sketch, "E1310", {"start": v(-39.24, -19.4) * mm, "end": v(-38.82, -19.78) * mm});
            skLineSegment(sketch, "E1311", {"start": v(-38.82, -19.78) * mm, "end": v(-38.4, -20.14) * mm});
            skLineSegment(sketch, "E1312", {"start": v(-38.4, -20.14) * mm, "end": v(-38, -20.49) * mm});
            skLineSegment(sketch, "E1313", {"start": v(-38, -20.49) * mm, "end": v(-37.6, -20.8) * mm});
            skLineSegment(sketch, "E1314", {"start": v(-37.6, -20.8) * mm, "end": v(-37.21, -21.11) * mm});
            skLineSegment(sketch, "E1315", {"start": v(-37.21, -21.11) * mm, "end": v(-36.83, -21.4) * mm});
            skLineSegment(sketch, "E1316", {"start": v(-36.83, -21.4) * mm, "end": v(-36.46, -21.66) * mm});
            skLineSegment(sketch, "E1317", {"start": v(-36.46, -21.66) * mm, "end": v(-36.1, -21.9) * mm});
            skLineSegment(sketch, "E1318", {"start": v(-36.1, -21.9) * mm, "end": v(-35.75, -22.14) * mm});
            skLineSegment(sketch, "E1319", {"start": v(-35.75, -22.14) * mm, "end": v(-35.41, -22.35) * mm});
            skLineSegment(sketch, "E1320", {"start": v(-35.41, -22.35) * mm, "end": v(-35.08, -22.55) * mm});
            skLineSegment(sketch, "E1321", {"start": v(-35.08, -22.55) * mm, "end": v(-34.77, -22.73) * mm});
            skLineSegment(sketch, "E1322", {"start": v(-34.77, -22.73) * mm, "end": v(-34.47, -22.9) * mm});
            skLineSegment(sketch, "E1323", {"start": v(-34.47, -22.9) * mm, "end": v(-34.18, -23.05) * mm});
            skLineSegment(sketch, "E1324", {"start": v(-34.18, -23.05) * mm, "end": v(-33.9, -23.19) * mm});
            skLineSegment(sketch, "E1325", {"start": v(-33.9, -23.19) * mm, "end": v(-33.65, -23.31) * mm});
            skLineSegment(sketch, "E1326", {"start": v(-33.65, -23.31) * mm, "end": v(-33.4, -23.42) * mm});
            skLineSegment(sketch, "E1327", {"start": v(-33.4, -23.42) * mm, "end": v(-33.17, -23.52) * mm});
            skLineSegment(sketch, "E1328", {"start": v(-33.17, -23.52) * mm, "end": v(-32.96, -23.61) * mm});
            skLineSegment(sketch, "E1329", {"start": v(-32.96, -23.61) * mm, "end": v(-32.76, -23.69) * mm});
            skLineSegment(sketch, "E1330", {"start": v(-32.76, -23.69) * mm, "end": v(-32.58, -23.76) * mm});
            skLineSegment(sketch, "E1331", {"start": v(-32.58, -23.76) * mm, "end": v(-32.41, -23.81) * mm});
            skLineSegment(sketch, "E1332", {"start": v(-32.41, -23.81) * mm, "end": v(-32.26, -23.86) * mm});
            skLineSegment(sketch, "E1333", {"start": v(-32.26, -23.86) * mm, "end": v(-32.13, -23.9) * mm});
            skLineSegment(sketch, "E1334", {"start": v(-32.13, -23.9) * mm, "end": v(-32.01, -23.93) * mm});
            skLineSegment(sketch, "E1335", {"start": v(-32.01, -23.93) * mm, "end": v(-31.92, -23.96) * mm});
            skLineSegment(sketch, "E1336", {"start": v(-31.92, -23.96) * mm, "end": v(-31.84, -23.98) * mm});
            skLineSegment(sketch, "E1337", {"start": v(-31.84, -23.98) * mm, "end": v(-31.77, -24) * mm});
            skLineSegment(sketch, "E1338", {"start": v(-31.77, -24) * mm, "end": v(-31.73, -24) * mm});
            skLineSegment(sketch, "E1339", {"start": v(-31.73, -24) * mm, "end": v(-31.7, -24) * mm});
            skLineSegment(sketch, "E1340", {"start": v(-31.7, -24) * mm, "end": v(-28.17, -24.53) * mm});
            skLineSegment(sketch, "E1341", {"start": v(-28.17, -24.53) * mm, "end": v(-28.67, -31.36) * mm});
            skLineSegment(sketch, "E1342", {"start": v(-28.67, -31.36) * mm, "end": v(-32.25, -31.36) * mm});
            skLineSegment(sketch, "E1343", {"start": v(-32.25, -31.36) * mm, "end": v(-32.28, -31.36) * mm});
            skLineSegment(sketch, "E1344", {"start": v(-32.28, -31.36) * mm, "end": v(-32.32, -31.37) * mm});
            skLineSegment(sketch, "E1345", {"start": v(-32.32, -31.37) * mm, "end": v(-32.39, -31.37) * mm});
            skLineSegment(sketch, "E1346", {"start": v(-32.39, -31.37) * mm, "end": v(-32.47, -31.38) * mm});
            skLineSegment(sketch, "E1347", {"start": v(-32.47, -31.38) * mm, "end": v(-32.57, -31.39) * mm});
            skLineSegment(sketch, "E1348", {"start": v(-32.57, -31.39) * mm, "end": v(-32.69, -31.4) * mm});
            skLineSegment(sketch, "E1349", {"start": v(-32.69, -31.4) * mm, "end": v(-32.82, -31.42) * mm});
            skLineSegment(sketch, "E1350", {"start": v(-32.82, -31.42) * mm, "end": v(-32.98, -31.45) * mm});
            skLineSegment(sketch, "E1351", {"start": v(-32.98, -31.45) * mm, "end": v(-33.15, -31.48) * mm});
            skLineSegment(sketch, "E1352", {"start": v(-33.15, -31.48) * mm, "end": v(-33.34, -31.52) * mm});
            skLineSegment(sketch, "E1353", {"start": v(-33.34, -31.52) * mm, "end": v(-33.55, -31.57) * mm});
            skLineSegment(sketch, "E1354", {"start": v(-33.55, -31.57) * mm, "end": v(-33.78, -31.62) * mm});
            skLineSegment(sketch, "E1355", {"start": v(-33.78, -31.62) * mm, "end": v(-34.02, -31.69) * mm});
            skLineSegment(sketch, "E1356", {"start": v(-34.02, -31.69) * mm, "end": v(-34.28, -31.76) * mm});
            skLineSegment(sketch, "E1357", {"start": v(-34.28, -31.76) * mm, "end": v(-34.55, -31.84) * mm});
            skLineSegment(sketch, "E1358", {"start": v(-34.55, -31.84) * mm, "end": v(-34.84, -31.94) * mm});
            skLineSegment(sketch, "E1359", {"start": v(-34.84, -31.94) * mm, "end": v(-35.15, -32.05) * mm});
            skLineSegment(sketch, "E1360", {"start": v(-35.15, -32.05) * mm, "end": v(-35.47, -32.17) * mm});
            skLineSegment(sketch, "E1361", {"start": v(-35.47, -32.17) * mm, "end": v(-35.8, -32.3) * mm});
            skLineSegment(sketch, "E1362", {"start": v(-35.8, -32.3) * mm, "end": v(-36.16, -32.45) * mm});
            skLineSegment(sketch, "E1363", {"start": v(-36.16, -32.45) * mm, "end": v(-36.53, -32.61) * mm});
            skLineSegment(sketch, "E1364", {"start": v(-36.53, -32.61) * mm, "end": v(-36.9, -32.79) * mm});
            skLineSegment(sketch, "E1365", {"start": v(-36.9, -32.79) * mm, "end": v(-37.3, -32.98) * mm});
            skLineSegment(sketch, "E1366", {"start": v(-37.3, -32.98) * mm, "end": v(-37.7, -33.19) * mm});
            skLineSegment(sketch, "E1367", {"start": v(-37.7, -33.19) * mm, "end": v(-38.13, -33.41) * mm});
            skLineSegment(sketch, "E1368", {"start": v(-38.13, -33.41) * mm, "end": v(-38.56, -33.65) * mm});
            skLineSegment(sketch, "E1369", {"start": v(-38.56, -33.65) * mm, "end": v(-39, -33.91) * mm});
            skLineSegment(sketch, "E1370", {"start": v(-39, -33.91) * mm, "end": v(-39.45, -34.2) * mm});
            skLineSegment(sketch, "E1371", {"start": v(-39.45, -34.2) * mm, "end": v(-39.91, -34.49) * mm});
            skLineSegment(sketch, "E1372", {"start": v(-39.91, -34.49) * mm, "end": v(-40.39, -34.8) * mm});
            skLineSegment(sketch, "E1373", {"start": v(-40.39, -34.8) * mm, "end": v(-40.87, -35.14) * mm});
            skLineSegment(sketch, "E1374", {"start": v(-40.87, -35.14) * mm, "end": v(-41.17, -35.48) * mm});
            skLineSegment(sketch, "E1375", {"start": v(-41.17, -35.48) * mm, "end": v(-40.82, -39.01) * mm});
            skLineSegment(sketch, "E1376", {"start": v(-40.82, -39.01) * mm, "end": v(-40.45, -39.29) * mm});
            skLineSegment(sketch, "E1377", {"start": v(-40.45, -39.29) * mm, "end": v(-39.91, -39.52) * mm});
            skLineSegment(sketch, "E1378", {"start": v(-39.91, -39.52) * mm, "end": v(-39.39, -39.74) * mm});
            skLineSegment(sketch, "E1379", {"start": v(-39.39, -39.74) * mm, "end": v(-38.87, -39.93) * mm});
            skLineSegment(sketch, "E1380", {"start": v(-38.87, -39.93) * mm, "end": v(-38.37, -40.12) * mm});
            skLineSegment(sketch, "E1381", {"start": v(-38.37, -40.12) * mm, "end": v(-37.89, -40.28) * mm});
            skLineSegment(sketch, "E1382", {"start": v(-37.89, -40.28) * mm, "end": v(-37.42, -40.43) * mm});
            skLineSegment(sketch, "E1383", {"start": v(-37.42, -40.43) * mm, "end": v(-36.96, -40.57) * mm});
            skLineSegment(sketch, "E1384", {"start": v(-36.96, -40.57) * mm, "end": v(-36.52, -40.7) * mm});
            skLineSegment(sketch, "E1385", {"start": v(-36.52, -40.7) * mm, "end": v(-36.1, -40.8) * mm});
            skLineSegment(sketch, "E1386", {"start": v(-36.1, -40.8) * mm, "end": v(-35.7, -40.9) * mm});
            skLineSegment(sketch, "E1387", {"start": v(-35.7, -40.9) * mm, "end": v(-35.3, -40.99) * mm});
            skLineSegment(sketch, "E1388", {"start": v(-35.3, -40.99) * mm, "end": v(-34.93, -41.06) * mm});
            skLineSegment(sketch, "E1389", {"start": v(-34.93, -41.06) * mm, "end": v(-34.57, -41.12) * mm});
            skLineSegment(sketch, "E1390", {"start": v(-34.57, -41.12) * mm, "end": v(-34.23, -41.18) * mm});
            skLineSegment(sketch, "E1391", {"start": v(-34.23, -41.18) * mm, "end": v(-33.9, -41.22) * mm});
            skLineSegment(sketch, "E1392", {"start": v(-33.9, -41.22) * mm, "end": v(-33.6, -41.26) * mm});
            skLineSegment(sketch, "E1393", {"start": v(-33.6, -41.26) * mm, "end": v(-33.32, -41.29) * mm});
            skLineSegment(sketch, "E1394", {"start": v(-33.32, -41.29) * mm, "end": v(-33.05, -41.3) * mm});
            skLineSegment(sketch, "E1395", {"start": v(-33.05, -41.3) * mm, "end": v(-32.8, -41.32) * mm});
            skLineSegment(sketch, "E1396", {"start": v(-32.8, -41.32) * mm, "end": v(-32.57, -41.33) * mm});
            skLineSegment(sketch, "E1397", {"start": v(-32.57, -41.33) * mm, "end": v(-32.35, -41.34) * mm});
            skLineSegment(sketch, "E1398", {"start": v(-32.35, -41.34) * mm, "end": v(-32.16, -41.34) * mm});
            skLineSegment(sketch, "E1399", {"start": v(-32.16, -41.34) * mm, "end": v(-31.98, -41.33) * mm});
            skLineSegment(sketch, "E1400", {"start": v(-31.98, -41.33) * mm, "end": v(-31.83, -41.33) * mm});
            skLineSegment(sketch, "E1401", {"start": v(-31.83, -41.33) * mm, "end": v(-31.69, -41.32) * mm});
            skLineSegment(sketch, "E1402", {"start": v(-31.69, -41.32) * mm, "end": v(-31.57, -41.3) * mm});
            skLineSegment(sketch, "E1403", {"start": v(-31.57, -41.3) * mm, "end": v(-31.47, -41.3) * mm});
            skLineSegment(sketch, "E1404", {"start": v(-31.47, -41.3) * mm, "end": v(-31.39, -41.3) * mm});
            skLineSegment(sketch, "E1405", {"start": v(-31.39, -41.3) * mm, "end": v(-31.32, -41.28) * mm});
            skLineSegment(sketch, "E1406", {"start": v(-31.32, -41.28) * mm, "end": v(-31.28, -41.28) * mm});
            skLineSegment(sketch, "E1407", {"start": v(-31.28, -41.28) * mm, "end": v(-31.25, -41.27) * mm});
            skLineSegment(sketch, "E1408", {"start": v(-31.25, -41.27) * mm, "end": v(-27.75, -40.56) * mm});
            skLineSegment(sketch, "E1409", {"start": v(-27.75, -40.56) * mm, "end": v(-25.9, -47.15) * mm});
            skLineSegment(sketch, "E1410", {"start": v(-25.9, -47.15) * mm, "end": v(-29.25, -48.37) * mm});
            skLineSegment(sketch, "E1411", {"start": v(-29.25, -48.37) * mm, "end": v(-29.28, -48.38) * mm});
            skLineSegment(sketch, "E1412", {"start": v(-29.28, -48.38) * mm, "end": v(-29.32, -48.4) * mm});
            skLineSegment(sketch, "E1413", {"start": v(-29.32, -48.4) * mm, "end": v(-29.38, -48.43) * mm});
            skLineSegment(sketch, "E1414", {"start": v(-29.38, -48.43) * mm, "end": v(-29.45, -48.46) * mm});
            skLineSegment(sketch, "E1415", {"start": v(-29.45, -48.46) * mm, "end": v(-29.54, -48.5) * mm});
            skLineSegment(sketch, "E1416", {"start": v(-29.54, -48.5) * mm, "end": v(-29.65, -48.56) * mm});
            skLineSegment(sketch, "E1417", {"start": v(-29.65, -48.56) * mm, "end": v(-29.77, -48.62) * mm});
            skLineSegment(sketch, "E1418", {"start": v(-29.77, -48.62) * mm, "end": v(-29.9, -48.7) * mm});
            skLineSegment(sketch, "E1419", {"start": v(-29.9, -48.7) * mm, "end": v(-30.06, -48.8) * mm});
            skLineSegment(sketch, "E1420", {"start": v(-30.06, -48.8) * mm, "end": v(-30.22, -48.9) * mm});
            skLineSegment(sketch, "E1421", {"start": v(-30.22, -48.9) * mm, "end": v(-30.4, -49) * mm});
            skLineSegment(sketch, "E1422", {"start": v(-30.4, -49) * mm, "end": v(-30.6, -49.14) * mm});
            skLineSegment(sketch, "E1423", {"start": v(-30.6, -49.14) * mm, "end": v(-30.8, -49.28) * mm});
            skLineSegment(sketch, "E1424", {"start": v(-30.8, -49.28) * mm, "end": v(-31.02, -49.44) * mm});
            skLineSegment(sketch, "E1425", {"start": v(-31.02, -49.44) * mm, "end": v(-31.25, -49.61) * mm});
            skLineSegment(sketch, "E1426", {"start": v(-31.25, -49.61) * mm, "end": v(-31.5, -49.8) * mm});
            skLineSegment(sketch, "E1427", {"start": v(-31.5, -49.8) * mm, "end": v(-31.74, -50) * mm});
            skLineSegment(sketch, "E1428", {"start": v(-31.74, -50) * mm, "end": v(-32, -50.23) * mm});
            skLineSegment(sketch, "E1429", {"start": v(-32, -50.23) * mm, "end": v(-32.27, -50.47) * mm});
            skLineSegment(sketch, "E1430", {"start": v(-32.27, -50.47) * mm, "end": v(-32.56, -50.73) * mm});
            skLineSegment(sketch, "E1431", {"start": v(-32.56, -50.73) * mm, "end": v(-32.84, -51) * mm});
            skLineSegment(sketch, "E1432", {"start": v(-32.84, -51) * mm, "end": v(-33.14, -51.3) * mm});
            skLineSegment(sketch, "E1433", {"start": v(-33.14, -51.3) * mm, "end": v(-33.45, -51.62) * mm});
            skLineSegment(sketch, "E1434", {"start": v(-33.45, -51.62) * mm, "end": v(-33.76, -51.95) * mm});
            skLineSegment(sketch, "E1435", {"start": v(-33.76, -51.95) * mm, "end": v(-34.07, -52.3) * mm});
            skLineSegment(sketch, "E1436", {"start": v(-34.07, -52.3) * mm, "end": v(-34.4, -52.68) * mm});
            skLineSegment(sketch, "E1437", {"start": v(-34.4, -52.68) * mm, "end": v(-34.72, -53.08) * mm});
            skLineSegment(sketch, "E1438", {"start": v(-34.72, -53.08) * mm, "end": v(-35.05, -53.5) * mm});
            skLineSegment(sketch, "E1439", {"start": v(-35.05, -53.5) * mm, "end": v(-35.38, -53.93) * mm});
            skLineSegment(sketch, "E1440", {"start": v(-35.38, -53.93) * mm, "end": v(-35.72, -54.39) * mm});
            skLineSegment(sketch, "E1441", {"start": v(-35.72, -54.39) * mm, "end": v(-36.06, -54.87) * mm});
            skLineSegment(sketch, "E1442", {"start": v(-36.06, -54.87) * mm, "end": v(-36.22, -55.3) * mm});
            skLineSegment(sketch, "E1443", {"start": v(-36.22, -55.3) * mm, "end": v(-34.68, -58.49) * mm});
            skLineSegment(sketch, "E1444", {"start": v(-34.68, -58.49) * mm, "end": v(-34.25, -58.62) * mm});
            skLineSegment(sketch, "E1445", {"start": v(-34.25, -58.62) * mm, "end": v(-33.66, -58.66) * mm});
            skLineSegment(sketch, "E1446", {"start": v(-33.66, -58.66) * mm, "end": v(-33.1, -58.68) * mm});
            skLineSegment(sketch, "E1447", {"start": v(-33.1, -58.68) * mm, "end": v(-32.54, -58.7) * mm});
            skLineSegment(sketch, "E1448", {"start": v(-32.54, -58.7) * mm, "end": v(-32.01, -58.7) * mm});
            skLineSegment(sketch, "E1449", {"start": v(-32.01, -58.7) * mm, "end": v(-31.5, -58.68) * mm});
            skLineSegment(sketch, "E1450", {"start": v(-31.5, -58.68) * mm, "end": v(-31, -58.66) * mm});
            skLineSegment(sketch, "E1451", {"start": v(-31, -58.66) * mm, "end": v(-30.53, -58.64) * mm});
            skLineSegment(sketch, "E1452", {"start": v(-30.53, -58.64) * mm, "end": v(-30.08, -58.6) * mm});
            skLineSegment(sketch, "E1453", {"start": v(-30.08, -58.6) * mm, "end": v(-29.64, -58.56) * mm});
            skLineSegment(sketch, "E1454", {"start": v(-29.64, -58.56) * mm, "end": v(-29.22, -58.51) * mm});
            skLineSegment(sketch, "E1455", {"start": v(-29.22, -58.51) * mm, "end": v(-28.83, -58.46) * mm});
            skLineSegment(sketch, "E1456", {"start": v(-28.83, -58.46) * mm, "end": v(-28.45, -58.4) * mm});
            skLineSegment(sketch, "E1457", {"start": v(-28.45, -58.4) * mm, "end": v(-28.1, -58.34) * mm});
            skLineSegment(sketch, "E1458", {"start": v(-28.1, -58.34) * mm, "end": v(-27.76, -58.27) * mm});
            skLineSegment(sketch, "E1459", {"start": v(-27.76, -58.27) * mm, "end": v(-27.44, -58.2) * mm});
            skLineSegment(sketch, "E1460", {"start": v(-27.44, -58.2) * mm, "end": v(-27.14, -58.13) * mm});
            skLineSegment(sketch, "E1461", {"start": v(-27.14, -58.13) * mm, "end": v(-26.86, -58.06) * mm});
            skLineSegment(sketch, "E1462", {"start": v(-26.86, -58.06) * mm, "end": v(-26.6, -57.99) * mm});
            skLineSegment(sketch, "E1463", {"start": v(-26.6, -57.99) * mm, "end": v(-26.36, -57.92) * mm});
            skLineSegment(sketch, "E1464", {"start": v(-26.36, -57.92) * mm, "end": v(-26.14, -57.85) * mm});
            skLineSegment(sketch, "E1465", {"start": v(-26.14, -57.85) * mm, "end": v(-25.94, -57.78) * mm});
            skLineSegment(sketch, "E1466", {"start": v(-25.94, -57.78) * mm, "end": v(-25.76, -57.71) * mm});
            skLineSegment(sketch, "E1467", {"start": v(-25.76, -57.71) * mm, "end": v(-25.6, -57.65) * mm});
            skLineSegment(sketch, "E1468", {"start": v(-25.6, -57.65) * mm, "end": v(-25.45, -57.6) * mm});
            skLineSegment(sketch, "E1469", {"start": v(-25.45, -57.6) * mm, "end": v(-25.32, -57.54) * mm});
            skLineSegment(sketch, "E1470", {"start": v(-25.32, -57.54) * mm, "end": v(-25.2, -57.49) * mm});
            skLineSegment(sketch, "E1471", {"start": v(-25.2, -57.49) * mm, "end": v(-25.12, -57.44) * mm});
            skLineSegment(sketch, "E1472", {"start": v(-25.12, -57.44) * mm, "end": v(-25.05, -57.4) * mm});
            skLineSegment(sketch, "E1473", {"start": v(-25.05, -57.4) * mm, "end": v(-24.99, -57.38) * mm});
            skLineSegment(sketch, "E1474", {"start": v(-24.99, -57.38) * mm, "end": v(-24.95, -57.36) * mm});
            skLineSegment(sketch, "E1475", {"start": v(-24.95, -57.36) * mm, "end": v(-24.93, -57.34) * mm});
            skLineSegment(sketch, "E1476", {"start": v(-24.93, -57.34) * mm, "end": v(-21.88, -55.47) * mm});
            skLineSegment(sketch, "E1477", {"start": v(-21.88, -55.47) * mm, "end": v(-17.88, -61.03) * mm});
            skLineSegment(sketch, "E1478", {"start": v(-17.88, -61.03) * mm, "end": v(-20.62, -63.33) * mm});
            skLineSegment(sketch, "E1479", {"start": v(-20.62, -63.33) * mm, "end": v(-20.64, -63.35) * mm});
            skLineSegment(sketch, "E1480", {"start": v(-20.64, -63.35) * mm, "end": v(-20.67, -63.38) * mm});
            skLineSegment(sketch, "E1481", {"start": v(-20.67, -63.38) * mm, "end": v(-20.71, -63.42) * mm});
            skLineSegment(sketch, "E1482", {"start": v(-20.71, -63.42) * mm, "end": v(-20.77, -63.48) * mm});
            skLineSegment(sketch, "E1483", {"start": v(-20.77, -63.48) * mm, "end": v(-20.84, -63.55) * mm});
            skLineSegment(sketch, "E1484", {"start": v(-20.84, -63.55) * mm, "end": v(-20.92, -63.64) * mm});
            skLineSegment(sketch, "E1485", {"start": v(-20.92, -63.64) * mm, "end": v(-21.02, -63.74) * mm});
            skLineSegment(sketch, "E1486", {"start": v(-21.02, -63.74) * mm, "end": v(-21.12, -63.86) * mm});
            skLineSegment(sketch, "E1487", {"start": v(-21.12, -63.86) * mm, "end": v(-21.23, -64) * mm});
            skLineSegment(sketch, "E1488", {"start": v(-21.23, -64) * mm, "end": v(-21.35, -64.15) * mm});
            skLineSegment(sketch, "E1489", {"start": v(-21.35, -64.15) * mm, "end": v(-21.48, -64.32) * mm});
            skLineSegment(sketch, "E1490", {"start": v(-21.48, -64.32) * mm, "end": v(-21.62, -64.5) * mm});
            skLineSegment(sketch, "E1491", {"start": v(-21.62, -64.5) * mm, "end": v(-21.76, -64.71) * mm});
            skLineSegment(sketch, "E1492", {"start": v(-21.76, -64.71) * mm, "end": v(-21.91, -64.94) * mm});
            skLineSegment(sketch, "E1493", {"start": v(-21.91, -64.94) * mm, "end": v(-22.07, -65.18) * mm});
            skLineSegment(sketch, "E1494", {"start": v(-22.07, -65.18) * mm, "end": v(-22.23, -65.44) * mm});
            skLineSegment(sketch, "E1495", {"start": v(-22.23, -65.44) * mm, "end": v(-22.4, -65.72) * mm});
            skLineSegment(sketch, "E1496", {"start": v(-22.4, -65.72) * mm, "end": v(-22.57, -66.02) * mm});
            skLineSegment(sketch, "E1497", {"start": v(-22.57, -66.02) * mm, "end": v(-22.74, -66.34) * mm});
            skLineSegment(sketch, "E1498", {"start": v(-22.74, -66.34) * mm, "end": v(-22.91, -66.68) * mm});
            skLineSegment(sketch, "E1499", {"start": v(-22.91, -66.68) * mm, "end": v(-23.1, -67.04) * mm});
            skLineSegment(sketch, "E1500", {"start": v(-23.1, -67.04) * mm, "end": v(-23.27, -67.41) * mm});
            skLineSegment(sketch, "E1501", {"start": v(-23.27, -67.41) * mm, "end": v(-23.45, -67.81) * mm});
            skLineSegment(sketch, "E1502", {"start": v(-23.45, -67.81) * mm, "end": v(-23.62, -68.23) * mm});
            skLineSegment(sketch, "E1503", {"start": v(-23.62, -68.23) * mm, "end": v(-23.8, -68.68) * mm});
            skLineSegment(sketch, "E1504", {"start": v(-23.8, -68.68) * mm, "end": v(-23.97, -69.14) * mm});
            skLineSegment(sketch, "E1505", {"start": v(-23.97, -69.14) * mm, "end": v(-24.15, -69.62) * mm});
            skLineSegment(sketch, "E1506", {"start": v(-24.15, -69.62) * mm, "end": v(-24.31, -70.12) * mm});
            skLineSegment(sketch, "E1507", {"start": v(-24.31, -70.12) * mm, "end": v(-24.48, -70.65) * mm});
            skLineSegment(sketch, "E1508", {"start": v(-24.48, -70.65) * mm, "end": v(-24.64, -71.2) * mm});
            skLineSegment(sketch, "E1509", {"start": v(-24.64, -71.2) * mm, "end": v(-24.79, -71.76) * mm});
            skLineSegment(sketch, "E1510", {"start": v(-24.79, -71.76) * mm, "end": v(-24.8, -72.22) * mm});
            skLineSegment(sketch, "E1511", {"start": v(-24.8, -72.22) * mm, "end": v(-22.26, -74.7) * mm});
            skLineSegment(sketch, "E1512", {"start": v(-22.26, -74.7) * mm, "end": v(-21.8, -74.67) * mm});
            skLineSegment(sketch, "E1513", {"start": v(-21.8, -74.67) * mm, "end": v(-21.24, -74.5) * mm});
            skLineSegment(sketch, "E1514", {"start": v(-21.24, -74.5) * mm, "end": v(-20.7, -74.33) * mm});
            skLineSegment(sketch, "E1515", {"start": v(-20.7, -74.33) * mm, "end": v(-20.18, -74.15) * mm});
            skLineSegment(sketch, "E1516", {"start": v(-20.18, -74.15) * mm, "end": v(-19.68, -73.97) * mm});
            skLineSegment(sketch, "E1517", {"start": v(-19.68, -73.97) * mm, "end": v(-19.2, -73.79) * mm});
            skLineSegment(sketch, "E1518", {"start": v(-19.2, -73.79) * mm, "end": v(-18.74, -73.6) * mm});
            skLineSegment(sketch, "E1519", {"start": v(-18.74, -73.6) * mm, "end": v(-18.3, -73.41) * mm});
            skLineSegment(sketch, "E1520", {"start": v(-18.3, -73.41) * mm, "end": v(-17.9, -73.23) * mm});
            skLineSegment(sketch, "E1521", {"start": v(-17.9, -73.23) * mm, "end": v(-17.5, -73.04) * mm});
            skLineSegment(sketch, "E1522", {"start": v(-17.5, -73.04) * mm, "end": v(-17.12, -72.85) * mm});
            skLineSegment(sketch, "E1523", {"start": v(-17.12, -72.85) * mm, "end": v(-16.77, -72.66) * mm});
            skLineSegment(sketch, "E1524", {"start": v(-16.77, -72.66) * mm, "end": v(-16.43, -72.48) * mm});
            skLineSegment(sketch, "E1525", {"start": v(-16.43, -72.48) * mm, "end": v(-16.12, -72.3) * mm});
            skLineSegment(sketch, "E1526", {"start": v(-16.12, -72.3) * mm, "end": v(-15.82, -72.12) * mm});
            skLineSegment(sketch, "E1527", {"start": v(-15.82, -72.12) * mm, "end": v(-15.55, -71.95) * mm});
            skLineSegment(sketch, "E1528", {"start": v(-15.55, -71.95) * mm, "end": v(-15.3, -71.78) * mm});
            skLineSegment(sketch, "E1529", {"start": v(-15.3, -71.78) * mm, "end": v(-15.06, -71.62) * mm});
            skLineSegment(sketch, "E1530", {"start": v(-15.06, -71.62) * mm, "end": v(-14.84, -71.46) * mm});
            skLineSegment(sketch, "E1531", {"start": v(-14.84, -71.46) * mm, "end": v(-14.63, -71.31) * mm});
            skLineSegment(sketch, "E1532", {"start": v(-14.63, -71.31) * mm, "end": v(-14.45, -71.17) * mm});
            skLineSegment(sketch, "E1533", {"start": v(-14.45, -71.17) * mm, "end": v(-14.29, -71.04) * mm});
            skLineSegment(sketch, "E1534", {"start": v(-14.29, -71.04) * mm, "end": v(-14.14, -70.91) * mm});
            skLineSegment(sketch, "E1535", {"start": v(-14.14, -70.91) * mm, "end": v(-14, -70.8) * mm});
            skLineSegment(sketch, "E1536", {"start": v(-14, -70.8) * mm, "end": v(-13.89, -70.7) * mm});
            skLineSegment(sketch, "E1537", {"start": v(-13.89, -70.7) * mm, "end": v(-13.79, -70.6) * mm});
            skLineSegment(sketch, "E1538", {"start": v(-13.79, -70.6) * mm, "end": v(-13.7, -70.51) * mm});
            skLineSegment(sketch, "E1539", {"start": v(-13.7, -70.51) * mm, "end": v(-13.63, -70.44) * mm});
            skLineSegment(sketch, "E1540", {"start": v(-13.63, -70.44) * mm, "end": v(-13.57, -70.38) * mm});
            skLineSegment(sketch, "E1541", {"start": v(-13.57, -70.38) * mm, "end": v(-13.53, -70.33) * mm});
            skLineSegment(sketch, "E1542", {"start": v(-13.53, -70.33) * mm, "end": v(-13.5, -70.3) * mm});
            skLineSegment(sketch, "E1543", {"start": v(-13.5, -70.3) * mm, "end": v(-13.48, -70.28) * mm});
            skLineSegment(sketch, "E1544", {"start": v(-13.48, -70.28) * mm, "end": v(-11.26, -67.48) * mm});
            skLineSegment(sketch, "E1545", {"start": v(-11.26, -67.48) * mm, "end": v(-5.6, -71.33) * mm});
            skLineSegment(sketch, "E1546", {"start": v(-5.6, -71.33) * mm, "end": v(-7.38, -74.43) * mm});
            skLineSegment(sketch, "E1547", {"start": v(-7.38, -74.43) * mm, "end": v(-7.4, -74.46) * mm});
            skLineSegment(sketch, "E1548", {"start": v(-7.4, -74.46) * mm, "end": v(-7.42, -74.5) * mm});
            skLineSegment(sketch, "E1549", {"start": v(-7.42, -74.5) * mm, "end": v(-7.45, -74.55) * mm});
            skLineSegment(sketch, "E1550", {"start": v(-7.45, -74.55) * mm, "end": v(-7.48, -74.63) * mm});
            skLineSegment(sketch, "E1551", {"start": v(-7.48, -74.63) * mm, "end": v(-7.52, -74.72) * mm});
            skLineSegment(sketch, "E1552", {"start": v(-7.52, -74.72) * mm, "end": v(-7.57, -74.83) * mm});
            skLineSegment(sketch, "E1553", {"start": v(-7.57, -74.83) * mm, "end": v(-7.62, -74.96) * mm});
            skLineSegment(sketch, "E1554", {"start": v(-7.62, -74.96) * mm, "end": v(-7.68, -75.1) * mm});
            skLineSegment(sketch, "E1555", {"start": v(-7.68, -75.1) * mm, "end": v(-7.73, -75.27) * mm});
            skLineSegment(sketch, "E1556", {"start": v(-7.73, -75.27) * mm, "end": v(-7.8, -75.46) * mm});
            skLineSegment(sketch, "E1557", {"start": v(-7.8, -75.46) * mm, "end": v(-7.86, -75.66) * mm});
            skLineSegment(sketch, "E1558", {"start": v(-7.86, -75.66) * mm, "end": v(-7.92, -75.88) * mm});
            skLineSegment(sketch, "E1559", {"start": v(-7.92, -75.88) * mm, "end": v(-7.99, -76.12) * mm});
            skLineSegment(sketch, "E1560", {"start": v(-7.99, -76.12) * mm, "end": v(-8.05, -76.39) * mm});
            skLineSegment(sketch, "E1561", {"start": v(-8.05, -76.39) * mm, "end": v(-8.12, -76.67) * mm});
            skLineSegment(sketch, "E1562", {"start": v(-8.12, -76.67) * mm, "end": v(-8.18, -76.97) * mm});
            skLineSegment(sketch, "E1563", {"start": v(-8.18, -76.97) * mm, "end": v(-8.24, -77.29) * mm});
            skLineSegment(sketch, "E1564", {"start": v(-8.24, -77.29) * mm, "end": v(-8.3, -77.63) * mm});
            skLineSegment(sketch, "E1565", {"start": v(-8.3, -77.63) * mm, "end": v(-8.35, -77.98) * mm});
            skLineSegment(sketch, "E1566", {"start": v(-8.35, -77.98) * mm, "end": v(-8.4, -78.36) * mm});
            skLineSegment(sketch, "E1567", {"start": v(-8.4, -78.36) * mm, "end": v(-8.44, -78.76) * mm});
            skLineSegment(sketch, "E1568", {"start": v(-8.44, -78.76) * mm, "end": v(-8.48, -79.18) * mm});
            skLineSegment(sketch, "E1569", {"start": v(-8.48, -79.18) * mm, "end": v(-8.51, -79.61) * mm});
            skLineSegment(sketch, "E1570", {"start": v(-8.51, -79.61) * mm, "end": v(-8.53, -80.07) * mm});
            skLineSegment(sketch, "E1571", {"start": v(-8.53, -80.07) * mm, "end": v(-8.55, -80.54) * mm});
            skLineSegment(sketch, "E1572", {"start": v(-8.55, -80.54) * mm, "end": v(-8.55, -81.04) * mm});
            skLineSegment(sketch, "E1573", {"start": v(-8.55, -81.04) * mm, "end": v(-8.55, -81.55) * mm});
            skLineSegment(sketch, "E1574", {"start": v(-8.55, -81.55) * mm, "end": v(-8.54, -82.08) * mm});
            skLineSegment(sketch, "E1575", {"start": v(-8.54, -82.08) * mm, "end": v(-8.51, -82.63) * mm});
            skLineSegment(sketch, "E1576", {"start": v(-8.51, -82.63) * mm, "end": v(-8.47, -83.2) * mm});
            skLineSegment(sketch, "E1577", {"start": v(-8.47, -83.2) * mm, "end": v(-8.42, -83.78) * mm});
            skLineSegment(sketch, "E1578", {"start": v(-8.42, -83.78) * mm, "end": v(-8.28, -84.22) * mm});
            skLineSegment(sketch, "E1579", {"start": v(-8.28, -84.22) * mm, "end": v(-5.04, -85.67) * mm});
            skLineSegment(sketch, "E1580", {"start": v(-5.04, -85.67) * mm, "end": v(-4.62, -85.5) * mm});
            skLineSegment(sketch, "E1581", {"start": v(-4.62, -85.5) * mm, "end": v(-4.15, -85.15) * mm});
            skLineSegment(sketch, "E1582", {"start": v(-4.15, -85.15) * mm, "end": v(-3.7, -84.8) * mm});
            skLineSegment(sketch, "E1583", {"start": v(-3.7, -84.8) * mm, "end": v(-3.27, -84.45) * mm});
            skLineSegment(sketch, "E1584", {"start": v(-3.27, -84.45) * mm, "end": v(-2.87, -84.11) * mm});
            skLineSegment(sketch, "E1585", {"start": v(-2.87, -84.11) * mm, "end": v(-2.48, -83.78) * mm});
            skLineSegment(sketch, "E1586", {"start": v(-2.48, -83.78) * mm, "end": v(-2.11, -83.44) * mm});
            skLineSegment(sketch, "E1587", {"start": v(-2.11, -83.44) * mm, "end": v(-1.77, -83.12) * mm});
            skLineSegment(sketch, "E1588", {"start": v(-1.77, -83.12) * mm, "end": v(-1.44, -82.8) * mm});
            skLineSegment(sketch, "E1589", {"start": v(-1.44, -82.8) * mm, "end": v(-1.13, -82.49) * mm});
            skLineSegment(sketch, "E1590", {"start": v(-1.13, -82.49) * mm, "end": v(-0.85, -82.18) * mm});
            skLineSegment(sketch, "E1591", {"start": v(-0.85, -82.18) * mm, "end": v(-0.58, -81.89) * mm});
            skLineSegment(sketch, "E1592", {"start": v(-0.58, -81.89) * mm, "end": v(-0.33, -81.6) * mm});
            skLineSegment(sketch, "E1593", {"start": v(-0.33, -81.6) * mm, "end": v(-0.1, -81.32) * mm});
            skLineSegment(sketch, "E1594", {"start": v(-0.1, -81.32) * mm, "end": v(0.12, -81.05) * mm});
            skLineSegment(sketch, "E1595", {"start": v(0.12, -81.05) * mm, "end": v(0.32, -80.8) * mm});
            skLineSegment(sketch, "E1596", {"start": v(0.32, -80.8) * mm, "end": v(0.5, -80.55) * mm});
            skLineSegment(sketch, "E1597", {"start": v(0.5, -80.55) * mm, "end": v(0.67, -80.32) * mm});
            skLineSegment(sketch, "E1598", {"start": v(0.67, -80.32) * mm, "end": v(0.83, -80.1) * mm});
            skLineSegment(sketch, "E1599", {"start": v(0.83, -80.1) * mm, "end": v(0.97, -79.89) * mm});
            skLineSegment(sketch, "E1600", {"start": v(0.97, -79.89) * mm, "end": v(1.09, -79.7) * mm});
            skLineSegment(sketch, "E1601", {"start": v(1.09, -79.7) * mm, "end": v(1.2, -79.5) * mm});
            skLineSegment(sketch, "E1602", {"start": v(1.2, -79.5) * mm, "end": v(1.3, -79.34) * mm});
            skLineSegment(sketch, "E1603", {"start": v(1.3, -79.34) * mm, "end": v(1.38, -79.19) * mm});
            skLineSegment(sketch, "E1604", {"start": v(1.38, -79.19) * mm, "end": v(1.46, -79.05) * mm});
            skLineSegment(sketch, "E1605", {"start": v(1.46, -79.05) * mm, "end": v(1.52, -78.92) * mm});
            skLineSegment(sketch, "E1606", {"start": v(1.52, -78.92) * mm, "end": v(1.57, -78.82) * mm});
            skLineSegment(sketch, "E1607", {"start": v(1.57, -78.82) * mm, "end": v(1.61, -78.72) * mm});
            skLineSegment(sketch, "E1608", {"start": v(1.61, -78.72) * mm, "end": v(1.64, -78.65) * mm});
            skLineSegment(sketch, "E1609", {"start": v(1.64, -78.65) * mm, "end": v(1.67, -78.6) * mm});
            skLineSegment(sketch, "E1610", {"start": v(1.67, -78.6) * mm, "end": v(1.68, -78.55) * mm});
            skLineSegment(sketch, "E1611", {"start": v(1.68, -78.55) * mm, "end": v(1.7, -78.52) * mm});
            skLineSegment(sketch, "E1612", {"start": v(1.7, -78.52) * mm, "end": v(2.83, -75.13) * mm});
            skLineSegment(sketch, "E1613", {"start": v(2.83, -75.13) * mm, "end": v(9.47, -76.82) * mm});
            skLineSegment(sketch, "E1614", {"start": v(9.47, -76.82) * mm, "end": v(8.85, -80.34) * mm});
            skLineSegment(sketch, "E1615", {"start": v(8.85, -80.34) * mm, "end": v(8.84, -80.37) * mm});
            skLineSegment(sketch, "E1616", {"start": v(8.84, -80.37) * mm, "end": v(8.84, -80.41) * mm});
            skLineSegment(sketch, "E1617", {"start": v(8.84, -80.41) * mm, "end": v(8.83, -80.47) * mm});
            skLineSegment(sketch, "E1618", {"start": v(8.83, -80.47) * mm, "end": v(8.82, -80.56) * mm});
            skLineSegment(sketch, "E1619", {"start": v(8.82, -80.56) * mm, "end": v(8.81, -80.66) * mm});
            skLineSegment(sketch, "E1620", {"start": v(8.81, -80.66) * mm, "end": v(8.8, -80.78) * mm});
            skLineSegment(sketch, "E1621", {"start": v(8.8, -80.78) * mm, "end": v(8.8, -80.91) * mm});
            skLineSegment(sketch, "E1622", {"start": v(8.8, -80.91) * mm, "end": v(8.8, -81.07) * mm});
            skLineSegment(sketch, "E1623", {"start": v(8.8, -81.07) * mm, "end": v(8.8, -81.25) * mm});
            skLineSegment(sketch, "E1624", {"start": v(8.8, -81.25) * mm, "end": v(8.8, -81.44) * mm});
            skLineSegment(sketch, "E1625", {"start": v(8.8, -81.44) * mm, "end": v(8.82, -81.65) * mm});
            skLineSegment(sketch, "E1626", {"start": v(8.82, -81.65) * mm, "end": v(8.83, -81.89) * mm});
            skLineSegment(sketch, "E1627", {"start": v(8.83, -81.89) * mm, "end": v(8.86, -82.14) * mm});
            skLineSegment(sketch, "E1628", {"start": v(8.86, -82.14) * mm, "end": v(8.88, -82.4) * mm});
            skLineSegment(sketch, "E1629", {"start": v(8.88, -82.4) * mm, "end": v(8.92, -82.69) * mm});
            skLineSegment(sketch, "E1630", {"start": v(8.92, -82.69) * mm, "end": v(8.96, -83) * mm});
            skLineSegment(sketch, "E1631", {"start": v(8.96, -83) * mm, "end": v(9.02, -83.31) * mm});
            skLineSegment(sketch, "E1632", {"start": v(9.02, -83.31) * mm, "end": v(9.08, -83.65) * mm});
            skLineSegment(sketch, "E1633", {"start": v(9.08, -83.65) * mm, "end": v(9.15, -84) * mm});
            skLineSegment(sketch, "E1634", {"start": v(9.15, -84) * mm, "end": v(9.24, -84.38) * mm});
            skLineSegment(sketch, "E1635", {"start": v(9.24, -84.38) * mm, "end": v(9.33, -84.77) * mm});
            skLineSegment(sketch, "E1636", {"start": v(9.33, -84.77) * mm, "end": v(9.44, -85.17) * mm});
            skLineSegment(sketch, "E1637", {"start": v(9.44, -85.17) * mm, "end": v(9.56, -85.6) * mm});
            skLineSegment(sketch, "E1638", {"start": v(9.56, -85.6) * mm, "end": v(9.7, -86.03) * mm});
            skLineSegment(sketch, "E1639", {"start": v(9.7, -86.03) * mm, "end": v(9.84, -86.48) * mm});
            skLineSegment(sketch, "E1640", {"start": v(9.84, -86.48) * mm, "end": v(10, -86.95) * mm});
            skLineSegment(sketch, "E1641", {"start": v(10, -86.95) * mm, "end": v(10.18, -87.43) * mm});
            skLineSegment(sketch, "E1642", {"start": v(10.18, -87.43) * mm, "end": v(10.38, -87.92) * mm});
            skLineSegment(sketch, "E1643", {"start": v(10.38, -87.92) * mm, "end": v(10.6, -88.43) * mm});
            skLineSegment(sketch, "E1644", {"start": v(10.6, -88.43) * mm, "end": v(10.82, -88.95) * mm});
            skLineSegment(sketch, "E1645", {"start": v(10.82, -88.95) * mm, "end": v(11.07, -89.48) * mm});
            skLineSegment(sketch, "E1646", {"start": v(11.07, -89.48) * mm, "end": v(11.35, -89.84) * mm});
            skLineSegment(sketch, "E1647", {"start": v(11.35, -89.84) * mm, "end": v(14.9, -90.1) * mm});
            skLineSegment(sketch, "E1648", {"start": v(14.9, -90.1) * mm, "end": v(15.23, -89.8) * mm});
            skLineSegment(sketch, "E1649", {"start": v(15.23, -89.8) * mm, "end": v(15.55, -89.3) * mm});
            skLineSegment(sketch, "E1650", {"start": v(15.55, -89.3) * mm, "end": v(15.85, -88.82) * mm});
            skLineSegment(sketch, "E1651", {"start": v(15.85, -88.82) * mm, "end": v(16.14, -88.35) * mm});
            skLineSegment(sketch, "E1652", {"start": v(16.14, -88.35) * mm, "end": v(16.4, -87.89) * mm});
            skLineSegment(sketch, "E1653", {"start": v(16.4, -87.89) * mm, "end": v(16.65, -87.44) * mm});
            skLineSegment(sketch, "E1654", {"start": v(16.65, -87.44) * mm, "end": v(16.88, -87) * mm});
            skLineSegment(sketch, "E1655", {"start": v(16.88, -87) * mm, "end": v(17.1, -86.58) * mm});
            skLineSegment(sketch, "E1656", {"start": v(17.1, -86.58) * mm, "end": v(17.3, -86.17) * mm});
            skLineSegment(sketch, "E1657", {"start": v(17.3, -86.17) * mm, "end": v(17.47, -85.77) * mm});
            skLineSegment(sketch, "E1658", {"start": v(17.47, -85.77) * mm, "end": v(17.64, -85.39) * mm});
            skLineSegment(sketch, "E1659", {"start": v(17.64, -85.39) * mm, "end": v(17.8, -85.02) * mm});
            skLineSegment(sketch, "E1660", {"start": v(17.8, -85.02) * mm, "end": v(17.93, -84.66) * mm});
            skLineSegment(sketch, "E1661", {"start": v(17.93, -84.66) * mm, "end": v(18.05, -84.32) * mm});
            skLineSegment(sketch, "E1662", {"start": v(18.05, -84.32) * mm, "end": v(18.17, -84) * mm});
            skLineSegment(sketch, "E1663", {"start": v(18.17, -84) * mm, "end": v(18.27, -83.69) * mm});
            skLineSegment(sketch, "E1664", {"start": v(18.27, -83.69) * mm, "end": v(18.35, -83.4) * mm});
            skLineSegment(sketch, "E1665", {"start": v(18.35, -83.4) * mm, "end": v(18.43, -83.11) * mm});
            skLineSegment(sketch, "E1666", {"start": v(18.43, -83.11) * mm, "end": v(18.5, -82.85) * mm});
            skLineSegment(sketch, "E1667", {"start": v(18.5, -82.85) * mm, "end": v(18.56, -82.6) * mm});
            skLineSegment(sketch, "E1668", {"start": v(18.56, -82.6) * mm, "end": v(18.6, -82.38) * mm});
            skLineSegment(sketch, "E1669", {"start": v(18.6, -82.38) * mm, "end": v(18.65, -82.17) * mm});
            skLineSegment(sketch, "E1670", {"start": v(18.65, -82.17) * mm, "end": v(18.68, -81.98) * mm});
            skLineSegment(sketch, "E1671", {"start": v(18.68, -81.98) * mm, "end": v(18.7, -81.8) * mm});
            skLineSegment(sketch, "E1672", {"start": v(18.7, -81.8) * mm, "end": v(18.73, -81.65) * mm});
            skLineSegment(sketch, "E1673", {"start": v(18.73, -81.65) * mm, "end": v(18.75, -81.52) * mm});
            skLineSegment(sketch, "E1674", {"start": v(18.75, -81.52) * mm, "end": v(18.76, -81.4) * mm});
            skLineSegment(sketch, "E1675", {"start": v(18.76, -81.4) * mm, "end": v(18.77, -81.3) * mm});
            skLineSegment(sketch, "E1676", {"start": v(18.77, -81.3) * mm, "end": v(18.77, -81.21) * mm});
            skLineSegment(sketch, "E1677", {"start": v(18.77, -81.21) * mm, "end": v(18.77, -81.15) * mm});
            skLineSegment(sketch, "E1678", {"start": v(18.77, -81.15) * mm, "end": v(18.78, -81.1) * mm});
            skLineSegment(sketch, "E1679", {"start": v(18.78, -81.1) * mm, "end": v(18.78, -81.08) * mm});
            skLineSegment(sketch, "E1680", {"start": v(18.78, -81.08) * mm, "end": v(18.68, -77.5) * mm});
            skLineSegment(sketch, "E1681", {"start": v(18.68, -77.5) * mm, "end": v(25.5, -76.82) * mm});
            skLineSegment(sketch, "E1682", {"start": v(25.5, -76.82) * mm, "end": v(26.12, -80.34) * mm});
            skLineSegment(sketch, "E1683", {"start": v(26.12, -80.34) * mm, "end": v(26.12, -80.37) * mm});
            skLineSegment(sketch, "E1684", {"start": v(26.12, -80.37) * mm, "end": v(26.13, -80.4) * mm});
            skLineSegment(sketch, "E1685", {"start": v(26.13, -80.4) * mm, "end": v(26.15, -80.47) * mm});
            skLineSegment(sketch, "E1686", {"start": v(26.15, -80.47) * mm, "end": v(26.17, -80.55) * mm});
            skLineSegment(sketch, "E1687", {"start": v(26.17, -80.55) * mm, "end": v(26.2, -80.65) * mm});
            skLineSegment(sketch, "E1688", {"start": v(26.2, -80.65) * mm, "end": v(26.23, -80.76) * mm});
            skLineSegment(sketch, "E1689", {"start": v(26.23, -80.76) * mm, "end": v(26.28, -80.9) * mm});
            skLineSegment(sketch, "E1690", {"start": v(26.28, -80.9) * mm, "end": v(26.33, -81.04) * mm});
            skLineSegment(sketch, "E1691", {"start": v(26.33, -81.04) * mm, "end": v(26.39, -81.2) * mm});
            skLineSegment(sketch, "E1692", {"start": v(26.39, -81.2) * mm, "end": v(26.46, -81.39) * mm});
            skLineSegment(sketch, "E1693", {"start": v(26.46, -81.39) * mm, "end": v(26.54, -81.58) * mm});
            skLineSegment(sketch, "E1694", {"start": v(26.54, -81.58) * mm, "end": v(26.64, -81.8) * mm});
            skLineSegment(sketch, "E1695", {"start": v(26.64, -81.8) * mm, "end": v(26.74, -82.02) * mm});
            skLineSegment(sketch, "E1696", {"start": v(26.74, -82.02) * mm, "end": v(26.86, -82.27) * mm});
            skLineSegment(sketch, "E1697", {"start": v(26.86, -82.27) * mm, "end": v(27, -82.52) * mm});
            skLineSegment(sketch, "E1698", {"start": v(27, -82.52) * mm, "end": v(27.14, -82.8) * mm});
            skLineSegment(sketch, "E1699", {"start": v(27.14, -82.8) * mm, "end": v(27.3, -83.08) * mm});
            skLineSegment(sketch, "E1700", {"start": v(27.3, -83.08) * mm, "end": v(27.47, -83.37) * mm});
            skLineSegment(sketch, "E1701", {"start": v(27.47, -83.37) * mm, "end": v(27.66, -83.68) * mm});
            skLineSegment(sketch, "E1702", {"start": v(27.66, -83.68) * mm, "end": v(27.87, -84) * mm});
            skLineSegment(sketch, "E1703", {"start": v(27.87, -84) * mm, "end": v(28.09, -84.34) * mm});
            skLineSegment(sketch, "E1704", {"start": v(28.09, -84.34) * mm, "end": v(28.33, -84.68) * mm});
            skLineSegment(sketch, "E1705", {"start": v(28.33, -84.68) * mm, "end": v(28.59, -85.03) * mm});
            skLineSegment(sketch, "E1706", {"start": v(28.59, -85.03) * mm, "end": v(28.86, -85.4) * mm});
            skLineSegment(sketch, "E1707", {"start": v(28.86, -85.4) * mm, "end": v(29.15, -85.77) * mm});
            skLineSegment(sketch, "E1708", {"start": v(29.15, -85.77) * mm, "end": v(29.47, -86.15) * mm});
            skLineSegment(sketch, "E1709", {"start": v(29.47, -86.15) * mm, "end": v(29.8, -86.54) * mm});
            skLineSegment(sketch, "E1710", {"start": v(29.8, -86.54) * mm, "end": v(30.15, -86.94) * mm});
            skLineSegment(sketch, "E1711", {"start": v(30.15, -86.94) * mm, "end": v(30.52, -87.34) * mm});
            skLineSegment(sketch, "E1712", {"start": v(30.52, -87.34) * mm, "end": v(30.92, -87.75) * mm});
            skLineSegment(sketch, "E1713", {"start": v(30.92, -87.75) * mm, "end": v(31.33, -88.17) * mm});
            skLineSegment(sketch, "E1714", {"start": v(31.33, -88.17) * mm, "end": v(31.72, -88.4) * mm});
            skLineSegment(sketch, "E1715", {"start": v(31.72, -88.4) * mm, "end": v(35.14, -87.45) * mm});
            skLineSegment(sketch, "E1716", {"start": v(35.14, -87.45) * mm, "end": v(35.34, -87.04) * mm});
            skLineSegment(sketch, "E1717", {"start": v(35.34, -87.04) * mm, "end": v(35.48, -86.47) * mm});
            skLineSegment(sketch, "E1718", {"start": v(35.48, -86.47) * mm, "end": v(35.6, -85.91) * mm});
            skLineSegment(sketch, "E1719", {"start": v(35.6, -85.91) * mm, "end": v(35.7, -85.37) * mm});
            skLineSegment(sketch, "E1720", {"start": v(35.7, -85.37) * mm, "end": v(35.8, -84.85) * mm});
            skLineSegment(sketch, "E1721", {"start": v(35.8, -84.85) * mm, "end": v(35.88, -84.34) * mm});
            skLineSegment(sketch, "E1722", {"start": v(35.88, -84.34) * mm, "end": v(35.95, -83.85) * mm});
            skLineSegment(sketch, "E1723", {"start": v(35.95, -83.85) * mm, "end": v(36, -83.38) * mm});
            skLineSegment(sketch, "E1724", {"start": v(36, -83.38) * mm, "end": v(36.05, -82.93) * mm});
            skLineSegment(sketch, "E1725", {"start": v(36.05, -82.93) * mm, "end": v(36.08, -82.5) * mm});
            skLineSegment(sketch, "E1726", {"start": v(36.08, -82.5) * mm, "end": v(36.1, -82.07) * mm});
            skLineSegment(sketch, "E1727", {"start": v(36.1, -82.07) * mm, "end": v(36.12, -81.67) * mm});
            skLineSegment(sketch, "E1728", {"start": v(36.12, -81.67) * mm, "end": v(36.13, -81.3) * mm});
            skLineSegment(sketch, "E1729", {"start": v(36.13, -81.3) * mm, "end": v(36.13, -80.93) * mm});
            skLineSegment(sketch, "E1730", {"start": v(36.13, -80.93) * mm, "end": v(36.13, -80.59) * mm});
            skLineSegment(sketch, "E1731", {"start": v(36.13, -80.59) * mm, "end": v(36.11, -80.26) * mm});
            skLineSegment(sketch, "E1732", {"start": v(36.11, -80.26) * mm, "end": v(36.1, -79.96) * mm});
            skLineSegment(sketch, "E1733", {"start": v(36.1, -79.96) * mm, "end": v(36.07, -79.67) * mm});
            skLineSegment(sketch, "E1734", {"start": v(36.07, -79.67) * mm, "end": v(36.05, -79.4) * mm});
            skLineSegment(sketch, "E1735", {"start": v(36.05, -79.4) * mm, "end": v(36.02, -79.15) * mm});
            skLineSegment(sketch, "E1736", {"start": v(36.02, -79.15) * mm, "end": v(35.99, -78.92) * mm});
            skLineSegment(sketch, "E1737", {"start": v(35.99, -78.92) * mm, "end": v(35.96, -78.71) * mm});
            skLineSegment(sketch, "E1738", {"start": v(35.96, -78.71) * mm, "end": v(35.92, -78.52) * mm});
            skLineSegment(sketch, "E1739", {"start": v(35.92, -78.52) * mm, "end": v(35.89, -78.35) * mm});
            skLineSegment(sketch, "E1740", {"start": v(35.89, -78.35) * mm, "end": v(35.86, -78.2) * mm});
            skLineSegment(sketch, "E1741", {"start": v(35.86, -78.2) * mm, "end": v(35.82, -78.06) * mm});
            skLineSegment(sketch, "E1742", {"start": v(35.82, -78.06) * mm, "end": v(35.8, -77.94) * mm});
            skLineSegment(sketch, "E1743", {"start": v(35.8, -77.94) * mm, "end": v(35.77, -77.84) * mm});
            skLineSegment(sketch, "E1744", {"start": v(35.77, -77.84) * mm, "end": v(35.74, -77.77) * mm});
            skLineSegment(sketch, "E1745", {"start": v(35.74, -77.77) * mm, "end": v(35.72, -77.7) * mm});
            skLineSegment(sketch, "E1746", {"start": v(35.72, -77.7) * mm, "end": v(35.71, -77.66) * mm});
            skLineSegment(sketch, "E1747", {"start": v(35.71, -77.66) * mm, "end": v(35.7, -77.64) * mm});
            skLineSegment(sketch, "E1748", {"start": v(35.7, -77.64) * mm, "end": v(34.4, -74.3) * mm});
            skLineSegment(sketch, "E1749", {"start": v(34.4, -74.3) * mm, "end": v(40.56, -71.33) * mm});
            skLineSegment(sketch, "E1750", {"start": v(40.56, -71.33) * mm, "end": v(42.35, -74.43) * mm});
            skLineSegment(sketch, "E1751", {"start": v(42.35, -74.43) * mm, "end": v(42.36, -74.46) * mm});
            skLineSegment(sketch, "E1752", {"start": v(42.36, -74.46) * mm, "end": v(42.39, -74.5) * mm});
            skLineSegment(sketch, "E1753", {"start": v(42.39, -74.5) * mm, "end": v(42.42, -74.55) * mm});
            skLineSegment(sketch, "E1754", {"start": v(42.42, -74.55) * mm, "end": v(42.47, -74.61) * mm});
            skLineSegment(sketch, "E1755", {"start": v(42.47, -74.61) * mm, "end": v(42.53, -74.7) * mm});
            skLineSegment(sketch, "E1756", {"start": v(42.53, -74.7) * mm, "end": v(42.6, -74.8) * mm});
            skLineSegment(sketch, "E1757", {"start": v(42.6, -74.8) * mm, "end": v(42.69, -74.9) * mm});
            skLineSegment(sketch, "E1758", {"start": v(42.69, -74.9) * mm, "end": v(42.79, -75.02) * mm});
            skLineSegment(sketch, "E1759", {"start": v(42.79, -75.02) * mm, "end": v(42.9, -75.15) * mm});
            skLineSegment(sketch, "E1760", {"start": v(42.9, -75.15) * mm, "end": v(43.03, -75.3) * mm});
            skLineSegment(sketch, "E1761", {"start": v(43.03, -75.3) * mm, "end": v(43.17, -75.46) * mm});
            skLineSegment(sketch, "E1762", {"start": v(43.17, -75.46) * mm, "end": v(43.33, -75.62) * mm});
            skLineSegment(sketch, "E1763", {"start": v(43.33, -75.62) * mm, "end": v(43.51, -75.8) * mm});
            skLineSegment(sketch, "E1764", {"start": v(43.51, -75.8) * mm, "end": v(43.7, -75.99) * mm});
            skLineSegment(sketch, "E1765", {"start": v(43.7, -75.99) * mm, "end": v(43.92, -76.18) * mm});
            skLineSegment(sketch, "E1766", {"start": v(43.92, -76.18) * mm, "end": v(44.14, -76.39) * mm});
            skLineSegment(sketch, "E1767", {"start": v(44.14, -76.39) * mm, "end": v(44.4, -76.6) * mm});
            skLineSegment(sketch, "E1768", {"start": v(44.4, -76.6) * mm, "end": v(44.66, -76.82) * mm});
            skLineSegment(sketch, "E1769", {"start": v(44.66, -76.82) * mm, "end": v(44.94, -77.05) * mm});
            skLineSegment(sketch, "E1770", {"start": v(44.94, -77.05) * mm, "end": v(45.24, -77.28) * mm});
            skLineSegment(sketch, "E1771", {"start": v(45.24, -77.28) * mm, "end": v(45.57, -77.51) * mm});
            skLineSegment(sketch, "E1772", {"start": v(45.57, -77.51) * mm, "end": v(45.9, -77.75) * mm});
            skLineSegment(sketch, "E1773", {"start": v(45.9, -77.75) * mm, "end": v(46.27, -78) * mm});
            skLineSegment(sketch, "E1774", {"start": v(46.27, -78) * mm, "end": v(46.65, -78.25) * mm});
            skLineSegment(sketch, "E1775", {"start": v(46.65, -78.25) * mm, "end": v(47.06, -78.5) * mm});
            skLineSegment(sketch, "E1776", {"start": v(47.06, -78.5) * mm, "end": v(47.48, -78.75) * mm});
            skLineSegment(sketch, "E1777", {"start": v(47.48, -78.75) * mm, "end": v(47.93, -79) * mm});
            skLineSegment(sketch, "E1778", {"start": v(47.93, -79) * mm, "end": v(48.4, -79.25) * mm});
            skLineSegment(sketch, "E1779", {"start": v(48.4, -79.25) * mm, "end": v(48.88, -79.5) * mm});
            skLineSegment(sketch, "E1780", {"start": v(48.88, -79.5) * mm, "end": v(49.4, -79.76) * mm});
            skLineSegment(sketch, "E1781", {"start": v(49.4, -79.76) * mm, "end": v(49.93, -80) * mm});
            skLineSegment(sketch, "E1782", {"start": v(49.93, -80) * mm, "end": v(50.37, -80.1) * mm});
            skLineSegment(sketch, "E1783", {"start": v(50.37, -80.1) * mm, "end": v(53.25, -78.03) * mm});
            skLineSegment(sketch, "E1784", {"start": v(53.25, -78.03) * mm, "end": v(53.3, -77.57) * mm});
            skLineSegment(sketch, "E1785", {"start": v(53.3, -77.57) * mm, "end": v(53.24, -76.99) * mm});
            skLineSegment(sketch, "E1786", {"start": v(53.24, -76.99) * mm, "end": v(53.17, -76.42) * mm});
            skLineSegment(sketch, "E1787", {"start": v(53.17, -76.42) * mm, "end": v(53.08, -75.88) * mm});
            skLineSegment(sketch, "E1788", {"start": v(53.08, -75.88) * mm, "end": v(53, -75.36) * mm});
            skLineSegment(sketch, "E1789", {"start": v(53, -75.36) * mm, "end": v(52.9, -74.86) * mm});
            skLineSegment(sketch, "E1790", {"start": v(52.9, -74.86) * mm, "end": v(52.79, -74.37) * mm});
            skLineSegment(sketch, "E1791", {"start": v(52.79, -74.37) * mm, "end": v(52.68, -73.91) * mm});
            skLineSegment(sketch, "E1792", {"start": v(52.68, -73.91) * mm, "end": v(52.57, -73.47) * mm});
            skLineSegment(sketch, "E1793", {"start": v(52.57, -73.47) * mm, "end": v(52.45, -73.05) * mm});
            skLineSegment(sketch, "E1794", {"start": v(52.45, -73.05) * mm, "end": v(52.33, -72.65) * mm});
            skLineSegment(sketch, "E1795", {"start": v(52.33, -72.65) * mm, "end": v(52.2, -72.26) * mm});
            skLineSegment(sketch, "E1796", {"start": v(52.2, -72.26) * mm, "end": v(52.08, -71.9) * mm});
            skLineSegment(sketch, "E1797", {"start": v(52.08, -71.9) * mm, "end": v(51.96, -71.56) * mm});
            skLineSegment(sketch, "E1798", {"start": v(51.96, -71.56) * mm, "end": v(51.84, -71.24) * mm});
            skLineSegment(sketch, "E1799", {"start": v(51.84, -71.24) * mm, "end": v(51.71, -70.94) * mm});
            skLineSegment(sketch, "E1800", {"start": v(51.71, -70.94) * mm, "end": v(51.6, -70.66) * mm});
            skLineSegment(sketch, "E1801", {"start": v(51.6, -70.66) * mm, "end": v(51.47, -70.4) * mm});
            skLineSegment(sketch, "E1802", {"start": v(51.47, -70.4) * mm, "end": v(51.36, -70.15) * mm});
            skLineSegment(sketch, "E1803", {"start": v(51.36, -70.15) * mm, "end": v(51.25, -69.93) * mm});
            skLineSegment(sketch, "E1804", {"start": v(51.25, -69.93) * mm, "end": v(51.14, -69.72) * mm});
            skLineSegment(sketch, "E1805", {"start": v(51.14, -69.72) * mm, "end": v(51.04, -69.54) * mm});
            skLineSegment(sketch, "E1806", {"start": v(51.04, -69.54) * mm, "end": v(50.94, -69.37) * mm});
            skLineSegment(sketch, "E1807", {"start": v(50.94, -69.37) * mm, "end": v(50.85, -69.22) * mm});
            skLineSegment(sketch, "E1808", {"start": v(50.85, -69.22) * mm, "end": v(50.76, -69.08) * mm});
            skLineSegment(sketch, "E1809", {"start": v(50.76, -69.08) * mm, "end": v(50.69, -68.97) * mm});
            skLineSegment(sketch, "E1810", {"start": v(50.69, -68.97) * mm, "end": v(50.62, -68.87) * mm});
            skLineSegment(sketch, "E1811", {"start": v(50.62, -68.87) * mm, "end": v(50.56, -68.79) * mm});
            skLineSegment(sketch, "E1812", {"start": v(50.56, -68.79) * mm, "end": v(50.51, -68.72) * mm});
            skLineSegment(sketch, "E1813", {"start": v(50.51, -68.72) * mm, "end": v(50.47, -68.67) * mm});
            skLineSegment(sketch, "E1814", {"start": v(50.47, -68.67) * mm, "end": v(50.45, -68.64) * mm});
            skLineSegment(sketch, "E1815", {"start": v(50.45, -68.64) * mm, "end": v(50.43, -68.62) * mm});
            skLineSegment(sketch, "E1816", {"start": v(50.43, -68.62) * mm, "end": v(48.06, -65.94) * mm});
            skLineSegment(sketch, "E1817", {"start": v(48.06, -65.94) * mm, "end": v(52.84, -61.03) * mm});
            skLineSegment(sketch, "E1818", {"start": v(52.84, -61.03) * mm, "end": v(55.58, -63.33) * mm});
            skLineSegment(sketch, "E1819", {"start": v(55.58, -63.33) * mm, "end": v(55.6, -63.35) * mm});
            skLineSegment(sketch, "E1820", {"start": v(55.6, -63.35) * mm, "end": v(55.64, -63.37) * mm});
            skLineSegment(sketch, "E1821", {"start": v(55.64, -63.37) * mm, "end": v(55.69, -63.41) * mm});
            skLineSegment(sketch, "E1822", {"start": v(55.69, -63.41) * mm, "end": v(55.75, -63.46) * mm});
            skLineSegment(sketch, "E1823", {"start": v(55.75, -63.46) * mm, "end": v(55.84, -63.52) * mm});
            skLineSegment(sketch, "E1824", {"start": v(55.84, -63.52) * mm, "end": v(55.94, -63.58) * mm});
            skLineSegment(sketch, "E1825", {"start": v(55.94, -63.58) * mm, "end": v(56.06, -63.65) * mm});
            skLineSegment(sketch, "E1826", {"start": v(56.06, -63.65) * mm, "end": v(56.2, -63.73) * mm});
            skLineSegment(sketch, "E1827", {"start": v(56.2, -63.73) * mm, "end": v(56.34, -63.82) * mm});
            skLineSegment(sketch, "E1828", {"start": v(56.34, -63.82) * mm, "end": v(56.52, -63.91) * mm});
            skLineSegment(sketch, "E1829", {"start": v(56.52, -63.91) * mm, "end": v(56.7, -64.01) * mm});
            skLineSegment(sketch, "E1830", {"start": v(56.7, -64.01) * mm, "end": v(56.91, -64.11) * mm});
            skLineSegment(sketch, "E1831", {"start": v(56.91, -64.11) * mm, "end": v(57.14, -64.22) * mm});
            skLineSegment(sketch, "E1832", {"start": v(57.14, -64.22) * mm, "end": v(57.39, -64.33) * mm});
            skLineSegment(sketch, "E1833", {"start": v(57.39, -64.33) * mm, "end": v(57.65, -64.44) * mm});
            skLineSegment(sketch, "E1834", {"start": v(57.65, -64.44) * mm, "end": v(57.94, -64.55) * mm});
            skLineSegment(sketch, "E1835", {"start": v(57.94, -64.55) * mm, "end": v(58.24, -64.67) * mm});
            skLineSegment(sketch, "E1836", {"start": v(58.24, -64.67) * mm, "end": v(58.56, -64.78) * mm});
            skLineSegment(sketch, "E1837", {"start": v(58.56, -64.78) * mm, "end": v(58.9, -64.9) * mm});
            skLineSegment(sketch, "E1838", {"start": v(58.9, -64.9) * mm, "end": v(59.27, -65.01) * mm});
            skLineSegment(sketch, "E1839", {"start": v(59.27, -65.01) * mm, "end": v(59.66, -65.12) * mm});
            skLineSegment(sketch, "E1840", {"start": v(59.66, -65.12) * mm, "end": v(60.06, -65.23) * mm});
            skLineSegment(sketch, "E1841", {"start": v(60.06, -65.23) * mm, "end": v(60.49, -65.34) * mm});
            skLineSegment(sketch, "E1842", {"start": v(60.49, -65.34) * mm, "end": v(60.93, -65.44) * mm});
            skLineSegment(sketch, "E1843", {"start": v(60.93, -65.44) * mm, "end": v(61.4, -65.54) * mm});
            skLineSegment(sketch, "E1844", {"start": v(61.4, -65.54) * mm, "end": v(61.88, -65.63) * mm});
            skLineSegment(sketch, "E1845", {"start": v(61.88, -65.63) * mm, "end": v(62.39, -65.71) * mm});
            skLineSegment(sketch, "E1846", {"start": v(62.39, -65.71) * mm, "end": v(62.91, -65.8) * mm});
            skLineSegment(sketch, "E1847", {"start": v(62.91, -65.8) * mm, "end": v(63.46, -65.86) * mm});
            skLineSegment(sketch, "E1848", {"start": v(63.46, -65.86) * mm, "end": v(64.02, -65.92) * mm});
            skLineSegment(sketch, "E1849", {"start": v(64.02, -65.92) * mm, "end": v(64.6, -65.98) * mm});
            skLineSegment(sketch, "E1850", {"start": v(64.6, -65.98) * mm, "end": v(65.06, -65.9) * mm});
            skLineSegment(sketch, "E1851", {"start": v(65.06, -65.9) * mm, "end": v(67.06, -62.98) * mm});
            skLineSegment(sketch, "E1852", {"start": v(67.06, -62.98) * mm, "end": v(66.95, -62.53) * mm});
            skLineSegment(sketch, "E1853", {"start": v(66.95, -62.53) * mm, "end": v(66.7, -62) * mm});
            skLineSegment(sketch, "E1854", {"start": v(66.7, -62) * mm, "end": v(66.43, -61.5) * mm});
            skLineSegment(sketch, "E1855", {"start": v(66.43, -61.5) * mm, "end": v(66.16, -61.02) * mm});
            skLineSegment(sketch, "E1856", {"start": v(66.16, -61.02) * mm, "end": v(65.9, -60.56) * mm});
            skLineSegment(sketch, "E1857", {"start": v(65.9, -60.56) * mm, "end": v(65.63, -60.12) * mm});
            skLineSegment(sketch, "E1858", {"start": v(65.63, -60.12) * mm, "end": v(65.37, -59.7) * mm});
            skLineSegment(sketch, "E1859", {"start": v(65.37, -59.7) * mm, "end": v(65.1, -59.3) * mm});
            skLineSegment(sketch, "E1860", {"start": v(65.1, -59.3) * mm, "end": v(64.85, -58.93) * mm});
            skLineSegment(sketch, "E1861", {"start": v(64.85, -58.93) * mm, "end": v(64.6, -58.57) * mm});
            skLineSegment(sketch, "E1862", {"start": v(64.6, -58.57) * mm, "end": v(64.35, -58.24) * mm});
            skLineSegment(sketch, "E1863", {"start": v(64.35, -58.24) * mm, "end": v(64.1, -57.92) * mm});
            skLineSegment(sketch, "E1864", {"start": v(64.1, -57.92) * mm, "end": v(63.86, -57.62) * mm});
            skLineSegment(sketch, "E1865", {"start": v(63.86, -57.62) * mm, "end": v(63.63, -57.35) * mm});
            skLineSegment(sketch, "E1866", {"start": v(63.63, -57.35) * mm, "end": v(63.4, -57.09) * mm});
            skLineSegment(sketch, "E1867", {"start": v(63.4, -57.09) * mm, "end": v(63.19, -56.84) * mm});
            skLineSegment(sketch, "E1868", {"start": v(63.19, -56.84) * mm, "end": v(62.98, -56.62) * mm});
            skLineSegment(sketch, "E1869", {"start": v(62.98, -56.62) * mm, "end": v(62.77, -56.42) * mm});
            skLineSegment(sketch, "E1870", {"start": v(62.77, -56.42) * mm, "end": v(62.58, -56.23) * mm});
            skLineSegment(sketch, "E1871", {"start": v(62.58, -56.23) * mm, "end": v(62.4, -56.05) * mm});
            skLineSegment(sketch, "E1872", {"start": v(62.4, -56.05) * mm, "end": v(62.23, -55.9) * mm});
            skLineSegment(sketch, "E1873", {"start": v(62.23, -55.9) * mm, "end": v(62.07, -55.76) * mm});
            skLineSegment(sketch, "E1874", {"start": v(62.07, -55.76) * mm, "end": v(61.92, -55.63) * mm});
            skLineSegment(sketch, "E1875", {"start": v(61.92, -55.63) * mm, "end": v(61.78, -55.52) * mm});
            skLineSegment(sketch, "E1876", {"start": v(61.78, -55.52) * mm, "end": v(61.66, -55.43) * mm});
            skLineSegment(sketch, "E1877", {"start": v(61.66, -55.43) * mm, "end": v(61.55, -55.34) * mm});
            skLineSegment(sketch, "E1878", {"start": v(61.55, -55.34) * mm, "end": v(61.45, -55.27) * mm});
            skLineSegment(sketch, "E1879", {"start": v(61.45, -55.27) * mm, "end": v(61.37, -55.22) * mm});
            skLineSegment(sketch, "E1880", {"start": v(61.37, -55.22) * mm, "end": v(61.3, -55.17) * mm});
            skLineSegment(sketch, "E1881", {"start": v(61.3, -55.17) * mm, "end": v(61.25, -55.14) * mm});
            skLineSegment(sketch, "E1882", {"start": v(61.25, -55.14) * mm, "end": v(61.2, -55.11) * mm});
            skLineSegment(sketch, "E1883", {"start": v(61.2, -55.11) * mm, "end": v(61.18, -55.1) * mm});
            skLineSegment(sketch, "E1884", {"start": v(61.18, -55.1) * mm, "end": v(58.04, -53.4) * mm});
            skLineSegment(sketch, "E1885", {"start": v(58.04, -53.4) * mm, "end": v(60.85, -47.15) * mm});
            skLineSegment(sketch, "E1886", {"start": v(60.85, -47.15) * mm, "end": v(64.22, -48.37) * mm});
            skLineSegment(sketch, "E1887", {"start": v(64.22, -48.37) * mm, "end": v(64.24, -48.38) * mm});
            skLineSegment(sketch, "E1888", {"start": v(64.24, -48.38) * mm, "end": v(64.28, -48.4) * mm});
            skLineSegment(sketch, "E1889", {"start": v(64.28, -48.4) * mm, "end": v(64.34, -48.41) * mm});
            skLineSegment(sketch, "E1890", {"start": v(64.34, -48.41) * mm, "end": v(64.42, -48.43) * mm});
            skLineSegment(sketch, "E1891", {"start": v(64.42, -48.43) * mm, "end": v(64.52, -48.46) * mm});
            skLineSegment(sketch, "E1892", {"start": v(64.52, -48.46) * mm, "end": v(64.64, -48.48) * mm});
            skLineSegment(sketch, "E1893", {"start": v(64.64, -48.48) * mm, "end": v(64.77, -48.51) * mm});
            skLineSegment(sketch, "E1894", {"start": v(64.77, -48.51) * mm, "end": v(64.93, -48.54) * mm});
            skLineSegment(sketch, "E1895", {"start": v(64.93, -48.54) * mm, "end": v(65.1, -48.57) * mm});
            skLineSegment(sketch, "E1896", {"start": v(65.1, -48.57) * mm, "end": v(65.3, -48.6) * mm});
            skLineSegment(sketch, "E1897", {"start": v(65.3, -48.6) * mm, "end": v(65.5, -48.63) * mm});
            skLineSegment(sketch, "E1898", {"start": v(65.5, -48.63) * mm, "end": v(65.74, -48.65) * mm});
            skLineSegment(sketch, "E1899", {"start": v(65.74, -48.65) * mm, "end": v(65.99, -48.67) * mm});
            skLineSegment(sketch, "E1900", {"start": v(65.99, -48.67) * mm, "end": v(66.25, -48.7) * mm});
            skLineSegment(sketch, "E1901", {"start": v(66.25, -48.7) * mm, "end": v(66.54, -48.7) * mm});
            skLineSegment(sketch, "E1902", {"start": v(66.54, -48.7) * mm, "end": v(66.85, -48.72) * mm});
            skLineSegment(sketch, "E1903", {"start": v(66.85, -48.72) * mm, "end": v(67.17, -48.72) * mm});
            skLineSegment(sketch, "E1904", {"start": v(67.17, -48.72) * mm, "end": v(67.52, -48.72) * mm});
            skLineSegment(sketch, "E1905", {"start": v(67.52, -48.72) * mm, "end": v(67.88, -48.7) * mm});
            skLineSegment(sketch, "E1906", {"start": v(67.88, -48.7) * mm, "end": v(68.26, -48.7) * mm});
            skLineSegment(sketch, "E1907", {"start": v(68.26, -48.7) * mm, "end": v(68.66, -48.66) * mm});
            skLineSegment(sketch, "E1908", {"start": v(68.66, -48.66) * mm, "end": v(69.08, -48.63) * mm});
            skLineSegment(sketch, "E1909", {"start": v(69.08, -48.63) * mm, "end": v(69.51, -48.58) * mm});
            skLineSegment(sketch, "E1910", {"start": v(69.51, -48.58) * mm, "end": v(69.97, -48.53) * mm});
            skLineSegment(sketch, "E1911", {"start": v(69.97, -48.53) * mm, "end": v(70.44, -48.46) * mm});
            skLineSegment(sketch, "E1912", {"start": v(70.44, -48.46) * mm, "end": v(70.92, -48.38) * mm});
            skLineSegment(sketch, "E1913", {"start": v(70.92, -48.38) * mm, "end": v(71.43, -48.28) * mm});
            skLineSegment(sketch, "E1914", {"start": v(71.43, -48.28) * mm, "end": v(71.95, -48.18) * mm});
            skLineSegment(sketch, "E1915", {"start": v(71.95, -48.18) * mm, "end": v(72.48, -48.06) * mm});
            skLineSegment(sketch, "E1916", {"start": v(72.48, -48.06) * mm, "end": v(73.04, -47.92) * mm});
            skLineSegment(sketch, "E1917", {"start": v(73.04, -47.92) * mm, "end": v(73.6, -47.77) * mm});
            skLineSegment(sketch, "E1918", {"start": v(73.6, -47.77) * mm, "end": v(74, -47.55) * mm});
            skLineSegment(sketch, "E1919", {"start": v(74, -47.55) * mm, "end": v(74.88, -44.11) * mm});
            skLineSegment(sketch, "E1920", {"start": v(74.88, -44.11) * mm, "end": v(74.63, -43.73) * mm});
            skLineSegment(sketch, "E1921", {"start": v(74.63, -43.73) * mm, "end": v(74.2, -43.33) * mm});
            skLineSegment(sketch, "E1922", {"start": v(74.2, -43.33) * mm, "end": v(73.78, -42.94) * mm});
            skLineSegment(sketch, "E1923", {"start": v(73.78, -42.94) * mm, "end": v(73.37, -42.58) * mm});
            skLineSegment(sketch, "E1924", {"start": v(73.37, -42.58) * mm, "end": v(72.96, -42.24) * mm});
            skLineSegment(sketch, "E1925", {"start": v(72.96, -42.24) * mm, "end": v(72.56, -41.92) * mm});
            skLineSegment(sketch, "E1926", {"start": v(72.56, -41.92) * mm, "end": v(72.17, -41.62) * mm});
            skLineSegment(sketch, "E1927", {"start": v(72.17, -41.62) * mm, "end": v(71.8, -41.33) * mm});
            skLineSegment(sketch, "E1928", {"start": v(71.8, -41.33) * mm, "end": v(71.42, -41.07) * mm});
            skLineSegment(sketch, "E1929", {"start": v(71.42, -41.07) * mm, "end": v(71.06, -40.82) * mm});
            skLineSegment(sketch, "E1930", {"start": v(71.06, -40.82) * mm, "end": v(70.71, -40.59) * mm});
            skLineSegment(sketch, "E1931", {"start": v(70.71, -40.59) * mm, "end": v(70.37, -40.37) * mm});
            skLineSegment(sketch, "E1932", {"start": v(70.37, -40.37) * mm, "end": v(70.05, -40.18) * mm});
            skLineSegment(sketch, "E1933", {"start": v(70.05, -40.18) * mm, "end": v(69.73, -40) * mm});
            skLineSegment(sketch, "E1934", {"start": v(69.73, -40) * mm, "end": v(69.43, -39.83) * mm});
            skLineSegment(sketch, "E1935", {"start": v(69.43, -39.83) * mm, "end": v(69.14, -39.68) * mm});
            skLineSegment(sketch, "E1936", {"start": v(69.14, -39.68) * mm, "end": v(68.87, -39.54) * mm});
            skLineSegment(sketch, "E1937", {"start": v(68.87, -39.54) * mm, "end": v(68.61, -39.41) * mm});
            skLineSegment(sketch, "E1938", {"start": v(68.61, -39.41) * mm, "end": v(68.37, -39.3) * mm});
            skLineSegment(sketch, "E1939", {"start": v(68.37, -39.3) * mm, "end": v(68.14, -39.2) * mm});
            skLineSegment(sketch, "E1940", {"start": v(68.14, -39.2) * mm, "end": v(67.92, -39.11) * mm});
            skLineSegment(sketch, "E1941", {"start": v(67.92, -39.11) * mm, "end": v(67.72, -39.04) * mm});
            skLineSegment(sketch, "E1942", {"start": v(67.72, -39.04) * mm, "end": v(67.54, -38.97) * mm});
            skLineSegment(sketch, "E1943", {"start": v(67.54, -38.97) * mm, "end": v(67.37, -38.91) * mm});
            skLineSegment(sketch, "E1944", {"start": v(67.37, -38.91) * mm, "end": v(67.22, -38.87) * mm});
            skLineSegment(sketch, "E1945", {"start": v(67.22, -38.87) * mm, "end": v(67.1, -38.83) * mm});
            skLineSegment(sketch, "E1946", {"start": v(67.1, -38.83) * mm, "end": v(66.98, -38.8) * mm});
            skLineSegment(sketch, "E1947", {"start": v(66.98, -38.8) * mm, "end": v(66.88, -38.77) * mm});
            skLineSegment(sketch, "E1948", {"start": v(66.88, -38.77) * mm, "end": v(66.8, -38.75) * mm});
            skLineSegment(sketch, "E1949", {"start": v(66.8, -38.75) * mm, "end": v(66.74, -38.74) * mm});
            skLineSegment(sketch, "E1950", {"start": v(66.74, -38.74) * mm, "end": v(66.7, -38.73) * mm});
            skLineSegment(sketch, "E1951", {"start": v(66.7, -38.73) * mm, "end": v(66.67, -38.72) * mm});
            skLineSegment(sketch, "E1952", {"start": v(66.67, -38.72) * mm, "end": v(63.13, -38.2) * mm});
            skLineSegment(sketch, "E1953", {"start": v(63.13, -38.2) * mm, "end": v(63.64, -31.36) * mm});
            skSolve(sketch);
        }
        {
            var Q0;
            Q0=makeQuery(id+"F0.imprint","IMPRINT",FACE,{"disambiguationData":[TD([[makeQuery(id+"F0.imprint","IMPRINT",EDGE,{"derivedFrom":sQuery(id+"F0.wireOp",EDGE,"E730")}),1.0]])]});
            var Q1;
            Q1=makeQuery(id+"F0.imprint","IMPRINT",FACE,{"disambiguationData":[TD([[makeQuery(id+"F0.imprint","IMPRINT",EDGE,{"derivedFrom":sQuery(id+"F0.wireOp",EDGE,"E0")}),1.0]])]});
            extrude(context, id + "F1", {"entities" : qUnion([Q0, Q1]), "depth" : 25 * mm});
        }
        {
            var Q0;
            Q0=makeQuery(id+"F1.opExtrude","SWEPT_BODY",BODY,{"disambiguationData":[OSD([sQuery(id+"F0.wireOp",EDGE,"E0"),sQuery(id+"F0.wireOp",EDGE,"E1"),sQuery(id+"F0.wireOp",EDGE,"E2"),sQuery(id+"F0.wireOp",EDGE,"E3"),sQuery(id+"F0.wireOp",EDGE,"E4"),sQuery(id+"F0.wireOp",EDGE,"E5"),sQuery(id+"F0.wireOp",EDGE,"E6"),sQuery(id+"F0.wireOp",EDGE,"E7"),sQuery(id+"F0.wireOp",EDGE,"E8"),sQuery(id+"F0.wireOp",EDGE,"E9"),sQuery(id+"F0.wireOp",EDGE,"E10"),sQuery(id+"F0.wireOp",EDGE,"E11"),sQuery(id+"F0.wireOp",EDGE,"E12"),sQuery(id+"F0.wireOp",EDGE,"E13"),sQuery(id+"F0.wireOp",EDGE,"E14"),sQuery(id+"F0.wireOp",EDGE,"E15"),sQuery(id+"F0.wireOp",EDGE,"E16"),sQuery(id+"F0.wireOp",EDGE,"E17"),sQuery(id+"F0.wireOp",EDGE,"E18"),sQuery(id+"F0.wireOp",EDGE,"E19"),sQuery(id+"F0.wireOp",EDGE,"E20"),sQuery(id+"F0.wireOp",EDGE,"E21"),sQuery(id+"F0.wireOp",EDGE,"E22"),sQuery(id+"F0.wireOp",EDGE,"E23"),sQuery(id+"F0.wireOp",EDGE,"E24"),sQuery(id+"F0.wireOp",EDGE,"E25"),sQuery(id+"F0.wireOp",EDGE,"E26"),sQuery(id+"F0.wireOp",EDGE,"E27"),sQuery(id+"F0.wireOp",EDGE,"E28"),sQuery(id+"F0.wireOp",EDGE,"E29"),sQuery(id+"F0.wireOp",EDGE,"E30"),sQuery(id+"F0.wireOp",EDGE,"E31"),sQuery(id+"F0.wireOp",EDGE,"E32"),sQuery(id+"F0.wireOp",EDGE,"E33"),sQuery(id+"F0.wireOp",EDGE,"E34"),sQuery(id+"F0.wireOp",EDGE,"E35"),sQuery(id+"F0.wireOp",EDGE,"E36"),sQuery(id+"F0.wireOp",EDGE,"E37"),sQuery(id+"F0.wireOp",EDGE,"E38"),sQuery(id+"F0.wireOp",EDGE,"E39"),sQuery(id+"F0.wireOp",EDGE,"E40"),sQuery(id+"F0.wireOp",EDGE,"E41"),sQuery(id+"F0.wireOp",EDGE,"E42"),sQuery(id+"F0.wireOp",EDGE,"E43"),sQuery(id+"F0.wireOp",EDGE,"E44"),sQuery(id+"F0.wireOp",EDGE,"E45"),sQuery(id+"F0.wireOp",EDGE,"E46"),sQuery(id+"F0.wireOp",EDGE,"E47"),sQuery(id+"F0.wireOp",EDGE,"E48"),sQuery(id+"F0.wireOp",EDGE,"E49"),sQuery(id+"F0.wireOp",EDGE,"E50"),sQuery(id+"F0.wireOp",EDGE,"E51"),sQuery(id+"F0.wireOp",EDGE,"E52"),sQuery(id+"F0.wireOp",EDGE,"E53"),sQuery(id+"F0.wireOp",EDGE,"E54"),sQuery(id+"F0.wireOp",EDGE,"E55"),sQuery(id+"F0.wireOp",EDGE,"E56"),sQuery(id+"F0.wireOp",EDGE,"E57"),sQuery(id+"F0.wireOp",EDGE,"E58"),sQuery(id+"F0.wireOp",EDGE,"E59"),sQuery(id+"F0.wireOp",EDGE,"E60"),sQuery(id+"F0.wireOp",EDGE,"E61"),sQuery(id+"F0.wireOp",EDGE,"E62"),sQuery(id+"F0.wireOp",EDGE,"E63"),sQuery(id+"F0.wireOp",EDGE,"E64"),sQuery(id+"F0.wireOp",EDGE,"E65"),sQuery(id+"F0.wireOp",EDGE,"E66"),sQuery(id+"F0.wireOp",EDGE,"E67"),sQuery(id+"F0.wireOp",EDGE,"E68"),sQuery(id+"F0.wireOp",EDGE,"E69"),sQuery(id+"F0.wireOp",EDGE,"E70"),sQuery(id+"F0.wireOp",EDGE,"E71"),sQuery(id+"F0.wireOp",EDGE,"E72"),sQuery(id+"F0.wireOp",EDGE,"E73"),sQuery(id+"F0.wireOp",EDGE,"E74"),sQuery(id+"F0.wireOp",EDGE,"E75"),sQuery(id+"F0.wireOp",EDGE,"E76"),sQuery(id+"F0.wireOp",EDGE,"E77"),sQuery(id+"F0.wireOp",EDGE,"E78"),sQuery(id+"F0.wireOp",EDGE,"E79"),sQuery(id+"F0.wireOp",EDGE,"E80"),sQuery(id+"F0.wireOp",EDGE,"E81"),sQuery(id+"F0.wireOp",EDGE,"E82"),sQuery(id+"F0.wireOp",EDGE,"E83"),sQuery(id+"F0.wireOp",EDGE,"E84"),sQuery(id+"F0.wireOp",EDGE,"E85"),sQuery(id+"F0.wireOp",EDGE,"E86"),sQuery(id+"F0.wireOp",EDGE,"E87"),sQuery(id+"F0.wireOp",EDGE,"E88"),sQuery(id+"F0.wireOp",EDGE,"E89"),sQuery(id+"F0.wireOp",EDGE,"E90"),sQuery(id+"F0.wireOp",EDGE,"E91"),sQuery(id+"F0.wireOp",EDGE,"E92"),sQuery(id+"F0.wireOp",EDGE,"E93"),sQuery(id+"F0.wireOp",EDGE,"E94"),sQuery(id+"F0.wireOp",EDGE,"E95"),sQuery(id+"F0.wireOp",EDGE,"E96"),sQuery(id+"F0.wireOp",EDGE,"E97"),sQuery(id+"F0.wireOp",EDGE,"E98"),sQuery(id+"F0.wireOp",EDGE,"E99"),sQuery(id+"F0.wireOp",EDGE,"E100"),sQuery(id+"F0.wireOp",EDGE,"E101"),sQuery(id+"F0.wireOp",EDGE,"E102"),sQuery(id+"F0.wireOp",EDGE,"E103"),sQuery(id+"F0.wireOp",EDGE,"E104"),sQuery(id+"F0.wireOp",EDGE,"E105"),sQuery(id+"F0.wireOp",EDGE,"E106"),sQuery(id+"F0.wireOp",EDGE,"E107"),sQuery(id+"F0.wireOp",EDGE,"E108"),sQuery(id+"F0.wireOp",EDGE,"E109"),sQuery(id+"F0.wireOp",EDGE,"E110"),sQuery(id+"F0.wireOp",EDGE,"E111"),sQuery(id+"F0.wireOp",EDGE,"E112"),sQuery(id+"F0.wireOp",EDGE,"E113"),sQuery(id+"F0.wireOp",EDGE,"E114"),sQuery(id+"F0.wireOp",EDGE,"E115"),sQuery(id+"F0.wireOp",EDGE,"E116"),sQuery(id+"F0.wireOp",EDGE,"E117"),sQuery(id+"F0.wireOp",EDGE,"E118"),sQuery(id+"F0.wireOp",EDGE,"E119"),sQuery(id+"F0.wireOp",EDGE,"E120"),sQuery(id+"F0.wireOp",EDGE,"E121"),sQuery(id+"F0.wireOp",EDGE,"E122"),sQuery(id+"F0.wireOp",EDGE,"E123"),sQuery(id+"F0.wireOp",EDGE,"E124"),sQuery(id+"F0.wireOp",EDGE,"E125"),sQuery(id+"F0.wireOp",EDGE,"E126"),sQuery(id+"F0.wireOp",EDGE,"E127"),sQuery(id+"F0.wireOp",EDGE,"E128"),sQuery(id+"F0.wireOp",EDGE,"E129"),sQuery(id+"F0.wireOp",EDGE,"E130"),sQuery(id+"F0.wireOp",EDGE,"E131"),sQuery(id+"F0.wireOp",EDGE,"E132"),sQuery(id+"F0.wireOp",EDGE,"E133"),sQuery(id+"F0.wireOp",EDGE,"E134"),sQuery(id+"F0.wireOp",EDGE,"E135"),sQuery(id+"F0.wireOp",EDGE,"E136"),sQuery(id+"F0.wireOp",EDGE,"E137"),sQuery(id+"F0.wireOp",EDGE,"E138"),sQuery(id+"F0.wireOp",EDGE,"E139"),sQuery(id+"F0.wireOp",EDGE,"E140"),sQuery(id+"F0.wireOp",EDGE,"E141"),sQuery(id+"F0.wireOp",EDGE,"E142"),sQuery(id+"F0.wireOp",EDGE,"E143"),sQuery(id+"F0.wireOp",EDGE,"E144"),sQuery(id+"F0.wireOp",EDGE,"E145"),sQuery(id+"F0.wireOp",EDGE,"E146"),sQuery(id+"F0.wireOp",EDGE,"E147"),sQuery(id+"F0.wireOp",EDGE,"E148"),sQuery(id+"F0.wireOp",EDGE,"E149"),sQuery(id+"F0.wireOp",EDGE,"E150"),sQuery(id+"F0.wireOp",EDGE,"E151"),sQuery(id+"F0.wireOp",EDGE,"E152"),sQuery(id+"F0.wireOp",EDGE,"E153"),sQuery(id+"F0.wireOp",EDGE,"E154"),sQuery(id+"F0.wireOp",EDGE,"E155"),sQuery(id+"F0.wireOp",EDGE,"E156"),sQuery(id+"F0.wireOp",EDGE,"E157"),sQuery(id+"F0.wireOp",EDGE,"E158"),sQuery(id+"F0.wireOp",EDGE,"E159"),sQuery(id+"F0.wireOp",EDGE,"E160"),sQuery(id+"F0.wireOp",EDGE,"E161"),sQuery(id+"F0.wireOp",EDGE,"E162"),sQuery(id+"F0.wireOp",EDGE,"E163"),sQuery(id+"F0.wireOp",EDGE,"E164"),sQuery(id+"F0.wireOp",EDGE,"E165"),sQuery(id+"F0.wireOp",EDGE,"E166"),sQuery(id+"F0.wireOp",EDGE,"E167"),sQuery(id+"F0.wireOp",EDGE,"E168"),sQuery(id+"F0.wireOp",EDGE,"E169"),sQuery(id+"F0.wireOp",EDGE,"E170"),sQuery(id+"F0.wireOp",EDGE,"E171"),sQuery(id+"F0.wireOp",EDGE,"E172"),sQuery(id+"F0.wireOp",EDGE,"E173"),sQuery(id+"F0.wireOp",EDGE,"E174"),sQuery(id+"F0.wireOp",EDGE,"E175"),sQuery(id+"F0.wireOp",EDGE,"E176"),sQuery(id+"F0.wireOp",EDGE,"E177"),sQuery(id+"F0.wireOp",EDGE,"E178"),sQuery(id+"F0.wireOp",EDGE,"E179"),sQuery(id+"F0.wireOp",EDGE,"E180"),sQuery(id+"F0.wireOp",EDGE,"E181"),sQuery(id+"F0.wireOp",EDGE,"E182"),sQuery(id+"F0.wireOp",EDGE,"E183"),sQuery(id+"F0.wireOp",EDGE,"E184"),sQuery(id+"F0.wireOp",EDGE,"E185"),sQuery(id+"F0.wireOp",EDGE,"E186"),sQuery(id+"F0.wireOp",EDGE,"E187"),sQuery(id+"F0.wireOp",EDGE,"E188"),sQuery(id+"F0.wireOp",EDGE,"E189"),sQuery(id+"F0.wireOp",EDGE,"E190"),sQuery(id+"F0.wireOp",EDGE,"E191"),sQuery(id+"F0.wireOp",EDGE,"E192"),sQuery(id+"F0.wireOp",EDGE,"E193"),sQuery(id+"F0.wireOp",EDGE,"E194"),sQuery(id+"F0.wireOp",EDGE,"E195"),sQuery(id+"F0.wireOp",EDGE,"E196"),sQuery(id+"F0.wireOp",EDGE,"E197"),sQuery(id+"F0.wireOp",EDGE,"E198"),sQuery(id+"F0.wireOp",EDGE,"E199"),sQuery(id+"F0.wireOp",EDGE,"E200"),sQuery(id+"F0.wireOp",EDGE,"E201"),sQuery(id+"F0.wireOp",EDGE,"E202"),sQuery(id+"F0.wireOp",EDGE,"E203"),sQuery(id+"F0.wireOp",EDGE,"E204"),sQuery(id+"F0.wireOp",EDGE,"E205"),sQuery(id+"F0.wireOp",EDGE,"E206"),sQuery(id+"F0.wireOp",EDGE,"E207"),sQuery(id+"F0.wireOp",EDGE,"E208"),sQuery(id+"F0.wireOp",EDGE,"E209"),sQuery(id+"F0.wireOp",EDGE,"E210"),sQuery(id+"F0.wireOp",EDGE,"E211"),sQuery(id+"F0.wireOp",EDGE,"E212"),sQuery(id+"F0.wireOp",EDGE,"E213"),sQuery(id+"F0.wireOp",EDGE,"E214"),sQuery(id+"F0.wireOp",EDGE,"E215"),sQuery(id+"F0.wireOp",EDGE,"E216"),sQuery(id+"F0.wireOp",EDGE,"E217"),sQuery(id+"F0.wireOp",EDGE,"E218"),sQuery(id+"F0.wireOp",EDGE,"E219"),sQuery(id+"F0.wireOp",EDGE,"E220"),sQuery(id+"F0.wireOp",EDGE,"E221"),sQuery(id+"F0.wireOp",EDGE,"E222"),sQuery(id+"F0.wireOp",EDGE,"E223"),sQuery(id+"F0.wireOp",EDGE,"E224"),sQuery(id+"F0.wireOp",EDGE,"E225"),sQuery(id+"F0.wireOp",EDGE,"E226"),sQuery(id+"F0.wireOp",EDGE,"E227"),sQuery(id+"F0.wireOp",EDGE,"E228"),sQuery(id+"F0.wireOp",EDGE,"E229"),sQuery(id+"F0.wireOp",EDGE,"E230"),sQuery(id+"F0.wireOp",EDGE,"E231"),sQuery(id+"F0.wireOp",EDGE,"E232"),sQuery(id+"F0.wireOp",EDGE,"E233"),sQuery(id+"F0.wireOp",EDGE,"E234"),sQuery(id+"F0.wireOp",EDGE,"E235"),sQuery(id+"F0.wireOp",EDGE,"E236"),sQuery(id+"F0.wireOp",EDGE,"E237"),sQuery(id+"F0.wireOp",EDGE,"E238"),sQuery(id+"F0.wireOp",EDGE,"E239"),sQuery(id+"F0.wireOp",EDGE,"E240"),sQuery(id+"F0.wireOp",EDGE,"E241"),sQuery(id+"F0.wireOp",EDGE,"E242"),sQuery(id+"F0.wireOp",EDGE,"E243"),sQuery(id+"F0.wireOp",EDGE,"E244"),sQuery(id+"F0.wireOp",EDGE,"E245"),sQuery(id+"F0.wireOp",EDGE,"E246"),sQuery(id+"F0.wireOp",EDGE,"E247"),sQuery(id+"F0.wireOp",EDGE,"E248"),sQuery(id+"F0.wireOp",EDGE,"E249"),sQuery(id+"F0.wireOp",EDGE,"E250"),sQuery(id+"F0.wireOp",EDGE,"E251"),sQuery(id+"F0.wireOp",EDGE,"E252"),sQuery(id+"F0.wireOp",EDGE,"E253"),sQuery(id+"F0.wireOp",EDGE,"E254"),sQuery(id+"F0.wireOp",EDGE,"E255"),sQuery(id+"F0.wireOp",EDGE,"E256"),sQuery(id+"F0.wireOp",EDGE,"E257"),sQuery(id+"F0.wireOp",EDGE,"E258"),sQuery(id+"F0.wireOp",EDGE,"E259"),sQuery(id+"F0.wireOp",EDGE,"E260"),sQuery(id+"F0.wireOp",EDGE,"E261"),sQuery(id+"F0.wireOp",EDGE,"E262"),sQuery(id+"F0.wireOp",EDGE,"E263"),sQuery(id+"F0.wireOp",EDGE,"E264"),sQuery(id+"F0.wireOp",EDGE,"E265"),sQuery(id+"F0.wireOp",EDGE,"E266"),sQuery(id+"F0.wireOp",EDGE,"E267"),sQuery(id+"F0.wireOp",EDGE,"E268"),sQuery(id+"F0.wireOp",EDGE,"E269"),sQuery(id+"F0.wireOp",EDGE,"E270"),sQuery(id+"F0.wireOp",EDGE,"E271"),sQuery(id+"F0.wireOp",EDGE,"E272"),sQuery(id+"F0.wireOp",EDGE,"E273"),sQuery(id+"F0.wireOp",EDGE,"E274"),sQuery(id+"F0.wireOp",EDGE,"E275"),sQuery(id+"F0.wireOp",EDGE,"E276"),sQuery(id+"F0.wireOp",EDGE,"E277"),sQuery(id+"F0.wireOp",EDGE,"E278"),sQuery(id+"F0.wireOp",EDGE,"E279"),sQuery(id+"F0.wireOp",EDGE,"E280"),sQuery(id+"F0.wireOp",EDGE,"E281"),sQuery(id+"F0.wireOp",EDGE,"E282"),sQuery(id+"F0.wireOp",EDGE,"E283"),sQuery(id+"F0.wireOp",EDGE,"E284"),sQuery(id+"F0.wireOp",EDGE,"E285"),sQuery(id+"F0.wireOp",EDGE,"E286"),sQuery(id+"F0.wireOp",EDGE,"E287"),sQuery(id+"F0.wireOp",EDGE,"E288"),sQuery(id+"F0.wireOp",EDGE,"E289"),sQuery(id+"F0.wireOp",EDGE,"E290"),sQuery(id+"F0.wireOp",EDGE,"E291"),sQuery(id+"F0.wireOp",EDGE,"E292"),sQuery(id+"F0.wireOp",EDGE,"E293"),sQuery(id+"F0.wireOp",EDGE,"E294"),sQuery(id+"F0.wireOp",EDGE,"E295"),sQuery(id+"F0.wireOp",EDGE,"E296"),sQuery(id+"F0.wireOp",EDGE,"E297"),sQuery(id+"F0.wireOp",EDGE,"E298"),sQuery(id+"F0.wireOp",EDGE,"E299"),sQuery(id+"F0.wireOp",EDGE,"E300"),sQuery(id+"F0.wireOp",EDGE,"E301"),sQuery(id+"F0.wireOp",EDGE,"E302"),sQuery(id+"F0.wireOp",EDGE,"E303"),sQuery(id+"F0.wireOp",EDGE,"E304"),sQuery(id+"F0.wireOp",EDGE,"E305"),sQuery(id+"F0.wireOp",EDGE,"E306"),sQuery(id+"F0.wireOp",EDGE,"E307"),sQuery(id+"F0.wireOp",EDGE,"E308"),sQuery(id+"F0.wireOp",EDGE,"E309"),sQuery(id+"F0.wireOp",EDGE,"E310"),sQuery(id+"F0.wireOp",EDGE,"E311"),sQuery(id+"F0.wireOp",EDGE,"E312"),sQuery(id+"F0.wireOp",EDGE,"E313"),sQuery(id+"F0.wireOp",EDGE,"E314"),sQuery(id+"F0.wireOp",EDGE,"E315"),sQuery(id+"F0.wireOp",EDGE,"E316"),sQuery(id+"F0.wireOp",EDGE,"E317"),sQuery(id+"F0.wireOp",EDGE,"E318"),sQuery(id+"F0.wireOp",EDGE,"E319"),sQuery(id+"F0.wireOp",EDGE,"E320"),sQuery(id+"F0.wireOp",EDGE,"E321"),sQuery(id+"F0.wireOp",EDGE,"E322"),sQuery(id+"F0.wireOp",EDGE,"E323"),sQuery(id+"F0.wireOp",EDGE,"E324"),sQuery(id+"F0.wireOp",EDGE,"E325"),sQuery(id+"F0.wireOp",EDGE,"E326"),sQuery(id+"F0.wireOp",EDGE,"E327"),sQuery(id+"F0.wireOp",EDGE,"E328"),sQuery(id+"F0.wireOp",EDGE,"E329"),sQuery(id+"F0.wireOp",EDGE,"E330"),sQuery(id+"F0.wireOp",EDGE,"E331"),sQuery(id+"F0.wireOp",EDGE,"E332"),sQuery(id+"F0.wireOp",EDGE,"E333"),sQuery(id+"F0.wireOp",EDGE,"E334"),sQuery(id+"F0.wireOp",EDGE,"E335"),sQuery(id+"F0.wireOp",EDGE,"E336"),sQuery(id+"F0.wireOp",EDGE,"E337"),sQuery(id+"F0.wireOp",EDGE,"E338"),sQuery(id+"F0.wireOp",EDGE,"E339"),sQuery(id+"F0.wireOp",EDGE,"E340"),sQuery(id+"F0.wireOp",EDGE,"E341"),sQuery(id+"F0.wireOp",EDGE,"E342"),sQuery(id+"F0.wireOp",EDGE,"E343"),sQuery(id+"F0.wireOp",EDGE,"E344"),sQuery(id+"F0.wireOp",EDGE,"E345"),sQuery(id+"F0.wireOp",EDGE,"E346"),sQuery(id+"F0.wireOp",EDGE,"E347"),sQuery(id+"F0.wireOp",EDGE,"E348"),sQuery(id+"F0.wireOp",EDGE,"E349"),sQuery(id+"F0.wireOp",EDGE,"E350"),sQuery(id+"F0.wireOp",EDGE,"E351"),sQuery(id+"F0.wireOp",EDGE,"E352"),sQuery(id+"F0.wireOp",EDGE,"E353"),sQuery(id+"F0.wireOp",EDGE,"E354"),sQuery(id+"F0.wireOp",EDGE,"E355"),sQuery(id+"F0.wireOp",EDGE,"E356"),sQuery(id+"F0.wireOp",EDGE,"E357"),sQuery(id+"F0.wireOp",EDGE,"E358"),sQuery(id+"F0.wireOp",EDGE,"E359"),sQuery(id+"F0.wireOp",EDGE,"E360"),sQuery(id+"F0.wireOp",EDGE,"E361"),sQuery(id+"F0.wireOp",EDGE,"E362"),sQuery(id+"F0.wireOp",EDGE,"E363"),sQuery(id+"F0.wireOp",EDGE,"E364"),sQuery(id+"F0.wireOp",EDGE,"E365"),sQuery(id+"F0.wireOp",EDGE,"E366"),sQuery(id+"F0.wireOp",EDGE,"E367"),sQuery(id+"F0.wireOp",EDGE,"E368"),sQuery(id+"F0.wireOp",EDGE,"E369"),sQuery(id+"F0.wireOp",EDGE,"E370"),sQuery(id+"F0.wireOp",EDGE,"E371"),sQuery(id+"F0.wireOp",EDGE,"E372"),sQuery(id+"F0.wireOp",EDGE,"E373"),sQuery(id+"F0.wireOp",EDGE,"E374"),sQuery(id+"F0.wireOp",EDGE,"E375"),sQuery(id+"F0.wireOp",EDGE,"E376"),sQuery(id+"F0.wireOp",EDGE,"E377"),sQuery(id+"F0.wireOp",EDGE,"E378"),sQuery(id+"F0.wireOp",EDGE,"E379"),sQuery(id+"F0.wireOp",EDGE,"E380"),sQuery(id+"F0.wireOp",EDGE,"E381"),sQuery(id+"F0.wireOp",EDGE,"E382"),sQuery(id+"F0.wireOp",EDGE,"E383"),sQuery(id+"F0.wireOp",EDGE,"E384"),sQuery(id+"F0.wireOp",EDGE,"E385"),sQuery(id+"F0.wireOp",EDGE,"E386"),sQuery(id+"F0.wireOp",EDGE,"E387"),sQuery(id+"F0.wireOp",EDGE,"E388"),sQuery(id+"F0.wireOp",EDGE,"E389"),sQuery(id+"F0.wireOp",EDGE,"E390"),sQuery(id+"F0.wireOp",EDGE,"E391"),sQuery(id+"F0.wireOp",EDGE,"E392"),sQuery(id+"F0.wireOp",EDGE,"E393"),sQuery(id+"F0.wireOp",EDGE,"E394"),sQuery(id+"F0.wireOp",EDGE,"E395"),sQuery(id+"F0.wireOp",EDGE,"E396"),sQuery(id+"F0.wireOp",EDGE,"E397"),sQuery(id+"F0.wireOp",EDGE,"E398"),sQuery(id+"F0.wireOp",EDGE,"E399"),sQuery(id+"F0.wireOp",EDGE,"E400"),sQuery(id+"F0.wireOp",EDGE,"E401"),sQuery(id+"F0.wireOp",EDGE,"E402"),sQuery(id+"F0.wireOp",EDGE,"E403"),sQuery(id+"F0.wireOp",EDGE,"E404"),sQuery(id+"F0.wireOp",EDGE,"E405"),sQuery(id+"F0.wireOp",EDGE,"E406"),sQuery(id+"F0.wireOp",EDGE,"E407"),sQuery(id+"F0.wireOp",EDGE,"E408"),sQuery(id+"F0.wireOp",EDGE,"E409"),sQuery(id+"F0.wireOp",EDGE,"E410"),sQuery(id+"F0.wireOp",EDGE,"E411"),sQuery(id+"F0.wireOp",EDGE,"E412"),sQuery(id+"F0.wireOp",EDGE,"E413"),sQuery(id+"F0.wireOp",EDGE,"E414"),sQuery(id+"F0.wireOp",EDGE,"E415"),sQuery(id+"F0.wireOp",EDGE,"E416"),sQuery(id+"F0.wireOp",EDGE,"E417"),sQuery(id+"F0.wireOp",EDGE,"E418"),sQuery(id+"F0.wireOp",EDGE,"E419"),sQuery(id+"F0.wireOp",EDGE,"E420"),sQuery(id+"F0.wireOp",EDGE,"E421"),sQuery(id+"F0.wireOp",EDGE,"E422"),sQuery(id+"F0.wireOp",EDGE,"E423"),sQuery(id+"F0.wireOp",EDGE,"E424"),sQuery(id+"F0.wireOp",EDGE,"E425"),sQuery(id+"F0.wireOp",EDGE,"E426"),sQuery(id+"F0.wireOp",EDGE,"E427"),sQuery(id+"F0.wireOp",EDGE,"E428"),sQuery(id+"F0.wireOp",EDGE,"E429"),sQuery(id+"F0.wireOp",EDGE,"E430"),sQuery(id+"F0.wireOp",EDGE,"E431"),sQuery(id+"F0.wireOp",EDGE,"E432"),sQuery(id+"F0.wireOp",EDGE,"E433"),sQuery(id+"F0.wireOp",EDGE,"E434"),sQuery(id+"F0.wireOp",EDGE,"E435"),sQuery(id+"F0.wireOp",EDGE,"E436"),sQuery(id+"F0.wireOp",EDGE,"E437"),sQuery(id+"F0.wireOp",EDGE,"E438"),sQuery(id+"F0.wireOp",EDGE,"E439"),sQuery(id+"F0.wireOp",EDGE,"E440"),sQuery(id+"F0.wireOp",EDGE,"E441"),sQuery(id+"F0.wireOp",EDGE,"E442"),sQuery(id+"F0.wireOp",EDGE,"E443"),sQuery(id+"F0.wireOp",EDGE,"E444"),sQuery(id+"F0.wireOp",EDGE,"E445"),sQuery(id+"F0.wireOp",EDGE,"E446"),sQuery(id+"F0.wireOp",EDGE,"E447"),sQuery(id+"F0.wireOp",EDGE,"E448"),sQuery(id+"F0.wireOp",EDGE,"E449"),sQuery(id+"F0.wireOp",EDGE,"E450"),sQuery(id+"F0.wireOp",EDGE,"E451"),sQuery(id+"F0.wireOp",EDGE,"E452"),sQuery(id+"F0.wireOp",EDGE,"E453"),sQuery(id+"F0.wireOp",EDGE,"E454"),sQuery(id+"F0.wireOp",EDGE,"E455"),sQuery(id+"F0.wireOp",EDGE,"E456"),sQuery(id+"F0.wireOp",EDGE,"E457"),sQuery(id+"F0.wireOp",EDGE,"E458"),sQuery(id+"F0.wireOp",EDGE,"E459"),sQuery(id+"F0.wireOp",EDGE,"E460"),sQuery(id+"F0.wireOp",EDGE,"E461"),sQuery(id+"F0.wireOp",EDGE,"E462"),sQuery(id+"F0.wireOp",EDGE,"E463"),sQuery(id+"F0.wireOp",EDGE,"E464"),sQuery(id+"F0.wireOp",EDGE,"E465"),sQuery(id+"F0.wireOp",EDGE,"E466"),sQuery(id+"F0.wireOp",EDGE,"E467"),sQuery(id+"F0.wireOp",EDGE,"E468"),sQuery(id+"F0.wireOp",EDGE,"E469"),sQuery(id+"F0.wireOp",EDGE,"E470"),sQuery(id+"F0.wireOp",EDGE,"E471"),sQuery(id+"F0.wireOp",EDGE,"E472"),sQuery(id+"F0.wireOp",EDGE,"E473"),sQuery(id+"F0.wireOp",EDGE,"E474"),sQuery(id+"F0.wireOp",EDGE,"E475"),sQuery(id+"F0.wireOp",EDGE,"E476"),sQuery(id+"F0.wireOp",EDGE,"E477"),sQuery(id+"F0.wireOp",EDGE,"E478"),sQuery(id+"F0.wireOp",EDGE,"E479"),sQuery(id+"F0.wireOp",EDGE,"E480"),sQuery(id+"F0.wireOp",EDGE,"E481"),sQuery(id+"F0.wireOp",EDGE,"E482"),sQuery(id+"F0.wireOp",EDGE,"E483"),sQuery(id+"F0.wireOp",EDGE,"E484"),sQuery(id+"F0.wireOp",EDGE,"E485"),sQuery(id+"F0.wireOp",EDGE,"E486"),sQuery(id+"F0.wireOp",EDGE,"E487"),sQuery(id+"F0.wireOp",EDGE,"E488"),sQuery(id+"F0.wireOp",EDGE,"E489"),sQuery(id+"F0.wireOp",EDGE,"E490"),sQuery(id+"F0.wireOp",EDGE,"E491"),sQuery(id+"F0.wireOp",EDGE,"E492"),sQuery(id+"F0.wireOp",EDGE,"E493"),sQuery(id+"F0.wireOp",EDGE,"E494"),sQuery(id+"F0.wireOp",EDGE,"E495"),sQuery(id+"F0.wireOp",EDGE,"E496"),sQuery(id+"F0.wireOp",EDGE,"E497"),sQuery(id+"F0.wireOp",EDGE,"E498"),sQuery(id+"F0.wireOp",EDGE,"E499"),sQuery(id+"F0.wireOp",EDGE,"E500"),sQuery(id+"F0.wireOp",EDGE,"E501"),sQuery(id+"F0.wireOp",EDGE,"E502"),sQuery(id+"F0.wireOp",EDGE,"E503"),sQuery(id+"F0.wireOp",EDGE,"E504"),sQuery(id+"F0.wireOp",EDGE,"E505"),sQuery(id+"F0.wireOp",EDGE,"E506"),sQuery(id+"F0.wireOp",EDGE,"E507"),sQuery(id+"F0.wireOp",EDGE,"E508"),sQuery(id+"F0.wireOp",EDGE,"E509"),sQuery(id+"F0.wireOp",EDGE,"E510"),sQuery(id+"F0.wireOp",EDGE,"E511"),sQuery(id+"F0.wireOp",EDGE,"E512"),sQuery(id+"F0.wireOp",EDGE,"E513"),sQuery(id+"F0.wireOp",EDGE,"E514"),sQuery(id+"F0.wireOp",EDGE,"E515"),sQuery(id+"F0.wireOp",EDGE,"E516"),sQuery(id+"F0.wireOp",EDGE,"E517"),sQuery(id+"F0.wireOp",EDGE,"E518"),sQuery(id+"F0.wireOp",EDGE,"E519"),sQuery(id+"F0.wireOp",EDGE,"E520"),sQuery(id+"F0.wireOp",EDGE,"E521"),sQuery(id+"F0.wireOp",EDGE,"E522"),sQuery(id+"F0.wireOp",EDGE,"E523"),sQuery(id+"F0.wireOp",EDGE,"E524"),sQuery(id+"F0.wireOp",EDGE,"E525"),sQuery(id+"F0.wireOp",EDGE,"E526"),sQuery(id+"F0.wireOp",EDGE,"E527"),sQuery(id+"F0.wireOp",EDGE,"E528"),sQuery(id+"F0.wireOp",EDGE,"E529"),sQuery(id+"F0.wireOp",EDGE,"E530"),sQuery(id+"F0.wireOp",EDGE,"E531"),sQuery(id+"F0.wireOp",EDGE,"E532"),sQuery(id+"F0.wireOp",EDGE,"E533"),sQuery(id+"F0.wireOp",EDGE,"E534"),sQuery(id+"F0.wireOp",EDGE,"E535"),sQuery(id+"F0.wireOp",EDGE,"E536"),sQuery(id+"F0.wireOp",EDGE,"E537"),sQuery(id+"F0.wireOp",EDGE,"E538"),sQuery(id+"F0.wireOp",EDGE,"E539"),sQuery(id+"F0.wireOp",EDGE,"E540"),sQuery(id+"F0.wireOp",EDGE,"E541"),sQuery(id+"F0.wireOp",EDGE,"E542"),sQuery(id+"F0.wireOp",EDGE,"E543"),sQuery(id+"F0.wireOp",EDGE,"E544"),sQuery(id+"F0.wireOp",EDGE,"E545"),sQuery(id+"F0.wireOp",EDGE,"E546"),sQuery(id+"F0.wireOp",EDGE,"E547"),sQuery(id+"F0.wireOp",EDGE,"E548"),sQuery(id+"F0.wireOp",EDGE,"E549"),sQuery(id+"F0.wireOp",EDGE,"E550"),sQuery(id+"F0.wireOp",EDGE,"E551"),sQuery(id+"F0.wireOp",EDGE,"E552"),sQuery(id+"F0.wireOp",EDGE,"E553"),sQuery(id+"F0.wireOp",EDGE,"E554"),sQuery(id+"F0.wireOp",EDGE,"E555"),sQuery(id+"F0.wireOp",EDGE,"E556"),sQuery(id+"F0.wireOp",EDGE,"E557"),sQuery(id+"F0.wireOp",EDGE,"E558"),sQuery(id+"F0.wireOp",EDGE,"E559"),sQuery(id+"F0.wireOp",EDGE,"E560"),sQuery(id+"F0.wireOp",EDGE,"E561"),sQuery(id+"F0.wireOp",EDGE,"E562"),sQuery(id+"F0.wireOp",EDGE,"E563"),sQuery(id+"F0.wireOp",EDGE,"E564"),sQuery(id+"F0.wireOp",EDGE,"E565"),sQuery(id+"F0.wireOp",EDGE,"E566"),sQuery(id+"F0.wireOp",EDGE,"E567"),sQuery(id+"F0.wireOp",EDGE,"E568"),sQuery(id+"F0.wireOp",EDGE,"E569"),sQuery(id+"F0.wireOp",EDGE,"E570"),sQuery(id+"F0.wireOp",EDGE,"E571"),sQuery(id+"F0.wireOp",EDGE,"E572"),sQuery(id+"F0.wireOp",EDGE,"E573"),sQuery(id+"F0.wireOp",EDGE,"E574"),sQuery(id+"F0.wireOp",EDGE,"E575"),sQuery(id+"F0.wireOp",EDGE,"E576"),sQuery(id+"F0.wireOp",EDGE,"E577"),sQuery(id+"F0.wireOp",EDGE,"E578"),sQuery(id+"F0.wireOp",EDGE,"E579"),sQuery(id+"F0.wireOp",EDGE,"E580"),sQuery(id+"F0.wireOp",EDGE,"E581"),sQuery(id+"F0.wireOp",EDGE,"E582"),sQuery(id+"F0.wireOp",EDGE,"E583"),sQuery(id+"F0.wireOp",EDGE,"E584"),sQuery(id+"F0.wireOp",EDGE,"E585"),sQuery(id+"F0.wireOp",EDGE,"E586"),sQuery(id+"F0.wireOp",EDGE,"E587"),sQuery(id+"F0.wireOp",EDGE,"E588"),sQuery(id+"F0.wireOp",EDGE,"E589"),sQuery(id+"F0.wireOp",EDGE,"E590"),sQuery(id+"F0.wireOp",EDGE,"E591"),sQuery(id+"F0.wireOp",EDGE,"E592"),sQuery(id+"F0.wireOp",EDGE,"E593"),sQuery(id+"F0.wireOp",EDGE,"E594"),sQuery(id+"F0.wireOp",EDGE,"E595"),sQuery(id+"F0.wireOp",EDGE,"E596"),sQuery(id+"F0.wireOp",EDGE,"E597"),sQuery(id+"F0.wireOp",EDGE,"E598"),sQuery(id+"F0.wireOp",EDGE,"E599"),sQuery(id+"F0.wireOp",EDGE,"E600"),sQuery(id+"F0.wireOp",EDGE,"E601"),sQuery(id+"F0.wireOp",EDGE,"E602"),sQuery(id+"F0.wireOp",EDGE,"E603"),sQuery(id+"F0.wireOp",EDGE,"E604"),sQuery(id+"F0.wireOp",EDGE,"E605"),sQuery(id+"F0.wireOp",EDGE,"E606"),sQuery(id+"F0.wireOp",EDGE,"E607"),sQuery(id+"F0.wireOp",EDGE,"E608"),sQuery(id+"F0.wireOp",EDGE,"E609"),sQuery(id+"F0.wireOp",EDGE,"E610"),sQuery(id+"F0.wireOp",EDGE,"E611"),sQuery(id+"F0.wireOp",EDGE,"E612"),sQuery(id+"F0.wireOp",EDGE,"E613"),sQuery(id+"F0.wireOp",EDGE,"E614"),sQuery(id+"F0.wireOp",EDGE,"E615"),sQuery(id+"F0.wireOp",EDGE,"E616"),sQuery(id+"F0.wireOp",EDGE,"E617"),sQuery(id+"F0.wireOp",EDGE,"E618"),sQuery(id+"F0.wireOp",EDGE,"E619"),sQuery(id+"F0.wireOp",EDGE,"E620"),sQuery(id+"F0.wireOp",EDGE,"E621"),sQuery(id+"F0.wireOp",EDGE,"E622"),sQuery(id+"F0.wireOp",EDGE,"E623"),sQuery(id+"F0.wireOp",EDGE,"E624"),sQuery(id+"F0.wireOp",EDGE,"E625"),sQuery(id+"F0.wireOp",EDGE,"E626"),sQuery(id+"F0.wireOp",EDGE,"E627"),sQuery(id+"F0.wireOp",EDGE,"E628"),sQuery(id+"F0.wireOp",EDGE,"E629"),sQuery(id+"F0.wireOp",EDGE,"E630"),sQuery(id+"F0.wireOp",EDGE,"E631"),sQuery(id+"F0.wireOp",EDGE,"E632"),sQuery(id+"F0.wireOp",EDGE,"E633"),sQuery(id+"F0.wireOp",EDGE,"E634"),sQuery(id+"F0.wireOp",EDGE,"E635"),sQuery(id+"F0.wireOp",EDGE,"E636"),sQuery(id+"F0.wireOp",EDGE,"E637"),sQuery(id+"F0.wireOp",EDGE,"E638"),sQuery(id+"F0.wireOp",EDGE,"E639"),sQuery(id+"F0.wireOp",EDGE,"E640"),sQuery(id+"F0.wireOp",EDGE,"E641"),sQuery(id+"F0.wireOp",EDGE,"E642"),sQuery(id+"F0.wireOp",EDGE,"E643"),sQuery(id+"F0.wireOp",EDGE,"E644"),sQuery(id+"F0.wireOp",EDGE,"E645"),sQuery(id+"F0.wireOp",EDGE,"E646"),sQuery(id+"F0.wireOp",EDGE,"E647"),sQuery(id+"F0.wireOp",EDGE,"E648"),sQuery(id+"F0.wireOp",EDGE,"E649"),sQuery(id+"F0.wireOp",EDGE,"E650"),sQuery(id+"F0.wireOp",EDGE,"E651"),sQuery(id+"F0.wireOp",EDGE,"E652"),sQuery(id+"F0.wireOp",EDGE,"E653"),sQuery(id+"F0.wireOp",EDGE,"E654"),sQuery(id+"F0.wireOp",EDGE,"E655"),sQuery(id+"F0.wireOp",EDGE,"E656"),sQuery(id+"F0.wireOp",EDGE,"E657"),sQuery(id+"F0.wireOp",EDGE,"E658"),sQuery(id+"F0.wireOp",EDGE,"E659"),sQuery(id+"F0.wireOp",EDGE,"E660"),sQuery(id+"F0.wireOp",EDGE,"E661"),sQuery(id+"F0.wireOp",EDGE,"E662"),sQuery(id+"F0.wireOp",EDGE,"E663"),sQuery(id+"F0.wireOp",EDGE,"E664"),sQuery(id+"F0.wireOp",EDGE,"E665"),sQuery(id+"F0.wireOp",EDGE,"E666"),sQuery(id+"F0.wireOp",EDGE,"E667"),sQuery(id+"F0.wireOp",EDGE,"E668"),sQuery(id+"F0.wireOp",EDGE,"E669"),sQuery(id+"F0.wireOp",EDGE,"E670"),sQuery(id+"F0.wireOp",EDGE,"E671"),sQuery(id+"F0.wireOp",EDGE,"E672"),sQuery(id+"F0.wireOp",EDGE,"E673"),sQuery(id+"F0.wireOp",EDGE,"E674"),sQuery(id+"F0.wireOp",EDGE,"E675"),sQuery(id+"F0.wireOp",EDGE,"E676"),sQuery(id+"F0.wireOp",EDGE,"E677"),sQuery(id+"F0.wireOp",EDGE,"E678"),sQuery(id+"F0.wireOp",EDGE,"E679"),sQuery(id+"F0.wireOp",EDGE,"E680"),sQuery(id+"F0.wireOp",EDGE,"E681"),sQuery(id+"F0.wireOp",EDGE,"E682"),sQuery(id+"F0.wireOp",EDGE,"E683"),sQuery(id+"F0.wireOp",EDGE,"E684"),sQuery(id+"F0.wireOp",EDGE,"E685"),sQuery(id+"F0.wireOp",EDGE,"E686"),sQuery(id+"F0.wireOp",EDGE,"E687"),sQuery(id+"F0.wireOp",EDGE,"E688"),sQuery(id+"F0.wireOp",EDGE,"E689"),sQuery(id+"F0.wireOp",EDGE,"E690"),sQuery(id+"F0.wireOp",EDGE,"E691"),sQuery(id+"F0.wireOp",EDGE,"E692"),sQuery(id+"F0.wireOp",EDGE,"E693"),sQuery(id+"F0.wireOp",EDGE,"E694"),sQuery(id+"F0.wireOp",EDGE,"E695"),sQuery(id+"F0.wireOp",EDGE,"E696"),sQuery(id+"F0.wireOp",EDGE,"E697"),sQuery(id+"F0.wireOp",EDGE,"E698"),sQuery(id+"F0.wireOp",EDGE,"E699"),sQuery(id+"F0.wireOp",EDGE,"E700"),sQuery(id+"F0.wireOp",EDGE,"E701"),sQuery(id+"F0.wireOp",EDGE,"E702"),sQuery(id+"F0.wireOp",EDGE,"E703"),sQuery(id+"F0.wireOp",EDGE,"E704"),sQuery(id+"F0.wireOp",EDGE,"E705"),sQuery(id+"F0.wireOp",EDGE,"E706"),sQuery(id+"F0.wireOp",EDGE,"E707"),sQuery(id+"F0.wireOp",EDGE,"E708"),sQuery(id+"F0.wireOp",EDGE,"E709"),sQuery(id+"F0.wireOp",EDGE,"E710"),sQuery(id+"F0.wireOp",EDGE,"E711"),sQuery(id+"F0.wireOp",EDGE,"E712"),sQuery(id+"F0.wireOp",EDGE,"E713"),sQuery(id+"F0.wireOp",EDGE,"E714"),sQuery(id+"F0.wireOp",EDGE,"E715"),sQuery(id+"F0.wireOp",EDGE,"E716"),sQuery(id+"F0.wireOp",EDGE,"E717"),sQuery(id+"F0.wireOp",EDGE,"E718"),sQuery(id+"F0.wireOp",EDGE,"E719"),sQuery(id+"F0.wireOp",EDGE,"E720"),sQuery(id+"F0.wireOp",EDGE,"E721"),sQuery(id+"F0.wireOp",EDGE,"E722"),sQuery(id+"F0.wireOp",EDGE,"E723"),sQuery(id+"F0.wireOp",EDGE,"E724"),sQuery(id+"F0.wireOp",EDGE,"E725"),sQuery(id+"F0.wireOp",EDGE,"E726"),sQuery(id+"F0.wireOp",EDGE,"E727")])]});
            var Q1;
            Q1=makeQuery(id+"F1.opExtrude","SWEPT_BODY",BODY,{"disambiguationData":[OSD([sQuery(id+"F0.wireOp",EDGE,"E730"),sQuery(id+"F0.wireOp",EDGE,"E731"),sQuery(id+"F0.wireOp",EDGE,"E732"),sQuery(id+"F0.wireOp",EDGE,"E733"),sQuery(id+"F0.wireOp",EDGE,"E734"),sQuery(id+"F0.wireOp",EDGE,"E735"),sQuery(id+"F0.wireOp",EDGE,"E736"),sQuery(id+"F0.wireOp",EDGE,"E737"),sQuery(id+"F0.wireOp",EDGE,"E738"),sQuery(id+"F0.wireOp",EDGE,"E739"),sQuery(id+"F0.wireOp",EDGE,"E740"),sQuery(id+"F0.wireOp",EDGE,"E741"),sQuery(id+"F0.wireOp",EDGE,"E742"),sQuery(id+"F0.wireOp",EDGE,"E743"),sQuery(id+"F0.wireOp",EDGE,"E744"),sQuery(id+"F0.wireOp",EDGE,"E745"),sQuery(id+"F0.wireOp",EDGE,"E746"),sQuery(id+"F0.wireOp",EDGE,"E747"),sQuery(id+"F0.wireOp",EDGE,"E748"),sQuery(id+"F0.wireOp",EDGE,"E749"),sQuery(id+"F0.wireOp",EDGE,"E750"),sQuery(id+"F0.wireOp",EDGE,"E751"),sQuery(id+"F0.wireOp",EDGE,"E752"),sQuery(id+"F0.wireOp",EDGE,"E753"),sQuery(id+"F0.wireOp",EDGE,"E754"),sQuery(id+"F0.wireOp",EDGE,"E755"),sQuery(id+"F0.wireOp",EDGE,"E756"),sQuery(id+"F0.wireOp",EDGE,"E757"),sQuery(id+"F0.wireOp",EDGE,"E758"),sQuery(id+"F0.wireOp",EDGE,"E759"),sQuery(id+"F0.wireOp",EDGE,"E760"),sQuery(id+"F0.wireOp",EDGE,"E761"),sQuery(id+"F0.wireOp",EDGE,"E762"),sQuery(id+"F0.wireOp",EDGE,"E763"),sQuery(id+"F0.wireOp",EDGE,"E764"),sQuery(id+"F0.wireOp",EDGE,"E765"),sQuery(id+"F0.wireOp",EDGE,"E766"),sQuery(id+"F0.wireOp",EDGE,"E767"),sQuery(id+"F0.wireOp",EDGE,"E768"),sQuery(id+"F0.wireOp",EDGE,"E769"),sQuery(id+"F0.wireOp",EDGE,"E770"),sQuery(id+"F0.wireOp",EDGE,"E771"),sQuery(id+"F0.wireOp",EDGE,"E772"),sQuery(id+"F0.wireOp",EDGE,"E773"),sQuery(id+"F0.wireOp",EDGE,"E774"),sQuery(id+"F0.wireOp",EDGE,"E775"),sQuery(id+"F0.wireOp",EDGE,"E776"),sQuery(id+"F0.wireOp",EDGE,"E777"),sQuery(id+"F0.wireOp",EDGE,"E778"),sQuery(id+"F0.wireOp",EDGE,"E779"),sQuery(id+"F0.wireOp",EDGE,"E780"),sQuery(id+"F0.wireOp",EDGE,"E781"),sQuery(id+"F0.wireOp",EDGE,"E782"),sQuery(id+"F0.wireOp",EDGE,"E783"),sQuery(id+"F0.wireOp",EDGE,"E784"),sQuery(id+"F0.wireOp",EDGE,"E785"),sQuery(id+"F0.wireOp",EDGE,"E786"),sQuery(id+"F0.wireOp",EDGE,"E787"),sQuery(id+"F0.wireOp",EDGE,"E788"),sQuery(id+"F0.wireOp",EDGE,"E789"),sQuery(id+"F0.wireOp",EDGE,"E790"),sQuery(id+"F0.wireOp",EDGE,"E791"),sQuery(id+"F0.wireOp",EDGE,"E792"),sQuery(id+"F0.wireOp",EDGE,"E793"),sQuery(id+"F0.wireOp",EDGE,"E794"),sQuery(id+"F0.wireOp",EDGE,"E795"),sQuery(id+"F0.wireOp",EDGE,"E796"),sQuery(id+"F0.wireOp",EDGE,"E797"),sQuery(id+"F0.wireOp",EDGE,"E798"),sQuery(id+"F0.wireOp",EDGE,"E799"),sQuery(id+"F0.wireOp",EDGE,"E800"),sQuery(id+"F0.wireOp",EDGE,"E801"),sQuery(id+"F0.wireOp",EDGE,"E802"),sQuery(id+"F0.wireOp",EDGE,"E803"),sQuery(id+"F0.wireOp",EDGE,"E804"),sQuery(id+"F0.wireOp",EDGE,"E805"),sQuery(id+"F0.wireOp",EDGE,"E806"),sQuery(id+"F0.wireOp",EDGE,"E807"),sQuery(id+"F0.wireOp",EDGE,"E808"),sQuery(id+"F0.wireOp",EDGE,"E809"),sQuery(id+"F0.wireOp",EDGE,"E810"),sQuery(id+"F0.wireOp",EDGE,"E811"),sQuery(id+"F0.wireOp",EDGE,"E812"),sQuery(id+"F0.wireOp",EDGE,"E813"),sQuery(id+"F0.wireOp",EDGE,"E814"),sQuery(id+"F0.wireOp",EDGE,"E815"),sQuery(id+"F0.wireOp",EDGE,"E816"),sQuery(id+"F0.wireOp",EDGE,"E817"),sQuery(id+"F0.wireOp",EDGE,"E818"),sQuery(id+"F0.wireOp",EDGE,"E819"),sQuery(id+"F0.wireOp",EDGE,"E820"),sQuery(id+"F0.wireOp",EDGE,"E821"),sQuery(id+"F0.wireOp",EDGE,"E822"),sQuery(id+"F0.wireOp",EDGE,"E823"),sQuery(id+"F0.wireOp",EDGE,"E824"),sQuery(id+"F0.wireOp",EDGE,"E825"),sQuery(id+"F0.wireOp",EDGE,"E826"),sQuery(id+"F0.wireOp",EDGE,"E827"),sQuery(id+"F0.wireOp",EDGE,"E828"),sQuery(id+"F0.wireOp",EDGE,"E829"),sQuery(id+"F0.wireOp",EDGE,"E830"),sQuery(id+"F0.wireOp",EDGE,"E831"),sQuery(id+"F0.wireOp",EDGE,"E832"),sQuery(id+"F0.wireOp",EDGE,"E833"),sQuery(id+"F0.wireOp",EDGE,"E834"),sQuery(id+"F0.wireOp",EDGE,"E835"),sQuery(id+"F0.wireOp",EDGE,"E836"),sQuery(id+"F0.wireOp",EDGE,"E837"),sQuery(id+"F0.wireOp",EDGE,"E838"),sQuery(id+"F0.wireOp",EDGE,"E839"),sQuery(id+"F0.wireOp",EDGE,"E840"),sQuery(id+"F0.wireOp",EDGE,"E841"),sQuery(id+"F0.wireOp",EDGE,"E842"),sQuery(id+"F0.wireOp",EDGE,"E843"),sQuery(id+"F0.wireOp",EDGE,"E844"),sQuery(id+"F0.wireOp",EDGE,"E845"),sQuery(id+"F0.wireOp",EDGE,"E846"),sQuery(id+"F0.wireOp",EDGE,"E847"),sQuery(id+"F0.wireOp",EDGE,"E848"),sQuery(id+"F0.wireOp",EDGE,"E849"),sQuery(id+"F0.wireOp",EDGE,"E850"),sQuery(id+"F0.wireOp",EDGE,"E851"),sQuery(id+"F0.wireOp",EDGE,"E852"),sQuery(id+"F0.wireOp",EDGE,"E853"),sQuery(id+"F0.wireOp",EDGE,"E854"),sQuery(id+"F0.wireOp",EDGE,"E855"),sQuery(id+"F0.wireOp",EDGE,"E856"),sQuery(id+"F0.wireOp",EDGE,"E857"),sQuery(id+"F0.wireOp",EDGE,"E858"),sQuery(id+"F0.wireOp",EDGE,"E859"),sQuery(id+"F0.wireOp",EDGE,"E860"),sQuery(id+"F0.wireOp",EDGE,"E861"),sQuery(id+"F0.wireOp",EDGE,"E862"),sQuery(id+"F0.wireOp",EDGE,"E863"),sQuery(id+"F0.wireOp",EDGE,"E864"),sQuery(id+"F0.wireOp",EDGE,"E865"),sQuery(id+"F0.wireOp",EDGE,"E866"),sQuery(id+"F0.wireOp",EDGE,"E867"),sQuery(id+"F0.wireOp",EDGE,"E868"),sQuery(id+"F0.wireOp",EDGE,"E869"),sQuery(id+"F0.wireOp",EDGE,"E870"),sQuery(id+"F0.wireOp",EDGE,"E871"),sQuery(id+"F0.wireOp",EDGE,"E872"),sQuery(id+"F0.wireOp",EDGE,"E873"),sQuery(id+"F0.wireOp",EDGE,"E874"),sQuery(id+"F0.wireOp",EDGE,"E875"),sQuery(id+"F0.wireOp",EDGE,"E876"),sQuery(id+"F0.wireOp",EDGE,"E877"),sQuery(id+"F0.wireOp",EDGE,"E878"),sQuery(id+"F0.wireOp",EDGE,"E879"),sQuery(id+"F0.wireOp",EDGE,"E880"),sQuery(id+"F0.wireOp",EDGE,"E881"),sQuery(id+"F0.wireOp",EDGE,"E882"),sQuery(id+"F0.wireOp",EDGE,"E883"),sQuery(id+"F0.wireOp",EDGE,"E884"),sQuery(id+"F0.wireOp",EDGE,"E885"),sQuery(id+"F0.wireOp",EDGE,"E886"),sQuery(id+"F0.wireOp",EDGE,"E887"),sQuery(id+"F0.wireOp",EDGE,"E888"),sQuery(id+"F0.wireOp",EDGE,"E889"),sQuery(id+"F0.wireOp",EDGE,"E890"),sQuery(id+"F0.wireOp",EDGE,"E891"),sQuery(id+"F0.wireOp",EDGE,"E892"),sQuery(id+"F0.wireOp",EDGE,"E893"),sQuery(id+"F0.wireOp",EDGE,"E894"),sQuery(id+"F0.wireOp",EDGE,"E895"),sQuery(id+"F0.wireOp",EDGE,"E896"),sQuery(id+"F0.wireOp",EDGE,"E897"),sQuery(id+"F0.wireOp",EDGE,"E898"),sQuery(id+"F0.wireOp",EDGE,"E899"),sQuery(id+"F0.wireOp",EDGE,"E900"),sQuery(id+"F0.wireOp",EDGE,"E901"),sQuery(id+"F0.wireOp",EDGE,"E902"),sQuery(id+"F0.wireOp",EDGE,"E903"),sQuery(id+"F0.wireOp",EDGE,"E904"),sQuery(id+"F0.wireOp",EDGE,"E905"),sQuery(id+"F0.wireOp",EDGE,"E906"),sQuery(id+"F0.wireOp",EDGE,"E907"),sQuery(id+"F0.wireOp",EDGE,"E908"),sQuery(id+"F0.wireOp",EDGE,"E909"),sQuery(id+"F0.wireOp",EDGE,"E910"),sQuery(id+"F0.wireOp",EDGE,"E911"),sQuery(id+"F0.wireOp",EDGE,"E912"),sQuery(id+"F0.wireOp",EDGE,"E913"),sQuery(id+"F0.wireOp",EDGE,"E914"),sQuery(id+"F0.wireOp",EDGE,"E915"),sQuery(id+"F0.wireOp",EDGE,"E916"),sQuery(id+"F0.wireOp",EDGE,"E917"),sQuery(id+"F0.wireOp",EDGE,"E918"),sQuery(id+"F0.wireOp",EDGE,"E919"),sQuery(id+"F0.wireOp",EDGE,"E920"),sQuery(id+"F0.wireOp",EDGE,"E921"),sQuery(id+"F0.wireOp",EDGE,"E922"),sQuery(id+"F0.wireOp",EDGE,"E923"),sQuery(id+"F0.wireOp",EDGE,"E924"),sQuery(id+"F0.wireOp",EDGE,"E925"),sQuery(id+"F0.wireOp",EDGE,"E926"),sQuery(id+"F0.wireOp",EDGE,"E927"),sQuery(id+"F0.wireOp",EDGE,"E928"),sQuery(id+"F0.wireOp",EDGE,"E929"),sQuery(id+"F0.wireOp",EDGE,"E930"),sQuery(id+"F0.wireOp",EDGE,"E931"),sQuery(id+"F0.wireOp",EDGE,"E932"),sQuery(id+"F0.wireOp",EDGE,"E933"),sQuery(id+"F0.wireOp",EDGE,"E934"),sQuery(id+"F0.wireOp",EDGE,"E935"),sQuery(id+"F0.wireOp",EDGE,"E936"),sQuery(id+"F0.wireOp",EDGE,"E937"),sQuery(id+"F0.wireOp",EDGE,"E938"),sQuery(id+"F0.wireOp",EDGE,"E939"),sQuery(id+"F0.wireOp",EDGE,"E940"),sQuery(id+"F0.wireOp",EDGE,"E941"),sQuery(id+"F0.wireOp",EDGE,"E942"),sQuery(id+"F0.wireOp",EDGE,"E943"),sQuery(id+"F0.wireOp",EDGE,"E944"),sQuery(id+"F0.wireOp",EDGE,"E945"),sQuery(id+"F0.wireOp",EDGE,"E946"),sQuery(id+"F0.wireOp",EDGE,"E947"),sQuery(id+"F0.wireOp",EDGE,"E948"),sQuery(id+"F0.wireOp",EDGE,"E949"),sQuery(id+"F0.wireOp",EDGE,"E950"),sQuery(id+"F0.wireOp",EDGE,"E951"),sQuery(id+"F0.wireOp",EDGE,"E952"),sQuery(id+"F0.wireOp",EDGE,"E953"),sQuery(id+"F0.wireOp",EDGE,"E954"),sQuery(id+"F0.wireOp",EDGE,"E955"),sQuery(id+"F0.wireOp",EDGE,"E956"),sQuery(id+"F0.wireOp",EDGE,"E957"),sQuery(id+"F0.wireOp",EDGE,"E958"),sQuery(id+"F0.wireOp",EDGE,"E959"),sQuery(id+"F0.wireOp",EDGE,"E960"),sQuery(id+"F0.wireOp",EDGE,"E961"),sQuery(id+"F0.wireOp",EDGE,"E962"),sQuery(id+"F0.wireOp",EDGE,"E963"),sQuery(id+"F0.wireOp",EDGE,"E964"),sQuery(id+"F0.wireOp",EDGE,"E965"),sQuery(id+"F0.wireOp",EDGE,"E966"),sQuery(id+"F0.wireOp",EDGE,"E967"),sQuery(id+"F0.wireOp",EDGE,"E968"),sQuery(id+"F0.wireOp",EDGE,"E969"),sQuery(id+"F0.wireOp",EDGE,"E970"),sQuery(id+"F0.wireOp",EDGE,"E971"),sQuery(id+"F0.wireOp",EDGE,"E972"),sQuery(id+"F0.wireOp",EDGE,"E973"),sQuery(id+"F0.wireOp",EDGE,"E974"),sQuery(id+"F0.wireOp",EDGE,"E975"),sQuery(id+"F0.wireOp",EDGE,"E976"),sQuery(id+"F0.wireOp",EDGE,"E977"),sQuery(id+"F0.wireOp",EDGE,"E978"),sQuery(id+"F0.wireOp",EDGE,"E979"),sQuery(id+"F0.wireOp",EDGE,"E980"),sQuery(id+"F0.wireOp",EDGE,"E981"),sQuery(id+"F0.wireOp",EDGE,"E982"),sQuery(id+"F0.wireOp",EDGE,"E983"),sQuery(id+"F0.wireOp",EDGE,"E984"),sQuery(id+"F0.wireOp",EDGE,"E985"),sQuery(id+"F0.wireOp",EDGE,"E986"),sQuery(id+"F0.wireOp",EDGE,"E987"),sQuery(id+"F0.wireOp",EDGE,"E988"),sQuery(id+"F0.wireOp",EDGE,"E989"),sQuery(id+"F0.wireOp",EDGE,"E990"),sQuery(id+"F0.wireOp",EDGE,"E991"),sQuery(id+"F0.wireOp",EDGE,"E992"),sQuery(id+"F0.wireOp",EDGE,"E993"),sQuery(id+"F0.wireOp",EDGE,"E994"),sQuery(id+"F0.wireOp",EDGE,"E995"),sQuery(id+"F0.wireOp",EDGE,"E996"),sQuery(id+"F0.wireOp",EDGE,"E997"),sQuery(id+"F0.wireOp",EDGE,"E998"),sQuery(id+"F0.wireOp",EDGE,"E999"),sQuery(id+"F0.wireOp",EDGE,"E1000"),sQuery(id+"F0.wireOp",EDGE,"E1001"),sQuery(id+"F0.wireOp",EDGE,"E1002"),sQuery(id+"F0.wireOp",EDGE,"E1003"),sQuery(id+"F0.wireOp",EDGE,"E1004"),sQuery(id+"F0.wireOp",EDGE,"E1005"),sQuery(id+"F0.wireOp",EDGE,"E1006"),sQuery(id+"F0.wireOp",EDGE,"E1007"),sQuery(id+"F0.wireOp",EDGE,"E1008"),sQuery(id+"F0.wireOp",EDGE,"E1009"),sQuery(id+"F0.wireOp",EDGE,"E1010"),sQuery(id+"F0.wireOp",EDGE,"E1011"),sQuery(id+"F0.wireOp",EDGE,"E1012"),sQuery(id+"F0.wireOp",EDGE,"E1013"),sQuery(id+"F0.wireOp",EDGE,"E1014"),sQuery(id+"F0.wireOp",EDGE,"E1015"),sQuery(id+"F0.wireOp",EDGE,"E1016"),sQuery(id+"F0.wireOp",EDGE,"E1017"),sQuery(id+"F0.wireOp",EDGE,"E1018"),sQuery(id+"F0.wireOp",EDGE,"E1019"),sQuery(id+"F0.wireOp",EDGE,"E1020"),sQuery(id+"F0.wireOp",EDGE,"E1021"),sQuery(id+"F0.wireOp",EDGE,"E1022"),sQuery(id+"F0.wireOp",EDGE,"E1023"),sQuery(id+"F0.wireOp",EDGE,"E1024"),sQuery(id+"F0.wireOp",EDGE,"E1025"),sQuery(id+"F0.wireOp",EDGE,"E1026"),sQuery(id+"F0.wireOp",EDGE,"E1027"),sQuery(id+"F0.wireOp",EDGE,"E1028"),sQuery(id+"F0.wireOp",EDGE,"E1029"),sQuery(id+"F0.wireOp",EDGE,"E1030"),sQuery(id+"F0.wireOp",EDGE,"E1031"),sQuery(id+"F0.wireOp",EDGE,"E1032"),sQuery(id+"F0.wireOp",EDGE,"E1033"),sQuery(id+"F0.wireOp",EDGE,"E1034"),sQuery(id+"F0.wireOp",EDGE,"E1035"),sQuery(id+"F0.wireOp",EDGE,"E1036"),sQuery(id+"F0.wireOp",EDGE,"E1037"),sQuery(id+"F0.wireOp",EDGE,"E1038"),sQuery(id+"F0.wireOp",EDGE,"E1039"),sQuery(id+"F0.wireOp",EDGE,"E1040"),sQuery(id+"F0.wireOp",EDGE,"E1041"),sQuery(id+"F0.wireOp",EDGE,"E1042"),sQuery(id+"F0.wireOp",EDGE,"E1043"),sQuery(id+"F0.wireOp",EDGE,"E1044"),sQuery(id+"F0.wireOp",EDGE,"E1045"),sQuery(id+"F0.wireOp",EDGE,"E1046"),sQuery(id+"F0.wireOp",EDGE,"E1047"),sQuery(id+"F0.wireOp",EDGE,"E1048"),sQuery(id+"F0.wireOp",EDGE,"E1049"),sQuery(id+"F0.wireOp",EDGE,"E1050"),sQuery(id+"F0.wireOp",EDGE,"E1051"),sQuery(id+"F0.wireOp",EDGE,"E1052"),sQuery(id+"F0.wireOp",EDGE,"E1053"),sQuery(id+"F0.wireOp",EDGE,"E1054"),sQuery(id+"F0.wireOp",EDGE,"E1055"),sQuery(id+"F0.wireOp",EDGE,"E1056"),sQuery(id+"F0.wireOp",EDGE,"E1057"),sQuery(id+"F0.wireOp",EDGE,"E1058"),sQuery(id+"F0.wireOp",EDGE,"E1059"),sQuery(id+"F0.wireOp",EDGE,"E1060"),sQuery(id+"F0.wireOp",EDGE,"E1061"),sQuery(id+"F0.wireOp",EDGE,"E1062"),sQuery(id+"F0.wireOp",EDGE,"E1063"),sQuery(id+"F0.wireOp",EDGE,"E1064"),sQuery(id+"F0.wireOp",EDGE,"E1065"),sQuery(id+"F0.wireOp",EDGE,"E1066"),sQuery(id+"F0.wireOp",EDGE,"E1067"),sQuery(id+"F0.wireOp",EDGE,"E1068"),sQuery(id+"F0.wireOp",EDGE,"E1069"),sQuery(id+"F0.wireOp",EDGE,"E1070"),sQuery(id+"F0.wireOp",EDGE,"E1071"),sQuery(id+"F0.wireOp",EDGE,"E1072"),sQuery(id+"F0.wireOp",EDGE,"E1073"),sQuery(id+"F0.wireOp",EDGE,"E1074"),sQuery(id+"F0.wireOp",EDGE,"E1075"),sQuery(id+"F0.wireOp",EDGE,"E1076"),sQuery(id+"F0.wireOp",EDGE,"E1077"),sQuery(id+"F0.wireOp",EDGE,"E1078"),sQuery(id+"F0.wireOp",EDGE,"E1079"),sQuery(id+"F0.wireOp",EDGE,"E1080"),sQuery(id+"F0.wireOp",EDGE,"E1081"),sQuery(id+"F0.wireOp",EDGE,"E1082"),sQuery(id+"F0.wireOp",EDGE,"E1083"),sQuery(id+"F0.wireOp",EDGE,"E1084"),sQuery(id+"F0.wireOp",EDGE,"E1085"),sQuery(id+"F0.wireOp",EDGE,"E1086"),sQuery(id+"F0.wireOp",EDGE,"E1087"),sQuery(id+"F0.wireOp",EDGE,"E1088"),sQuery(id+"F0.wireOp",EDGE,"E1089"),sQuery(id+"F0.wireOp",EDGE,"E1090"),sQuery(id+"F0.wireOp",EDGE,"E1091"),sQuery(id+"F0.wireOp",EDGE,"E1092"),sQuery(id+"F0.wireOp",EDGE,"E1093"),sQuery(id+"F0.wireOp",EDGE,"E1094"),sQuery(id+"F0.wireOp",EDGE,"E1095"),sQuery(id+"F0.wireOp",EDGE,"E1096"),sQuery(id+"F0.wireOp",EDGE,"E1097"),sQuery(id+"F0.wireOp",EDGE,"E1098"),sQuery(id+"F0.wireOp",EDGE,"E1099"),sQuery(id+"F0.wireOp",EDGE,"E1100"),sQuery(id+"F0.wireOp",EDGE,"E1101"),sQuery(id+"F0.wireOp",EDGE,"E1102"),sQuery(id+"F0.wireOp",EDGE,"E1103"),sQuery(id+"F0.wireOp",EDGE,"E1104"),sQuery(id+"F0.wireOp",EDGE,"E1105"),sQuery(id+"F0.wireOp",EDGE,"E1106"),sQuery(id+"F0.wireOp",EDGE,"E1107"),sQuery(id+"F0.wireOp",EDGE,"E1108"),sQuery(id+"F0.wireOp",EDGE,"E1109"),sQuery(id+"F0.wireOp",EDGE,"E1110"),sQuery(id+"F0.wireOp",EDGE,"E1111"),sQuery(id+"F0.wireOp",EDGE,"E1112"),sQuery(id+"F0.wireOp",EDGE,"E1113"),sQuery(id+"F0.wireOp",EDGE,"E1114"),sQuery(id+"F0.wireOp",EDGE,"E1115"),sQuery(id+"F0.wireOp",EDGE,"E1116"),sQuery(id+"F0.wireOp",EDGE,"E1117"),sQuery(id+"F0.wireOp",EDGE,"E1118"),sQuery(id+"F0.wireOp",EDGE,"E1119"),sQuery(id+"F0.wireOp",EDGE,"E1120"),sQuery(id+"F0.wireOp",EDGE,"E1121"),sQuery(id+"F0.wireOp",EDGE,"E1122"),sQuery(id+"F0.wireOp",EDGE,"E1123"),sQuery(id+"F0.wireOp",EDGE,"E1124"),sQuery(id+"F0.wireOp",EDGE,"E1125"),sQuery(id+"F0.wireOp",EDGE,"E1126"),sQuery(id+"F0.wireOp",EDGE,"E1127"),sQuery(id+"F0.wireOp",EDGE,"E1128"),sQuery(id+"F0.wireOp",EDGE,"E1129"),sQuery(id+"F0.wireOp",EDGE,"E1130"),sQuery(id+"F0.wireOp",EDGE,"E1131"),sQuery(id+"F0.wireOp",EDGE,"E1132"),sQuery(id+"F0.wireOp",EDGE,"E1133"),sQuery(id+"F0.wireOp",EDGE,"E1134"),sQuery(id+"F0.wireOp",EDGE,"E1135"),sQuery(id+"F0.wireOp",EDGE,"E1136"),sQuery(id+"F0.wireOp",EDGE,"E1137"),sQuery(id+"F0.wireOp",EDGE,"E1138"),sQuery(id+"F0.wireOp",EDGE,"E1139"),sQuery(id+"F0.wireOp",EDGE,"E1140"),sQuery(id+"F0.wireOp",EDGE,"E1141"),sQuery(id+"F0.wireOp",EDGE,"E1142"),sQuery(id+"F0.wireOp",EDGE,"E1143"),sQuery(id+"F0.wireOp",EDGE,"E1144"),sQuery(id+"F0.wireOp",EDGE,"E1145"),sQuery(id+"F0.wireOp",EDGE,"E1146"),sQuery(id+"F0.wireOp",EDGE,"E1147"),sQuery(id+"F0.wireOp",EDGE,"E1148"),sQuery(id+"F0.wireOp",EDGE,"E1149"),sQuery(id+"F0.wireOp",EDGE,"E1150"),sQuery(id+"F0.wireOp",EDGE,"E1151"),sQuery(id+"F0.wireOp",EDGE,"E1152"),sQuery(id+"F0.wireOp",EDGE,"E1153"),sQuery(id+"F0.wireOp",EDGE,"E1154"),sQuery(id+"F0.wireOp",EDGE,"E1155"),sQuery(id+"F0.wireOp",EDGE,"E1156"),sQuery(id+"F0.wireOp",EDGE,"E1157"),sQuery(id+"F0.wireOp",EDGE,"E1158"),sQuery(id+"F0.wireOp",EDGE,"E1159"),sQuery(id+"F0.wireOp",EDGE,"E1160"),sQuery(id+"F0.wireOp",EDGE,"E1161"),sQuery(id+"F0.wireOp",EDGE,"E1162"),sQuery(id+"F0.wireOp",EDGE,"E1163"),sQuery(id+"F0.wireOp",EDGE,"E1164"),sQuery(id+"F0.wireOp",EDGE,"E1165"),sQuery(id+"F0.wireOp",EDGE,"E1166"),sQuery(id+"F0.wireOp",EDGE,"E1167"),sQuery(id+"F0.wireOp",EDGE,"E1168"),sQuery(id+"F0.wireOp",EDGE,"E1169"),sQuery(id+"F0.wireOp",EDGE,"E1170"),sQuery(id+"F0.wireOp",EDGE,"E1171"),sQuery(id+"F0.wireOp",EDGE,"E1172"),sQuery(id+"F0.wireOp",EDGE,"E1173"),sQuery(id+"F0.wireOp",EDGE,"E1174"),sQuery(id+"F0.wireOp",EDGE,"E1175"),sQuery(id+"F0.wireOp",EDGE,"E1176"),sQuery(id+"F0.wireOp",EDGE,"E1177"),sQuery(id+"F0.wireOp",EDGE,"E1178"),sQuery(id+"F0.wireOp",EDGE,"E1179"),sQuery(id+"F0.wireOp",EDGE,"E1180"),sQuery(id+"F0.wireOp",EDGE,"E1181"),sQuery(id+"F0.wireOp",EDGE,"E1182"),sQuery(id+"F0.wireOp",EDGE,"E1183"),sQuery(id+"F0.wireOp",EDGE,"E1184"),sQuery(id+"F0.wireOp",EDGE,"E1185"),sQuery(id+"F0.wireOp",EDGE,"E1186"),sQuery(id+"F0.wireOp",EDGE,"E1187"),sQuery(id+"F0.wireOp",EDGE,"E1188"),sQuery(id+"F0.wireOp",EDGE,"E1189"),sQuery(id+"F0.wireOp",EDGE,"E1190"),sQuery(id+"F0.wireOp",EDGE,"E1191"),sQuery(id+"F0.wireOp",EDGE,"E1192"),sQuery(id+"F0.wireOp",EDGE,"E1193"),sQuery(id+"F0.wireOp",EDGE,"E1194"),sQuery(id+"F0.wireOp",EDGE,"E1195"),sQuery(id+"F0.wireOp",EDGE,"E1196"),sQuery(id+"F0.wireOp",EDGE,"E1197"),sQuery(id+"F0.wireOp",EDGE,"E1198"),sQuery(id+"F0.wireOp",EDGE,"E1199"),sQuery(id+"F0.wireOp",EDGE,"E1200"),sQuery(id+"F0.wireOp",EDGE,"E1201"),sQuery(id+"F0.wireOp",EDGE,"E1202"),sQuery(id+"F0.wireOp",EDGE,"E1203"),sQuery(id+"F0.wireOp",EDGE,"E1204"),sQuery(id+"F0.wireOp",EDGE,"E1205"),sQuery(id+"F0.wireOp",EDGE,"E1206"),sQuery(id+"F0.wireOp",EDGE,"E1207"),sQuery(id+"F0.wireOp",EDGE,"E1208"),sQuery(id+"F0.wireOp",EDGE,"E1209"),sQuery(id+"F0.wireOp",EDGE,"E1210"),sQuery(id+"F0.wireOp",EDGE,"E1211"),sQuery(id+"F0.wireOp",EDGE,"E1212"),sQuery(id+"F0.wireOp",EDGE,"E1213"),sQuery(id+"F0.wireOp",EDGE,"E1214"),sQuery(id+"F0.wireOp",EDGE,"E1215"),sQuery(id+"F0.wireOp",EDGE,"E1216"),sQuery(id+"F0.wireOp",EDGE,"E1217"),sQuery(id+"F0.wireOp",EDGE,"E1218"),sQuery(id+"F0.wireOp",EDGE,"E1219"),sQuery(id+"F0.wireOp",EDGE,"E1220"),sQuery(id+"F0.wireOp",EDGE,"E1221"),sQuery(id+"F0.wireOp",EDGE,"E1222"),sQuery(id+"F0.wireOp",EDGE,"E1223"),sQuery(id+"F0.wireOp",EDGE,"E1224"),sQuery(id+"F0.wireOp",EDGE,"E1225"),sQuery(id+"F0.wireOp",EDGE,"E1226"),sQuery(id+"F0.wireOp",EDGE,"E1227"),sQuery(id+"F0.wireOp",EDGE,"E1228"),sQuery(id+"F0.wireOp",EDGE,"E1229"),sQuery(id+"F0.wireOp",EDGE,"E1230"),sQuery(id+"F0.wireOp",EDGE,"E1231"),sQuery(id+"F0.wireOp",EDGE,"E1232"),sQuery(id+"F0.wireOp",EDGE,"E1233"),sQuery(id+"F0.wireOp",EDGE,"E1234"),sQuery(id+"F0.wireOp",EDGE,"E1235"),sQuery(id+"F0.wireOp",EDGE,"E1236"),sQuery(id+"F0.wireOp",EDGE,"E1237"),sQuery(id+"F0.wireOp",EDGE,"E1238"),sQuery(id+"F0.wireOp",EDGE,"E1239"),sQuery(id+"F0.wireOp",EDGE,"E1240"),sQuery(id+"F0.wireOp",EDGE,"E1241"),sQuery(id+"F0.wireOp",EDGE,"E1242"),sQuery(id+"F0.wireOp",EDGE,"E1243"),sQuery(id+"F0.wireOp",EDGE,"E1244"),sQuery(id+"F0.wireOp",EDGE,"E1245"),sQuery(id+"F0.wireOp",EDGE,"E1246"),sQuery(id+"F0.wireOp",EDGE,"E1247"),sQuery(id+"F0.wireOp",EDGE,"E1248"),sQuery(id+"F0.wireOp",EDGE,"E1249"),sQuery(id+"F0.wireOp",EDGE,"E1250"),sQuery(id+"F0.wireOp",EDGE,"E1251"),sQuery(id+"F0.wireOp",EDGE,"E1252"),sQuery(id+"F0.wireOp",EDGE,"E1253"),sQuery(id+"F0.wireOp",EDGE,"E1254"),sQuery(id+"F0.wireOp",EDGE,"E1255"),sQuery(id+"F0.wireOp",EDGE,"E1256"),sQuery(id+"F0.wireOp",EDGE,"E1257"),sQuery(id+"F0.wireOp",EDGE,"E1258"),sQuery(id+"F0.wireOp",EDGE,"E1259"),sQuery(id+"F0.wireOp",EDGE,"E1260"),sQuery(id+"F0.wireOp",EDGE,"E1261"),sQuery(id+"F0.wireOp",EDGE,"E1262"),sQuery(id+"F0.wireOp",EDGE,"E1263"),sQuery(id+"F0.wireOp",EDGE,"E1264"),sQuery(id+"F0.wireOp",EDGE,"E1265"),sQuery(id+"F0.wireOp",EDGE,"E1266"),sQuery(id+"F0.wireOp",EDGE,"E1267"),sQuery(id+"F0.wireOp",EDGE,"E1268"),sQuery(id+"F0.wireOp",EDGE,"E1269"),sQuery(id+"F0.wireOp",EDGE,"E1270"),sQuery(id+"F0.wireOp",EDGE,"E1271"),sQuery(id+"F0.wireOp",EDGE,"E1272"),sQuery(id+"F0.wireOp",EDGE,"E1273"),sQuery(id+"F0.wireOp",EDGE,"E1274"),sQuery(id+"F0.wireOp",EDGE,"E1275"),sQuery(id+"F0.wireOp",EDGE,"E1276"),sQuery(id+"F0.wireOp",EDGE,"E1277"),sQuery(id+"F0.wireOp",EDGE,"E1278"),sQuery(id+"F0.wireOp",EDGE,"E1279"),sQuery(id+"F0.wireOp",EDGE,"E1280"),sQuery(id+"F0.wireOp",EDGE,"E1281"),sQuery(id+"F0.wireOp",EDGE,"E1282"),sQuery(id+"F0.wireOp",EDGE,"E1283"),sQuery(id+"F0.wireOp",EDGE,"E1284"),sQuery(id+"F0.wireOp",EDGE,"E1285"),sQuery(id+"F0.wireOp",EDGE,"E1286"),sQuery(id+"F0.wireOp",EDGE,"E1287"),sQuery(id+"F0.wireOp",EDGE,"E1288"),sQuery(id+"F0.wireOp",EDGE,"E1289"),sQuery(id+"F0.wireOp",EDGE,"E1290"),sQuery(id+"F0.wireOp",EDGE,"E1291"),sQuery(id+"F0.wireOp",EDGE,"E1292"),sQuery(id+"F0.wireOp",EDGE,"E1293"),sQuery(id+"F0.wireOp",EDGE,"E1294"),sQuery(id+"F0.wireOp",EDGE,"E1295"),sQuery(id+"F0.wireOp",EDGE,"E1296"),sQuery(id+"F0.wireOp",EDGE,"E1297"),sQuery(id+"F0.wireOp",EDGE,"E1298"),sQuery(id+"F0.wireOp",EDGE,"E1299"),sQuery(id+"F0.wireOp",EDGE,"E1300"),sQuery(id+"F0.wireOp",EDGE,"E1301"),sQuery(id+"F0.wireOp",EDGE,"E1302"),sQuery(id+"F0.wireOp",EDGE,"E1303"),sQuery(id+"F0.wireOp",EDGE,"E1304"),sQuery(id+"F0.wireOp",EDGE,"E1305"),sQuery(id+"F0.wireOp",EDGE,"E1306"),sQuery(id+"F0.wireOp",EDGE,"E1307"),sQuery(id+"F0.wireOp",EDGE,"E1308"),sQuery(id+"F0.wireOp",EDGE,"E1309"),sQuery(id+"F0.wireOp",EDGE,"E1310"),sQuery(id+"F0.wireOp",EDGE,"E1311"),sQuery(id+"F0.wireOp",EDGE,"E1312"),sQuery(id+"F0.wireOp",EDGE,"E1313"),sQuery(id+"F0.wireOp",EDGE,"E1314"),sQuery(id+"F0.wireOp",EDGE,"E1315"),sQuery(id+"F0.wireOp",EDGE,"E1316"),sQuery(id+"F0.wireOp",EDGE,"E1317"),sQuery(id+"F0.wireOp",EDGE,"E1318"),sQuery(id+"F0.wireOp",EDGE,"E1319"),sQuery(id+"F0.wireOp",EDGE,"E1320"),sQuery(id+"F0.wireOp",EDGE,"E1321"),sQuery(id+"F0.wireOp",EDGE,"E1322"),sQuery(id+"F0.wireOp",EDGE,"E1323"),sQuery(id+"F0.wireOp",EDGE,"E1324"),sQuery(id+"F0.wireOp",EDGE,"E1325"),sQuery(id+"F0.wireOp",EDGE,"E1326"),sQuery(id+"F0.wireOp",EDGE,"E1327"),sQuery(id+"F0.wireOp",EDGE,"E1328"),sQuery(id+"F0.wireOp",EDGE,"E1329"),sQuery(id+"F0.wireOp",EDGE,"E1330"),sQuery(id+"F0.wireOp",EDGE,"E1331"),sQuery(id+"F0.wireOp",EDGE,"E1332"),sQuery(id+"F0.wireOp",EDGE,"E1333"),sQuery(id+"F0.wireOp",EDGE,"E1334"),sQuery(id+"F0.wireOp",EDGE,"E1335"),sQuery(id+"F0.wireOp",EDGE,"E1336"),sQuery(id+"F0.wireOp",EDGE,"E1337"),sQuery(id+"F0.wireOp",EDGE,"E1338"),sQuery(id+"F0.wireOp",EDGE,"E1339"),sQuery(id+"F0.wireOp",EDGE,"E1340"),sQuery(id+"F0.wireOp",EDGE,"E1341"),sQuery(id+"F0.wireOp",EDGE,"E1342"),sQuery(id+"F0.wireOp",EDGE,"E1343"),sQuery(id+"F0.wireOp",EDGE,"E1344"),sQuery(id+"F0.wireOp",EDGE,"E1345"),sQuery(id+"F0.wireOp",EDGE,"E1346"),sQuery(id+"F0.wireOp",EDGE,"E1347"),sQuery(id+"F0.wireOp",EDGE,"E1348"),sQuery(id+"F0.wireOp",EDGE,"E1349"),sQuery(id+"F0.wireOp",EDGE,"E1350"),sQuery(id+"F0.wireOp",EDGE,"E1351"),sQuery(id+"F0.wireOp",EDGE,"E1352"),sQuery(id+"F0.wireOp",EDGE,"E1353"),sQuery(id+"F0.wireOp",EDGE,"E1354"),sQuery(id+"F0.wireOp",EDGE,"E1355"),sQuery(id+"F0.wireOp",EDGE,"E1356"),sQuery(id+"F0.wireOp",EDGE,"E1357"),sQuery(id+"F0.wireOp",EDGE,"E1358"),sQuery(id+"F0.wireOp",EDGE,"E1359"),sQuery(id+"F0.wireOp",EDGE,"E1360"),sQuery(id+"F0.wireOp",EDGE,"E1361"),sQuery(id+"F0.wireOp",EDGE,"E1362"),sQuery(id+"F0.wireOp",EDGE,"E1363"),sQuery(id+"F0.wireOp",EDGE,"E1364"),sQuery(id+"F0.wireOp",EDGE,"E1365"),sQuery(id+"F0.wireOp",EDGE,"E1366"),sQuery(id+"F0.wireOp",EDGE,"E1367"),sQuery(id+"F0.wireOp",EDGE,"E1368"),sQuery(id+"F0.wireOp",EDGE,"E1369"),sQuery(id+"F0.wireOp",EDGE,"E1370"),sQuery(id+"F0.wireOp",EDGE,"E1371"),sQuery(id+"F0.wireOp",EDGE,"E1372"),sQuery(id+"F0.wireOp",EDGE,"E1373"),sQuery(id+"F0.wireOp",EDGE,"E1374"),sQuery(id+"F0.wireOp",EDGE,"E1375"),sQuery(id+"F0.wireOp",EDGE,"E1376"),sQuery(id+"F0.wireOp",EDGE,"E1377"),sQuery(id+"F0.wireOp",EDGE,"E1378"),sQuery(id+"F0.wireOp",EDGE,"E1379"),sQuery(id+"F0.wireOp",EDGE,"E1380"),sQuery(id+"F0.wireOp",EDGE,"E1381"),sQuery(id+"F0.wireOp",EDGE,"E1382"),sQuery(id+"F0.wireOp",EDGE,"E1383"),sQuery(id+"F0.wireOp",EDGE,"E1384"),sQuery(id+"F0.wireOp",EDGE,"E1385"),sQuery(id+"F0.wireOp",EDGE,"E1386"),sQuery(id+"F0.wireOp",EDGE,"E1387"),sQuery(id+"F0.wireOp",EDGE,"E1388"),sQuery(id+"F0.wireOp",EDGE,"E1389"),sQuery(id+"F0.wireOp",EDGE,"E1390"),sQuery(id+"F0.wireOp",EDGE,"E1391"),sQuery(id+"F0.wireOp",EDGE,"E1392"),sQuery(id+"F0.wireOp",EDGE,"E1393"),sQuery(id+"F0.wireOp",EDGE,"E1394"),sQuery(id+"F0.wireOp",EDGE,"E1395"),sQuery(id+"F0.wireOp",EDGE,"E1396"),sQuery(id+"F0.wireOp",EDGE,"E1397"),sQuery(id+"F0.wireOp",EDGE,"E1398"),sQuery(id+"F0.wireOp",EDGE,"E1399"),sQuery(id+"F0.wireOp",EDGE,"E1400"),sQuery(id+"F0.wireOp",EDGE,"E1401"),sQuery(id+"F0.wireOp",EDGE,"E1402"),sQuery(id+"F0.wireOp",EDGE,"E1403"),sQuery(id+"F0.wireOp",EDGE,"E1404"),sQuery(id+"F0.wireOp",EDGE,"E1405"),sQuery(id+"F0.wireOp",EDGE,"E1406"),sQuery(id+"F0.wireOp",EDGE,"E1407"),sQuery(id+"F0.wireOp",EDGE,"E1408"),sQuery(id+"F0.wireOp",EDGE,"E1409"),sQuery(id+"F0.wireOp",EDGE,"E1410"),sQuery(id+"F0.wireOp",EDGE,"E1411"),sQuery(id+"F0.wireOp",EDGE,"E1412"),sQuery(id+"F0.wireOp",EDGE,"E1413"),sQuery(id+"F0.wireOp",EDGE,"E1414"),sQuery(id+"F0.wireOp",EDGE,"E1415"),sQuery(id+"F0.wireOp",EDGE,"E1416"),sQuery(id+"F0.wireOp",EDGE,"E1417"),sQuery(id+"F0.wireOp",EDGE,"E1418"),sQuery(id+"F0.wireOp",EDGE,"E1419"),sQuery(id+"F0.wireOp",EDGE,"E1420"),sQuery(id+"F0.wireOp",EDGE,"E1421"),sQuery(id+"F0.wireOp",EDGE,"E1422"),sQuery(id+"F0.wireOp",EDGE,"E1423"),sQuery(id+"F0.wireOp",EDGE,"E1424"),sQuery(id+"F0.wireOp",EDGE,"E1425"),sQuery(id+"F0.wireOp",EDGE,"E1426"),sQuery(id+"F0.wireOp",EDGE,"E1427"),sQuery(id+"F0.wireOp",EDGE,"E1428"),sQuery(id+"F0.wireOp",EDGE,"E1429"),sQuery(id+"F0.wireOp",EDGE,"E1430"),sQuery(id+"F0.wireOp",EDGE,"E1431"),sQuery(id+"F0.wireOp",EDGE,"E1432"),sQuery(id+"F0.wireOp",EDGE,"E1433"),sQuery(id+"F0.wireOp",EDGE,"E1434"),sQuery(id+"F0.wireOp",EDGE,"E1435"),sQuery(id+"F0.wireOp",EDGE,"E1436"),sQuery(id+"F0.wireOp",EDGE,"E1437"),sQuery(id+"F0.wireOp",EDGE,"E1438"),sQuery(id+"F0.wireOp",EDGE,"E1439"),sQuery(id+"F0.wireOp",EDGE,"E1440"),sQuery(id+"F0.wireOp",EDGE,"E1441"),sQuery(id+"F0.wireOp",EDGE,"E1442"),sQuery(id+"F0.wireOp",EDGE,"E1443"),sQuery(id+"F0.wireOp",EDGE,"E1444"),sQuery(id+"F0.wireOp",EDGE,"E1445"),sQuery(id+"F0.wireOp",EDGE,"E1446"),sQuery(id+"F0.wireOp",EDGE,"E1447"),sQuery(id+"F0.wireOp",EDGE,"E1448"),sQuery(id+"F0.wireOp",EDGE,"E1449"),sQuery(id+"F0.wireOp",EDGE,"E1450"),sQuery(id+"F0.wireOp",EDGE,"E1451"),sQuery(id+"F0.wireOp",EDGE,"E1452"),sQuery(id+"F0.wireOp",EDGE,"E1453"),sQuery(id+"F0.wireOp",EDGE,"E1454"),sQuery(id+"F0.wireOp",EDGE,"E1455"),sQuery(id+"F0.wireOp",EDGE,"E1456"),sQuery(id+"F0.wireOp",EDGE,"E1457"),sQuery(id+"F0.wireOp",EDGE,"E1458"),sQuery(id+"F0.wireOp",EDGE,"E1459"),sQuery(id+"F0.wireOp",EDGE,"E1460"),sQuery(id+"F0.wireOp",EDGE,"E1461"),sQuery(id+"F0.wireOp",EDGE,"E1462"),sQuery(id+"F0.wireOp",EDGE,"E1463"),sQuery(id+"F0.wireOp",EDGE,"E1464"),sQuery(id+"F0.wireOp",EDGE,"E1465"),sQuery(id+"F0.wireOp",EDGE,"E1466"),sQuery(id+"F0.wireOp",EDGE,"E1467"),sQuery(id+"F0.wireOp",EDGE,"E1468"),sQuery(id+"F0.wireOp",EDGE,"E1469"),sQuery(id+"F0.wireOp",EDGE,"E1470"),sQuery(id+"F0.wireOp",EDGE,"E1471"),sQuery(id+"F0.wireOp",EDGE,"E1472"),sQuery(id+"F0.wireOp",EDGE,"E1473"),sQuery(id+"F0.wireOp",EDGE,"E1474"),sQuery(id+"F0.wireOp",EDGE,"E1475"),sQuery(id+"F0.wireOp",EDGE,"E1476"),sQuery(id+"F0.wireOp",EDGE,"E1477"),sQuery(id+"F0.wireOp",EDGE,"E1478"),sQuery(id+"F0.wireOp",EDGE,"E1479"),sQuery(id+"F0.wireOp",EDGE,"E1480"),sQuery(id+"F0.wireOp",EDGE,"E1481"),sQuery(id+"F0.wireOp",EDGE,"E1482"),sQuery(id+"F0.wireOp",EDGE,"E1483"),sQuery(id+"F0.wireOp",EDGE,"E1484"),sQuery(id+"F0.wireOp",EDGE,"E1485"),sQuery(id+"F0.wireOp",EDGE,"E1486"),sQuery(id+"F0.wireOp",EDGE,"E1487"),sQuery(id+"F0.wireOp",EDGE,"E1488"),sQuery(id+"F0.wireOp",EDGE,"E1489"),sQuery(id+"F0.wireOp",EDGE,"E1490"),sQuery(id+"F0.wireOp",EDGE,"E1491"),sQuery(id+"F0.wireOp",EDGE,"E1492"),sQuery(id+"F0.wireOp",EDGE,"E1493"),sQuery(id+"F0.wireOp",EDGE,"E1494"),sQuery(id+"F0.wireOp",EDGE,"E1495"),sQuery(id+"F0.wireOp",EDGE,"E1496"),sQuery(id+"F0.wireOp",EDGE,"E1497"),sQuery(id+"F0.wireOp",EDGE,"E1498"),sQuery(id+"F0.wireOp",EDGE,"E1499"),sQuery(id+"F0.wireOp",EDGE,"E1500"),sQuery(id+"F0.wireOp",EDGE,"E1501"),sQuery(id+"F0.wireOp",EDGE,"E1502"),sQuery(id+"F0.wireOp",EDGE,"E1503"),sQuery(id+"F0.wireOp",EDGE,"E1504"),sQuery(id+"F0.wireOp",EDGE,"E1505"),sQuery(id+"F0.wireOp",EDGE,"E1506"),sQuery(id+"F0.wireOp",EDGE,"E1507"),sQuery(id+"F0.wireOp",EDGE,"E1508"),sQuery(id+"F0.wireOp",EDGE,"E1509"),sQuery(id+"F0.wireOp",EDGE,"E1510"),sQuery(id+"F0.wireOp",EDGE,"E1511"),sQuery(id+"F0.wireOp",EDGE,"E1512"),sQuery(id+"F0.wireOp",EDGE,"E1513"),sQuery(id+"F0.wireOp",EDGE,"E1514"),sQuery(id+"F0.wireOp",EDGE,"E1515"),sQuery(id+"F0.wireOp",EDGE,"E1516"),sQuery(id+"F0.wireOp",EDGE,"E1517"),sQuery(id+"F0.wireOp",EDGE,"E1518"),sQuery(id+"F0.wireOp",EDGE,"E1519"),sQuery(id+"F0.wireOp",EDGE,"E1520"),sQuery(id+"F0.wireOp",EDGE,"E1521"),sQuery(id+"F0.wireOp",EDGE,"E1522"),sQuery(id+"F0.wireOp",EDGE,"E1523"),sQuery(id+"F0.wireOp",EDGE,"E1524"),sQuery(id+"F0.wireOp",EDGE,"E1525"),sQuery(id+"F0.wireOp",EDGE,"E1526"),sQuery(id+"F0.wireOp",EDGE,"E1527"),sQuery(id+"F0.wireOp",EDGE,"E1528"),sQuery(id+"F0.wireOp",EDGE,"E1529"),sQuery(id+"F0.wireOp",EDGE,"E1530"),sQuery(id+"F0.wireOp",EDGE,"E1531"),sQuery(id+"F0.wireOp",EDGE,"E1532"),sQuery(id+"F0.wireOp",EDGE,"E1533"),sQuery(id+"F0.wireOp",EDGE,"E1534"),sQuery(id+"F0.wireOp",EDGE,"E1535"),sQuery(id+"F0.wireOp",EDGE,"E1536"),sQuery(id+"F0.wireOp",EDGE,"E1537"),sQuery(id+"F0.wireOp",EDGE,"E1538"),sQuery(id+"F0.wireOp",EDGE,"E1539"),sQuery(id+"F0.wireOp",EDGE,"E1540"),sQuery(id+"F0.wireOp",EDGE,"E1541"),sQuery(id+"F0.wireOp",EDGE,"E1542"),sQuery(id+"F0.wireOp",EDGE,"E1543"),sQuery(id+"F0.wireOp",EDGE,"E1544"),sQuery(id+"F0.wireOp",EDGE,"E1545"),sQuery(id+"F0.wireOp",EDGE,"E1546"),sQuery(id+"F0.wireOp",EDGE,"E1547"),sQuery(id+"F0.wireOp",EDGE,"E1548"),sQuery(id+"F0.wireOp",EDGE,"E1549"),sQuery(id+"F0.wireOp",EDGE,"E1550"),sQuery(id+"F0.wireOp",EDGE,"E1551"),sQuery(id+"F0.wireOp",EDGE,"E1552"),sQuery(id+"F0.wireOp",EDGE,"E1553"),sQuery(id+"F0.wireOp",EDGE,"E1554"),sQuery(id+"F0.wireOp",EDGE,"E1555"),sQuery(id+"F0.wireOp",EDGE,"E1556"),sQuery(id+"F0.wireOp",EDGE,"E1557"),sQuery(id+"F0.wireOp",EDGE,"E1558"),sQuery(id+"F0.wireOp",EDGE,"E1559"),sQuery(id+"F0.wireOp",EDGE,"E1560"),sQuery(id+"F0.wireOp",EDGE,"E1561"),sQuery(id+"F0.wireOp",EDGE,"E1562"),sQuery(id+"F0.wireOp",EDGE,"E1563"),sQuery(id+"F0.wireOp",EDGE,"E1564"),sQuery(id+"F0.wireOp",EDGE,"E1565"),sQuery(id+"F0.wireOp",EDGE,"E1566"),sQuery(id+"F0.wireOp",EDGE,"E1567"),sQuery(id+"F0.wireOp",EDGE,"E1568"),sQuery(id+"F0.wireOp",EDGE,"E1569"),sQuery(id+"F0.wireOp",EDGE,"E1570"),sQuery(id+"F0.wireOp",EDGE,"E1571"),sQuery(id+"F0.wireOp",EDGE,"E1572"),sQuery(id+"F0.wireOp",EDGE,"E1573"),sQuery(id+"F0.wireOp",EDGE,"E1574"),sQuery(id+"F0.wireOp",EDGE,"E1575"),sQuery(id+"F0.wireOp",EDGE,"E1576"),sQuery(id+"F0.wireOp",EDGE,"E1577"),sQuery(id+"F0.wireOp",EDGE,"E1578"),sQuery(id+"F0.wireOp",EDGE,"E1579"),sQuery(id+"F0.wireOp",EDGE,"E1580"),sQuery(id+"F0.wireOp",EDGE,"E1581"),sQuery(id+"F0.wireOp",EDGE,"E1582"),sQuery(id+"F0.wireOp",EDGE,"E1583"),sQuery(id+"F0.wireOp",EDGE,"E1584"),sQuery(id+"F0.wireOp",EDGE,"E1585"),sQuery(id+"F0.wireOp",EDGE,"E1586"),sQuery(id+"F0.wireOp",EDGE,"E1587"),sQuery(id+"F0.wireOp",EDGE,"E1588"),sQuery(id+"F0.wireOp",EDGE,"E1589"),sQuery(id+"F0.wireOp",EDGE,"E1590"),sQuery(id+"F0.wireOp",EDGE,"E1591"),sQuery(id+"F0.wireOp",EDGE,"E1592"),sQuery(id+"F0.wireOp",EDGE,"E1593"),sQuery(id+"F0.wireOp",EDGE,"E1594"),sQuery(id+"F0.wireOp",EDGE,"E1595"),sQuery(id+"F0.wireOp",EDGE,"E1596"),sQuery(id+"F0.wireOp",EDGE,"E1597"),sQuery(id+"F0.wireOp",EDGE,"E1598"),sQuery(id+"F0.wireOp",EDGE,"E1599"),sQuery(id+"F0.wireOp",EDGE,"E1600"),sQuery(id+"F0.wireOp",EDGE,"E1601"),sQuery(id+"F0.wireOp",EDGE,"E1602"),sQuery(id+"F0.wireOp",EDGE,"E1603"),sQuery(id+"F0.wireOp",EDGE,"E1604"),sQuery(id+"F0.wireOp",EDGE,"E1605"),sQuery(id+"F0.wireOp",EDGE,"E1606"),sQuery(id+"F0.wireOp",EDGE,"E1607"),sQuery(id+"F0.wireOp",EDGE,"E1608"),sQuery(id+"F0.wireOp",EDGE,"E1609"),sQuery(id+"F0.wireOp",EDGE,"E1610"),sQuery(id+"F0.wireOp",EDGE,"E1611"),sQuery(id+"F0.wireOp",EDGE,"E1612"),sQuery(id+"F0.wireOp",EDGE,"E1613"),sQuery(id+"F0.wireOp",EDGE,"E1614"),sQuery(id+"F0.wireOp",EDGE,"E1615"),sQuery(id+"F0.wireOp",EDGE,"E1616"),sQuery(id+"F0.wireOp",EDGE,"E1617"),sQuery(id+"F0.wireOp",EDGE,"E1618"),sQuery(id+"F0.wireOp",EDGE,"E1619"),sQuery(id+"F0.wireOp",EDGE,"E1620"),sQuery(id+"F0.wireOp",EDGE,"E1621"),sQuery(id+"F0.wireOp",EDGE,"E1622"),sQuery(id+"F0.wireOp",EDGE,"E1623"),sQuery(id+"F0.wireOp",EDGE,"E1624"),sQuery(id+"F0.wireOp",EDGE,"E1625"),sQuery(id+"F0.wireOp",EDGE,"E1626"),sQuery(id+"F0.wireOp",EDGE,"E1627"),sQuery(id+"F0.wireOp",EDGE,"E1628"),sQuery(id+"F0.wireOp",EDGE,"E1629"),sQuery(id+"F0.wireOp",EDGE,"E1630"),sQuery(id+"F0.wireOp",EDGE,"E1631"),sQuery(id+"F0.wireOp",EDGE,"E1632"),sQuery(id+"F0.wireOp",EDGE,"E1633"),sQuery(id+"F0.wireOp",EDGE,"E1634"),sQuery(id+"F0.wireOp",EDGE,"E1635"),sQuery(id+"F0.wireOp",EDGE,"E1636"),sQuery(id+"F0.wireOp",EDGE,"E1637"),sQuery(id+"F0.wireOp",EDGE,"E1638"),sQuery(id+"F0.wireOp",EDGE,"E1639"),sQuery(id+"F0.wireOp",EDGE,"E1640"),sQuery(id+"F0.wireOp",EDGE,"E1641"),sQuery(id+"F0.wireOp",EDGE,"E1642"),sQuery(id+"F0.wireOp",EDGE,"E1643"),sQuery(id+"F0.wireOp",EDGE,"E1644"),sQuery(id+"F0.wireOp",EDGE,"E1645"),sQuery(id+"F0.wireOp",EDGE,"E1646"),sQuery(id+"F0.wireOp",EDGE,"E1647"),sQuery(id+"F0.wireOp",EDGE,"E1648"),sQuery(id+"F0.wireOp",EDGE,"E1649"),sQuery(id+"F0.wireOp",EDGE,"E1650"),sQuery(id+"F0.wireOp",EDGE,"E1651"),sQuery(id+"F0.wireOp",EDGE,"E1652"),sQuery(id+"F0.wireOp",EDGE,"E1653"),sQuery(id+"F0.wireOp",EDGE,"E1654"),sQuery(id+"F0.wireOp",EDGE,"E1655"),sQuery(id+"F0.wireOp",EDGE,"E1656"),sQuery(id+"F0.wireOp",EDGE,"E1657"),sQuery(id+"F0.wireOp",EDGE,"E1658"),sQuery(id+"F0.wireOp",EDGE,"E1659"),sQuery(id+"F0.wireOp",EDGE,"E1660"),sQuery(id+"F0.wireOp",EDGE,"E1661"),sQuery(id+"F0.wireOp",EDGE,"E1662"),sQuery(id+"F0.wireOp",EDGE,"E1663"),sQuery(id+"F0.wireOp",EDGE,"E1664"),sQuery(id+"F0.wireOp",EDGE,"E1665"),sQuery(id+"F0.wireOp",EDGE,"E1666"),sQuery(id+"F0.wireOp",EDGE,"E1667"),sQuery(id+"F0.wireOp",EDGE,"E1668"),sQuery(id+"F0.wireOp",EDGE,"E1669"),sQuery(id+"F0.wireOp",EDGE,"E1670"),sQuery(id+"F0.wireOp",EDGE,"E1671"),sQuery(id+"F0.wireOp",EDGE,"E1672"),sQuery(id+"F0.wireOp",EDGE,"E1673"),sQuery(id+"F0.wireOp",EDGE,"E1674"),sQuery(id+"F0.wireOp",EDGE,"E1675"),sQuery(id+"F0.wireOp",EDGE,"E1676"),sQuery(id+"F0.wireOp",EDGE,"E1677"),sQuery(id+"F0.wireOp",EDGE,"E1678"),sQuery(id+"F0.wireOp",EDGE,"E1679"),sQuery(id+"F0.wireOp",EDGE,"E1680"),sQuery(id+"F0.wireOp",EDGE,"E1681"),sQuery(id+"F0.wireOp",EDGE,"E1682"),sQuery(id+"F0.wireOp",EDGE,"E1683"),sQuery(id+"F0.wireOp",EDGE,"E1684"),sQuery(id+"F0.wireOp",EDGE,"E1685"),sQuery(id+"F0.wireOp",EDGE,"E1686"),sQuery(id+"F0.wireOp",EDGE,"E1687"),sQuery(id+"F0.wireOp",EDGE,"E1688"),sQuery(id+"F0.wireOp",EDGE,"E1689"),sQuery(id+"F0.wireOp",EDGE,"E1690"),sQuery(id+"F0.wireOp",EDGE,"E1691"),sQuery(id+"F0.wireOp",EDGE,"E1692"),sQuery(id+"F0.wireOp",EDGE,"E1693"),sQuery(id+"F0.wireOp",EDGE,"E1694"),sQuery(id+"F0.wireOp",EDGE,"E1695"),sQuery(id+"F0.wireOp",EDGE,"E1696"),sQuery(id+"F0.wireOp",EDGE,"E1697"),sQuery(id+"F0.wireOp",EDGE,"E1698"),sQuery(id+"F0.wireOp",EDGE,"E1699"),sQuery(id+"F0.wireOp",EDGE,"E1700"),sQuery(id+"F0.wireOp",EDGE,"E1701"),sQuery(id+"F0.wireOp",EDGE,"E1702"),sQuery(id+"F0.wireOp",EDGE,"E1703"),sQuery(id+"F0.wireOp",EDGE,"E1704"),sQuery(id+"F0.wireOp",EDGE,"E1705"),sQuery(id+"F0.wireOp",EDGE,"E1706"),sQuery(id+"F0.wireOp",EDGE,"E1707"),sQuery(id+"F0.wireOp",EDGE,"E1708"),sQuery(id+"F0.wireOp",EDGE,"E1709"),sQuery(id+"F0.wireOp",EDGE,"E1710"),sQuery(id+"F0.wireOp",EDGE,"E1711"),sQuery(id+"F0.wireOp",EDGE,"E1712"),sQuery(id+"F0.wireOp",EDGE,"E1713"),sQuery(id+"F0.wireOp",EDGE,"E1714"),sQuery(id+"F0.wireOp",EDGE,"E1715"),sQuery(id+"F0.wireOp",EDGE,"E1716"),sQuery(id+"F0.wireOp",EDGE,"E1717"),sQuery(id+"F0.wireOp",EDGE,"E1718"),sQuery(id+"F0.wireOp",EDGE,"E1719"),sQuery(id+"F0.wireOp",EDGE,"E1720"),sQuery(id+"F0.wireOp",EDGE,"E1721"),sQuery(id+"F0.wireOp",EDGE,"E1722"),sQuery(id+"F0.wireOp",EDGE,"E1723"),sQuery(id+"F0.wireOp",EDGE,"E1724"),sQuery(id+"F0.wireOp",EDGE,"E1725"),sQuery(id+"F0.wireOp",EDGE,"E1726"),sQuery(id+"F0.wireOp",EDGE,"E1727"),sQuery(id+"F0.wireOp",EDGE,"E1728"),sQuery(id+"F0.wireOp",EDGE,"E1729"),sQuery(id+"F0.wireOp",EDGE,"E1730"),sQuery(id+"F0.wireOp",EDGE,"E1731"),sQuery(id+"F0.wireOp",EDGE,"E1732"),sQuery(id+"F0.wireOp",EDGE,"E1733"),sQuery(id+"F0.wireOp",EDGE,"E1734"),sQuery(id+"F0.wireOp",EDGE,"E1735"),sQuery(id+"F0.wireOp",EDGE,"E1736"),sQuery(id+"F0.wireOp",EDGE,"E1737"),sQuery(id+"F0.wireOp",EDGE,"E1738"),sQuery(id+"F0.wireOp",EDGE,"E1739"),sQuery(id+"F0.wireOp",EDGE,"E1740"),sQuery(id+"F0.wireOp",EDGE,"E1741"),sQuery(id+"F0.wireOp",EDGE,"E1742"),sQuery(id+"F0.wireOp",EDGE,"E1743"),sQuery(id+"F0.wireOp",EDGE,"E1744"),sQuery(id+"F0.wireOp",EDGE,"E1745"),sQuery(id+"F0.wireOp",EDGE,"E1746"),sQuery(id+"F0.wireOp",EDGE,"E1747"),sQuery(id+"F0.wireOp",EDGE,"E1748"),sQuery(id+"F0.wireOp",EDGE,"E1749"),sQuery(id+"F0.wireOp",EDGE,"E1750"),sQuery(id+"F0.wireOp",EDGE,"E1751"),sQuery(id+"F0.wireOp",EDGE,"E1752"),sQuery(id+"F0.wireOp",EDGE,"E1753"),sQuery(id+"F0.wireOp",EDGE,"E1754"),sQuery(id+"F0.wireOp",EDGE,"E1755"),sQuery(id+"F0.wireOp",EDGE,"E1756"),sQuery(id+"F0.wireOp",EDGE,"E1757"),sQuery(id+"F0.wireOp",EDGE,"E1758"),sQuery(id+"F0.wireOp",EDGE,"E1759"),sQuery(id+"F0.wireOp",EDGE,"E1760"),sQuery(id+"F0.wireOp",EDGE,"E1761"),sQuery(id+"F0.wireOp",EDGE,"E1762"),sQuery(id+"F0.wireOp",EDGE,"E1763"),sQuery(id+"F0.wireOp",EDGE,"E1764"),sQuery(id+"F0.wireOp",EDGE,"E1765"),sQuery(id+"F0.wireOp",EDGE,"E1766"),sQuery(id+"F0.wireOp",EDGE,"E1767"),sQuery(id+"F0.wireOp",EDGE,"E1768"),sQuery(id+"F0.wireOp",EDGE,"E1769"),sQuery(id+"F0.wireOp",EDGE,"E1770"),sQuery(id+"F0.wireOp",EDGE,"E1771"),sQuery(id+"F0.wireOp",EDGE,"E1772"),sQuery(id+"F0.wireOp",EDGE,"E1773"),sQuery(id+"F0.wireOp",EDGE,"E1774"),sQuery(id+"F0.wireOp",EDGE,"E1775"),sQuery(id+"F0.wireOp",EDGE,"E1776"),sQuery(id+"F0.wireOp",EDGE,"E1777"),sQuery(id+"F0.wireOp",EDGE,"E1778"),sQuery(id+"F0.wireOp",EDGE,"E1779"),sQuery(id+"F0.wireOp",EDGE,"E1780"),sQuery(id+"F0.wireOp",EDGE,"E1781"),sQuery(id+"F0.wireOp",EDGE,"E1782"),sQuery(id+"F0.wireOp",EDGE,"E1783"),sQuery(id+"F0.wireOp",EDGE,"E1784"),sQuery(id+"F0.wireOp",EDGE,"E1785"),sQuery(id+"F0.wireOp",EDGE,"E1786"),sQuery(id+"F0.wireOp",EDGE,"E1787"),sQuery(id+"F0.wireOp",EDGE,"E1788"),sQuery(id+"F0.wireOp",EDGE,"E1789"),sQuery(id+"F0.wireOp",EDGE,"E1790"),sQuery(id+"F0.wireOp",EDGE,"E1791"),sQuery(id+"F0.wireOp",EDGE,"E1792"),sQuery(id+"F0.wireOp",EDGE,"E1793"),sQuery(id+"F0.wireOp",EDGE,"E1794"),sQuery(id+"F0.wireOp",EDGE,"E1795"),sQuery(id+"F0.wireOp",EDGE,"E1796"),sQuery(id+"F0.wireOp",EDGE,"E1797"),sQuery(id+"F0.wireOp",EDGE,"E1798"),sQuery(id+"F0.wireOp",EDGE,"E1799"),sQuery(id+"F0.wireOp",EDGE,"E1800"),sQuery(id+"F0.wireOp",EDGE,"E1801"),sQuery(id+"F0.wireOp",EDGE,"E1802"),sQuery(id+"F0.wireOp",EDGE,"E1803"),sQuery(id+"F0.wireOp",EDGE,"E1804"),sQuery(id+"F0.wireOp",EDGE,"E1805"),sQuery(id+"F0.wireOp",EDGE,"E1806"),sQuery(id+"F0.wireOp",EDGE,"E1807"),sQuery(id+"F0.wireOp",EDGE,"E1808"),sQuery(id+"F0.wireOp",EDGE,"E1809"),sQuery(id+"F0.wireOp",EDGE,"E1810"),sQuery(id+"F0.wireOp",EDGE,"E1811"),sQuery(id+"F0.wireOp",EDGE,"E1812"),sQuery(id+"F0.wireOp",EDGE,"E1813"),sQuery(id+"F0.wireOp",EDGE,"E1814"),sQuery(id+"F0.wireOp",EDGE,"E1815"),sQuery(id+"F0.wireOp",EDGE,"E1816"),sQuery(id+"F0.wireOp",EDGE,"E1817"),sQuery(id+"F0.wireOp",EDGE,"E1818"),sQuery(id+"F0.wireOp",EDGE,"E1819"),sQuery(id+"F0.wireOp",EDGE,"E1820"),sQuery(id+"F0.wireOp",EDGE,"E1821"),sQuery(id+"F0.wireOp",EDGE,"E1822"),sQuery(id+"F0.wireOp",EDGE,"E1823"),sQuery(id+"F0.wireOp",EDGE,"E1824"),sQuery(id+"F0.wireOp",EDGE,"E1825"),sQuery(id+"F0.wireOp",EDGE,"E1826"),sQuery(id+"F0.wireOp",EDGE,"E1827"),sQuery(id+"F0.wireOp",EDGE,"E1828"),sQuery(id+"F0.wireOp",EDGE,"E1829"),sQuery(id+"F0.wireOp",EDGE,"E1830"),sQuery(id+"F0.wireOp",EDGE,"E1831"),sQuery(id+"F0.wireOp",EDGE,"E1832"),sQuery(id+"F0.wireOp",EDGE,"E1833"),sQuery(id+"F0.wireOp",EDGE,"E1834"),sQuery(id+"F0.wireOp",EDGE,"E1835"),sQuery(id+"F0.wireOp",EDGE,"E1836"),sQuery(id+"F0.wireOp",EDGE,"E1837"),sQuery(id+"F0.wireOp",EDGE,"E1838"),sQuery(id+"F0.wireOp",EDGE,"E1839"),sQuery(id+"F0.wireOp",EDGE,"E1840"),sQuery(id+"F0.wireOp",EDGE,"E1841"),sQuery(id+"F0.wireOp",EDGE,"E1842"),sQuery(id+"F0.wireOp",EDGE,"E1843"),sQuery(id+"F0.wireOp",EDGE,"E1844"),sQuery(id+"F0.wireOp",EDGE,"E1845"),sQuery(id+"F0.wireOp",EDGE,"E1846"),sQuery(id+"F0.wireOp",EDGE,"E1847"),sQuery(id+"F0.wireOp",EDGE,"E1848"),sQuery(id+"F0.wireOp",EDGE,"E1849"),sQuery(id+"F0.wireOp",EDGE,"E1850"),sQuery(id+"F0.wireOp",EDGE,"E1851"),sQuery(id+"F0.wireOp",EDGE,"E1852"),sQuery(id+"F0.wireOp",EDGE,"E1853"),sQuery(id+"F0.wireOp",EDGE,"E1854"),sQuery(id+"F0.wireOp",EDGE,"E1855"),sQuery(id+"F0.wireOp",EDGE,"E1856"),sQuery(id+"F0.wireOp",EDGE,"E1857"),sQuery(id+"F0.wireOp",EDGE,"E1858"),sQuery(id+"F0.wireOp",EDGE,"E1859"),sQuery(id+"F0.wireOp",EDGE,"E1860"),sQuery(id+"F0.wireOp",EDGE,"E1861"),sQuery(id+"F0.wireOp",EDGE,"E1862"),sQuery(id+"F0.wireOp",EDGE,"E1863"),sQuery(id+"F0.wireOp",EDGE,"E1864"),sQuery(id+"F0.wireOp",EDGE,"E1865"),sQuery(id+"F0.wireOp",EDGE,"E1866"),sQuery(id+"F0.wireOp",EDGE,"E1867"),sQuery(id+"F0.wireOp",EDGE,"E1868"),sQuery(id+"F0.wireOp",EDGE,"E1869"),sQuery(id+"F0.wireOp",EDGE,"E1870"),sQuery(id+"F0.wireOp",EDGE,"E1871"),sQuery(id+"F0.wireOp",EDGE,"E1872"),sQuery(id+"F0.wireOp",EDGE,"E1873"),sQuery(id+"F0.wireOp",EDGE,"E1874"),sQuery(id+"F0.wireOp",EDGE,"E1875"),sQuery(id+"F0.wireOp",EDGE,"E1876"),sQuery(id+"F0.wireOp",EDGE,"E1877"),sQuery(id+"F0.wireOp",EDGE,"E1878"),sQuery(id+"F0.wireOp",EDGE,"E1879"),sQuery(id+"F0.wireOp",EDGE,"E1880"),sQuery(id+"F0.wireOp",EDGE,"E1881"),sQuery(id+"F0.wireOp",EDGE,"E1882"),sQuery(id+"F0.wireOp",EDGE,"E1883"),sQuery(id+"F0.wireOp",EDGE,"E1884"),sQuery(id+"F0.wireOp",EDGE,"E1885"),sQuery(id+"F0.wireOp",EDGE,"E1886"),sQuery(id+"F0.wireOp",EDGE,"E1887"),sQuery(id+"F0.wireOp",EDGE,"E1888"),sQuery(id+"F0.wireOp",EDGE,"E1889"),sQuery(id+"F0.wireOp",EDGE,"E1890"),sQuery(id+"F0.wireOp",EDGE,"E1891"),sQuery(id+"F0.wireOp",EDGE,"E1892"),sQuery(id+"F0.wireOp",EDGE,"E1893"),sQuery(id+"F0.wireOp",EDGE,"E1894"),sQuery(id+"F0.wireOp",EDGE,"E1895"),sQuery(id+"F0.wireOp",EDGE,"E1896"),sQuery(id+"F0.wireOp",EDGE,"E1897"),sQuery(id+"F0.wireOp",EDGE,"E1898"),sQuery(id+"F0.wireOp",EDGE,"E1899"),sQuery(id+"F0.wireOp",EDGE,"E1900"),sQuery(id+"F0.wireOp",EDGE,"E1901"),sQuery(id+"F0.wireOp",EDGE,"E1902"),sQuery(id+"F0.wireOp",EDGE,"E1903"),sQuery(id+"F0.wireOp",EDGE,"E1904"),sQuery(id+"F0.wireOp",EDGE,"E1905"),sQuery(id+"F0.wireOp",EDGE,"E1906"),sQuery(id+"F0.wireOp",EDGE,"E1907"),sQuery(id+"F0.wireOp",EDGE,"E1908"),sQuery(id+"F0.wireOp",EDGE,"E1909"),sQuery(id+"F0.wireOp",EDGE,"E1910"),sQuery(id+"F0.wireOp",EDGE,"E1911"),sQuery(id+"F0.wireOp",EDGE,"E1912"),sQuery(id+"F0.wireOp",EDGE,"E1913"),sQuery(id+"F0.wireOp",EDGE,"E1914"),sQuery(id+"F0.wireOp",EDGE,"E1915"),sQuery(id+"F0.wireOp",EDGE,"E1916"),sQuery(id+"F0.wireOp",EDGE,"E1917"),sQuery(id+"F0.wireOp",EDGE,"E1918"),sQuery(id+"F0.wireOp",EDGE,"E1919"),sQuery(id+"F0.wireOp",EDGE,"E1920"),sQuery(id+"F0.wireOp",EDGE,"E1921"),sQuery(id+"F0.wireOp",EDGE,"E1922"),sQuery(id+"F0.wireOp",EDGE,"E1923"),sQuery(id+"F0.wireOp",EDGE,"E1924"),sQuery(id+"F0.wireOp",EDGE,"E1925"),sQuery(id+"F0.wireOp",EDGE,"E1926"),sQuery(id+"F0.wireOp",EDGE,"E1927"),sQuery(id+"F0.wireOp",EDGE,"E1928"),sQuery(id+"F0.wireOp",EDGE,"E1929"),sQuery(id+"F0.wireOp",EDGE,"E1930"),sQuery(id+"F0.wireOp",EDGE,"E1931"),sQuery(id+"F0.wireOp",EDGE,"E1932"),sQuery(id+"F0.wireOp",EDGE,"E1933"),sQuery(id+"F0.wireOp",EDGE,"E1934"),sQuery(id+"F0.wireOp",EDGE,"E1935"),sQuery(id+"F0.wireOp",EDGE,"E1936"),sQuery(id+"F0.wireOp",EDGE,"E1937"),sQuery(id+"F0.wireOp",EDGE,"E1938"),sQuery(id+"F0.wireOp",EDGE,"E1939"),sQuery(id+"F0.wireOp",EDGE,"E1940"),sQuery(id+"F0.wireOp",EDGE,"E1941"),sQuery(id+"F0.wireOp",EDGE,"E1942"),sQuery(id+"F0.wireOp",EDGE,"E1943"),sQuery(id+"F0.wireOp",EDGE,"E1944"),sQuery(id+"F0.wireOp",EDGE,"E1945"),sQuery(id+"F0.wireOp",EDGE,"E1946"),sQuery(id+"F0.wireOp",EDGE,"E1947"),sQuery(id+"F0.wireOp",EDGE,"E1948"),sQuery(id+"F0.wireOp",EDGE,"E1949"),sQuery(id+"F0.wireOp",EDGE,"E1950"),sQuery(id+"F0.wireOp",EDGE,"E1951"),sQuery(id+"F0.wireOp",EDGE,"E1952"),sQuery(id+"F0.wireOp",EDGE,"E1953")])]});
            var Q2;
            Q2=qCreatedBy(makeId("Origin.pointOp"),VERTEX);
            transform(context, id + "F2", {"entities" : qUnion([Q0, Q1]), "transformType" : TransformType.SCALE_UNIFORMLY, "scale" : 0.3, "scalePoint" : qUnion([Q2]), "makeCopy" : false});
        }
        {
            var Q0;
            Q0=qCreatedBy(makeId("Top.planeOp"),FACE);
            var sketch = newSketch(context, id + "F3", { "sketchPlane" : qUnion([Q0])});
            skCircle(sketch, "E1954", {"center": v(5.24, -9.4) * mm, "radius": 2 * mm});
            skPoint(sketch, "E1955.0", {"position": v(15.85, -18.3) * mm});
            skPoint(sketch, "E1956.0", {"position": v(-5.36, -0.5) * mm});
            skPoint(sketch, "E1957.0", {"position": v(0.85, -22.54) * mm});
            skCircle(sketch, "E1958", {"center": v(5.24, -9.4) * mm, "radius": 13.85 * mm});
            skPoint(sketch, "E1959.0", {"position": v(-0.43, 11.77) * mm});
            skPoint(sketch, "E1960.0", {"position": v(-11, 23.14) * mm});
            skPoint(sketch, "E1961.0", {"position": v(-16.7, 7.55) * mm});
            skCircle(sketch, "E1962", {"center": v(-9.64, 13.8) * mm, "radius": 9.44 * mm});
            skCircle(sketch, "E1963", {"center": v(-9.64, 13.8) * mm, "radius": 1.5 * mm});
            skSolve(sketch);
        }
        {
            var Q0;
            Q0=makeQuery(id+"F3.imprint","IMPRINT",FACE,{"disambiguationData":[TD([[makeQuery(id+"F3.imprint","IMPRINT",EDGE,{"derivedFrom":sQuery(id+"F3.wireOp",EDGE,"E1963")}),1.0]])]});
            var Q1;
            Q1=makeQuery(id+"F3.imprint","IMPRINT",FACE,{"disambiguationData":[TD([[makeQuery(id+"F3.imprint","IMPRINT",EDGE,{"derivedFrom":sQuery(id+"F3.wireOp",EDGE,"E1954")}),1.0]])]});
            extrude(context, id + "F4", {"entities" : qUnion([Q0, Q1]), "depth" : 12 * mm});
        }
        {
            var Q0;
            Q0=sQuery(id+"F3.wireOp",EDGE,"E1954");
            var Q1;
            Q1=sQuery(id+"F3.wireOp",EDGE,"E1963");
            extrude(context, id + "F5", {"bodyType" : ToolBodyType.SURFACE, "surfaceEntities" : qUnion([Q0, Q1]), "depth" : 10 * mm});
        }
    });
